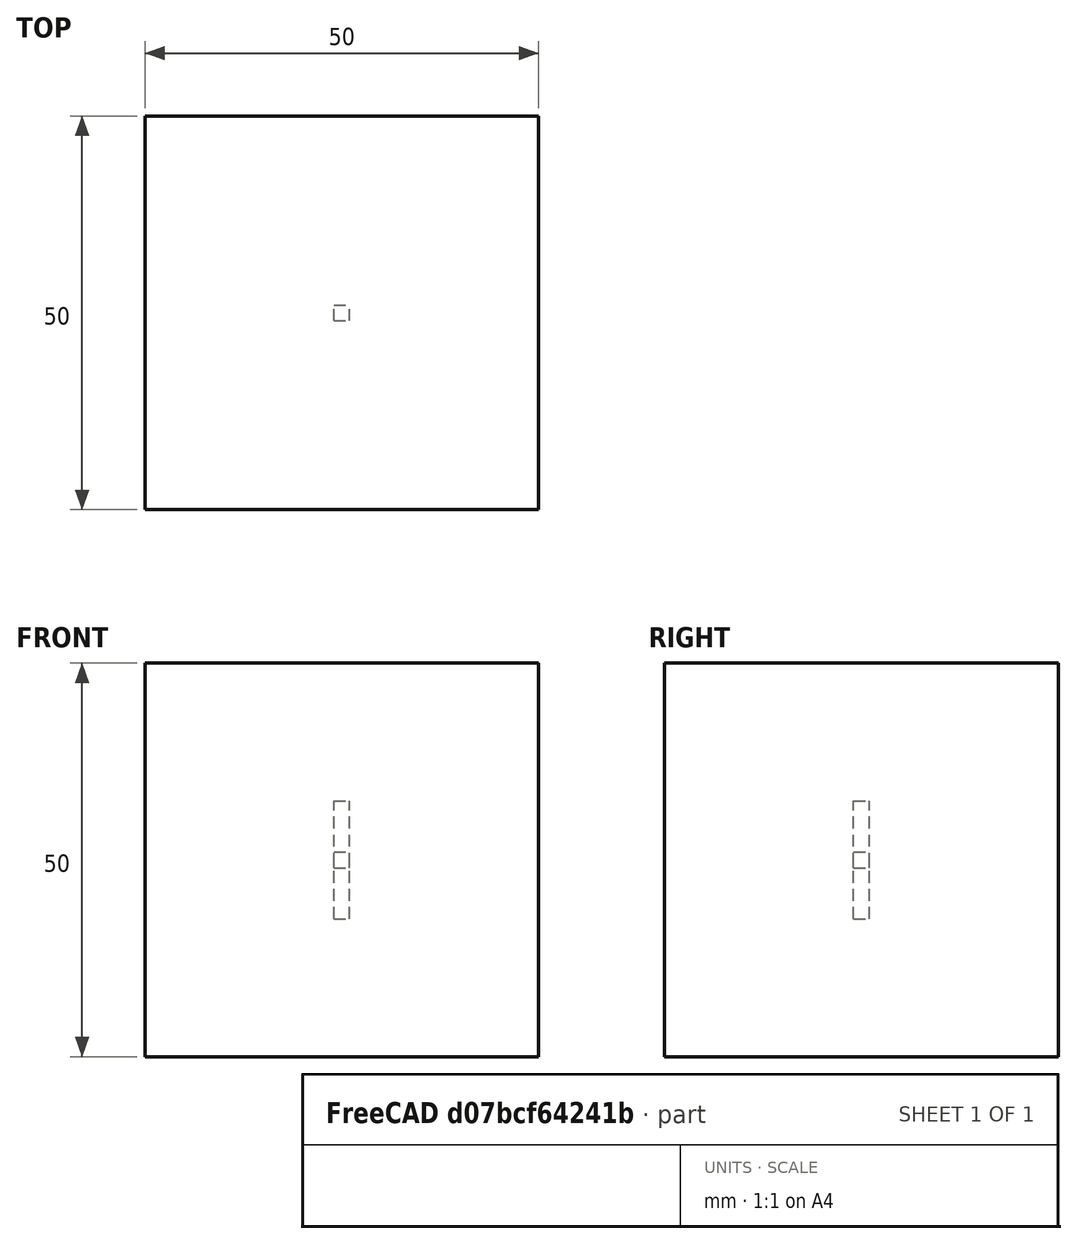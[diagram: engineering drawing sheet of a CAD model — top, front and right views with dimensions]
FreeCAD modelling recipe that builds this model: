
FCSTD DOCUMENT  (FreeCAD 1.0R39109 (Git))
Label: simple_array_expanded
License: All rights reserved
LicenseURL: http://en.wikipedia.org/wiki/All_rights_reserved
objects: App::DocumentObjectGroupPython×1269, App::Part×10, App::Link×6, App::FeaturePython×4, Part::FeaturePython×3
note: 3 computed .brp shape members not serialized (recipe doc carries the construction recipe); baked Part::Feature solids carry a one-line shape summary decoded from their .brp

FEATURE [App::DocumentObjectGroupPython] Constants  # scripted group (container) (typed FeaturePython)
FEATURE [App::DocumentObjectGroupPython] Variables  # scripted group (container) (typed FeaturePython)
FEATURE [App::DocumentObjectGroupPython] Quantities  # scripted group (container) (typed FeaturePython)
FEATURE [App::DocumentObjectGroupPython] Isotopes  # scripted group (container) (typed FeaturePython)
FEATURE [App::DocumentObjectGroupPython] Elements  # scripted group (container) (typed FeaturePython)
FEATURE [App::DocumentObjectGroupPython] G4_CESIUM_IODIDE  label="G4_CESIUM_IODIDE : 1.000"  # scripted group (container) (typed FeaturePython)
  n = 1
FEATURE [App::DocumentObjectGroupPython] LYSO  # scripted group (container) (typed FeaturePython)
  ABSLENGTH = ABSLENGTHLAR
  Dunit = g/cm3
  Dvalue = 7.1
  FASTCOMPONENT = SCINTLAR
  Group = -> [G4_CESIUM_IODIDE]
  RAYLEIGH = RAYLEIGHLAR
  REEMISSIONPROB = SCINTLAR
  RESOLUTIONSCALE = RS
  RINDEX = RINDEXLAR
  SCINTILLATIONCOMPONENT1 = SCINTLAR
  SCINTILLATIONCOMPONENT2 = SCINTLAR
  SCINTILLATIONTIMECONSTANT1 = FTC
  SCINTILLATIONTIMECONSTANT2 = STC
  SCINTILLATIONYIELD = SY
  SCINTILLATIONYIELD1 = RY1
  SCINTILLATIONYIELD2 = RY2
  SLOWCOMPONENT = SCINTLAR
  YIELDRATIO = YR
  conduct = 2
  density = 1
  expand = 3
  name = LYSO
  specific = 4
FEATURE [App::DocumentObjectGroupPython] G4_AIR  label="G4_AIR : 1.000"  # scripted group (container) (typed FeaturePython)
  n = 1
FEATURE [App::DocumentObjectGroupPython] Air  # scripted group (container) (typed FeaturePython)
  Dunit = mg/cm3
  Dvalue = 1.29
  Group = -> [G4_AIR]
  RINDEX = AirRINDEX
  conduct = 2
  density = 1
  expand = 3
  name = Air
  specific = 4
FEATURE [App::DocumentObjectGroupPython] G4_SILICON_DIOXIDE  label="G4_SILICON_DIOXIDE : 1.000"  # scripted group (container) (typed FeaturePython)
  n = 1
FEATURE [App::DocumentObjectGroupPython] Glass  # scripted group (container) (typed FeaturePython)
  Dunit = g/cm3
  Dvalue = 2.32
  Group = -> [G4_SILICON_DIOXIDE]
  RINDEX = RINDEXLAR
  conduct = 2
  density = 1
  expand = 3
  name = Glass
  specific = 4
FEATURE [App::DocumentObjectGroupPython] SY  # scripted group (container) (typed FeaturePython)
  coldim = 1
  values = 100000
FEATURE [App::DocumentObjectGroupPython] RS  # scripted group (container) (typed FeaturePython)
  coldim = 1
  values = 1
FEATURE [App::DocumentObjectGroupPython] FTC  # scripted group (container) (typed FeaturePython)
  coldim = 1
  values = 21.5*ns
FEATURE [App::DocumentObjectGroupPython] STC  # scripted group (container) (typed FeaturePython)
  coldim = 1
  values = 43.8*ns
FEATURE [App::DocumentObjectGroupPython] RY1  # scripted group (container) (typed FeaturePython)
  coldim = 1
  values = 95
FEATURE [App::DocumentObjectGroupPython] RY2  # scripted group (container) (typed FeaturePython)
  coldim = 1
  values = 5
FEATURE [App::DocumentObjectGroupPython] YR  # scripted group (container) (typed FeaturePython)
  coldim = 1
  values = 0.8
FEATURE [App::DocumentObjectGroupPython] SCINTLAR  # scripted group (container) (typed FeaturePython)
  coldim = 2
  values = <blob: 2358 chars omitted>
FEATURE [App::DocumentObjectGroupPython] RINDEXLAR  # scripted group (container) (typed FeaturePython)
  coldim = 2
  values = <blob: 9384 chars omitted>
FEATURE [App::DocumentObjectGroupPython] ABSLENGTHLAR  # scripted group (container) (typed FeaturePython)
  coldim = 2
  values = 7.74901*eV 10.0*m 7.77525*eV 10.0*m 7.80167*eV 10.0*m 7.82827*eV 10.0*m 7.85506*eV 10.0*m 7.88202*eV 10.0*m 7.90917*eV 10.0*m 7.93651*eV 10.0*m 7.96404*eV 10.0*m 7.99176*eV 10.0*m 8.01968*eV 10.0*m 8.04779*eV 10.0*m 8.07609*eV 10.0*m 8.1046*eV 10.0*m 8.13331*eV 10.0*m 8.16222*eV 10.0*m 8.19134*eV 10.0*m 8.22067*eV 10.0*m 8.25021*eV 10.0*m 8.27996*eV 10.0*m 8.30993*eV 10.0*m 8.34012*eV 10.0*m 8.37052*eV 10.0*m 8.40115*eV 10.0*m 8.432*eV 10.0*m 8.46308*eV 10.0*m 8.4944*eV 10.0*m 8.52594*eV 10.0*m 8.55772*eV 10.0*m 8.58973*eV 10.0*m 8.62199*eV 10.0*m 8.65449*eV 10.0*m 8.68723*eV 10.0*m 8.72023*eV 10.0*m 8.75347*eV 10.0*m 8.78697*eV 10.0*m 8.82073*eV 10.0*m 8.85475*eV 10.0*m 8.88903*eV 10.0*m 8.92358*eV 10.0*m 8.9584*eV 10.0*m 8.99349*eV 10.0*m 9.02885*eV 10.0*m 9.0645*eV 10.0*m 9.10043*eV 10.0*m 9.13664*eV 10.0*m 9.17314*eV 10.0*m 9.20994*eV 10.0*m 9.24703*eV 10.0*m 9.28442*eV 10.0*m 9.32212*eV 10.0*m 9.36012*eV 10.0*m 9.39844*eV 10.0*m 9.43707*eV 10.0*m 9.47602*eV 10.0*m 9.51529*eV 10.0*m 9.55489*eV 10.0*m 9.59481*eV 10.0*m 9.63508*eV 10.0*m 9.67568*eV 10.0*m 9.71663*eV 10.0*m 9.75792*eV 10.0*m 9.79957*eV 10.0*m 9.84158*eV 10.0*m 9.88394*eV 10.0*m 9.92668*eV 10.0*m 9.96978*eV 10.0*m 10.0133*eV 10.0*m 10.0571*eV 10.0*m 10.1014*eV 10.0*m 10.146*eV 10.0*m 10.191*eV 10.0*m 10.2365*eV 10.0*m 10.2823*eV 10.0*m 10.3286*eV 10.0*m 10.3752*eV 10.0*m 10.4223*eV 10.0*m 10.4699*eV 10.0*m 10.5178*eV 10.0*m 10.5662*eV 10.0*m 10.6151*eV 10.0*m 10.6644*eV 10.0*m 10.7142*eV 10.0*m 10.7644*eV 10.0*m 10.8151*eV 10.0*m 10.8663*eV 10.0*m 10.9179*eV 10.0*m 10.9701*eV 10.0*m 11.0228*eV 10.0*m 11.076*eV 10.0*m 11.1296*eV 10.0*m 11.1839*eV 10.0*m 11.2386*eV 10.0*m 11.2939*eV 10.0*m 11.3497*eV 10.0*m 11.4061*eV 10.0*m 11.463*eV 10.0*m 11.5206*eV 10.0*m 11.5787*eV 10.0*m 11.6373*eV 10.0*m
FEATURE [App::DocumentObjectGroupPython] RAYLEIGHLAR  # scripted group (container) (typed FeaturePython)
  coldim = 2
  values = 7.74901*eV 90.0*cm 7.77525*eV 90.0*cm 7.80167*eV 90.0*cm 7.82827*eV 90.0*cm 7.85506*eV 90.0*cm 7.88202*eV 90.0*cm 7.90917*eV 90.0*cm 7.93651*eV 90.0*cm 7.96404*eV 90.0*cm 7.99176*eV 90.0*cm 8.01968*eV 90.0*cm 8.04779*eV 90.0*cm 8.07609*eV 90.0*cm 8.1046*eV 90.0*cm 8.13331*eV 90.0*cm 8.16222*eV 90.0*cm 8.19134*eV 90.0*cm 8.22067*eV 90.0*cm 8.25021*eV 90.0*cm 8.27996*eV 90.0*cm 8.30993*eV 90.0*cm 8.34012*eV 90.0*cm 8.37052*eV 90.0*cm 8.40115*eV 90.0*cm 8.432*eV 90.0*cm 8.46308*eV 90.0*cm 8.4944*eV 90.0*cm 8.52594*eV 90.0*cm 8.55772*eV 90.0*cm 8.58973*eV 90.0*cm 8.62199*eV 90.0*cm 8.65449*eV 90.0*cm 8.68723*eV 90.0*cm 8.72023*eV 90.0*cm 8.75347*eV 90.0*cm 8.78697*eV 90.0*cm 8.82073*eV 90.0*cm 8.85475*eV 90.0*cm 8.88903*eV 90.0*cm 8.92358*eV 90.0*cm 8.9584*eV 90.0*cm 8.99349*eV 90.0*cm 9.02885*eV 90.0*cm 9.0645*eV 90.0*cm 9.10043*eV 90.0*cm 9.13664*eV 90.0*cm 9.17314*eV 90.0*cm 9.20994*eV 90.0*cm 9.24703*eV 90.0*cm 9.28442*eV 90.0*cm 9.32212*eV 90.0*cm 9.36012*eV 90.0*cm 9.39844*eV 90.0*cm 9.43707*eV 90.0*cm 9.47602*eV 90.0*cm 9.51529*eV 90.0*cm 9.55489*eV 90.0*cm 9.59481*eV 90.0*cm 9.63508*eV 90.0*cm 9.67568*eV 90.0*cm 9.71663*eV 90.0*cm 9.75792*eV 90.0*cm 9.79957*eV 90.0*cm 9.84158*eV 90.0*cm 9.88394*eV 90.0*cm 9.92668*eV 90.0*cm 9.96978*eV 90.0*cm 10.0133*eV 90.0*cm 10.0571*eV 90.0*cm 10.1014*eV 90.0*cm 10.146*eV 90.0*cm 10.191*eV 90.0*cm 10.2365*eV 90.0*cm 10.2823*eV 90.0*cm 10.3286*eV 90.0*cm 10.3752*eV 90.0*cm 10.4223*eV 90.0*cm 10.4699*eV 90.0*cm 10.5178*eV 90.0*cm 10.5662*eV 90.0*cm 10.6151*eV 90.0*cm 10.6644*eV 90.0*cm 10.7142*eV 90.0*cm 10.7644*eV 90.0*cm 10.8151*eV 90.0*cm 10.8663*eV 90.0*cm 10.9179*eV 90.0*cm 10.9701*eV 90.0*cm 11.0228*eV 90.0*cm 11.076*eV 90.0*cm 11.1296*eV 90.0*cm 11.1839*eV 90.0*cm 11.2386*eV 90.0*cm 11.2939*eV 90.0*cm 11.3497*eV 90.0*cm 11.4061*eV 90.0*cm 11.463*eV 90.0*cm 11.5206*eV 90.0*cm 11.5787*eV 90.0*cm 11.6373*eV 90.0*cm
FEATURE [App::DocumentObjectGroupPython] REFLECTIVITY  # scripted group (container) (typed FeaturePython)
  coldim = 2
  values = 2.034*eV 0.98 2.068*eV 0.98 2.103*eV 0.98 2.139*eV 0.98 2.177*eV 0.98 2.216*eV 0.98 2.256*eV 0.98 2.298*eV 0.98 2.341*eV 0.98 2.386*eV 0.98 2.433*eV 0.98 2.481*eV 0.98 2.532*eV 0.98 2.585*eV 0.98 2.64*eV 0.98 2.697*eV 0.98 2.757*eV 0.98 2.82*eV 0.98 2.885*eV 0.98 2.954*eV 0.98 3.026*eV 0.98 3.102*eV 0.98 3.181*eV 0.98 3.265*eV 0.98 3.353*eV 0.98 3.446*eV 0.98 3.545*eV 0.98 3.649*eV 0.98 3.76*eV 0.98 3.877*eV 0.98 4.002*eV 0.98 4.136*eV 0.98 5.0*eV 0.98 6.0*eV 0.98 7.0*eV 0.98 8.0*eV 0.98 9.0*eV 0.98 9.0*eV 0.98 10.0*eV 0.98 11.0*eV 0.98 11.6*eV 0.98
FEATURE [App::DocumentObjectGroupPython] EFFICIENCY  # scripted group (container) (typed FeaturePython)
  coldim = 2
  values = 2.034*eV 1 2.068*eV 1 2.103*eV 1 2.139*eV 1 2.177*eV 1 2.216*eV 1 2.256*eV 1 2.298*eV 1 2.341*eV 1 2.386*eV 1 2.433*eV 1 2.481*eV 1 2.532*eV 1 2.585*eV 1 2.64*eV 1 2.697*eV 1 2.757*eV 1 2.82*eV 1 2.885*eV 1 2.954*eV 1 3.026*eV 1 3.102*eV 1 3.181*eV  1 3.265*eV 1 3.353*eV 1 3.446*eV 1 3.545*eV 1 3.649*eV 1 3.76*eV 1 3.877*eV 1 4.002*eV 1 4.136*eV 1 5.0*eV 1 6.0*eV 1 7.0*eV 1 8.0*eV 1 9.0*eV 1 9.0*eV 1 10.0*eV 1 11.0*eV 1 11.6*eV 1
FEATURE [App::DocumentObjectGroupPython] AirRINDEX  # scripted group (container) (typed FeaturePython)
  coldim = 2
  values = 2.034*eV 1 2.068*eV 1 2.103*eV 1 2.139*eV 1 2.177*eV 1 2.216*eV 1 2.256*eV 1 2.298*eV 1 2.341*eV 1 2.386*eV 1 2.433*eV 1 2.481*eV 1 2.532*eV 1 2.585*eV 1 2.64*eV 1 2.697*eV 1 2.757*eV 1 2.82*eV 1 2.885*eV 1 2.954*eV 1 3.026*eV 1 3.102*eV 1 3.181*eV 1 3.265*eV 1 3.353*eV 1 3.446*eV 1 3.545*eV 1 3.649*eV 1 3.76*eV 1 3.877*eV 1 4.002*eV 1 4.136*eV 1 5.0*eV 1 6.0*eV 1 7.0*eV 1 8.0*eV 1 9.0*eV 1 10.0*eV 1 11.0*eV 1 11.6*eV 1
FEATURE [App::DocumentObjectGroupPython] Matrix  # scripted group (container) (typed FeaturePython)
  Group = -> [SY,RS,FTC,STC,RY1,RY2,YR,SCINTLAR,RINDEXLAR,ABSLENGTHLAR,RAYLEIGHLAR,REFLECTIVITY,EFFICIENCY,AirRINDEX]
FEATURE [App::DocumentObjectGroupPython] ScintWrap  # scripted group (container) (typed FeaturePython)
  EFFICIENCY = EFFICIENCY
  REFLECTIVITY = REFLECTIVITY
  finish = 39
  model = 0
  type = 2
  value = 1
FEATURE [App::DocumentObjectGroupPython] Surfaces  # scripted group (container) (typed FeaturePython)
  Group = -> [ScintWrap]
FEATURE [App::DocumentObjectGroupPython] Opticals  # scripted group (container) (typed FeaturePython)
  Group = -> [Matrix,Surfaces]
FEATURE [App::DocumentObjectGroupPython] G4Isotopes  # scripted group (container) (typed FeaturePython)
FEATURE [App::DocumentObjectGroupPython] H_element  # scripted group (container) (typed FeaturePython)
  Z = 1
  atom_value = 1.008
  formula = H
  name = H_element
FEATURE [App::DocumentObjectGroupPython] He_element  # scripted group (container) (typed FeaturePython)
  Z = 2
  atom_value = 4.0026
  formula = He
  name = He_element
FEATURE [App::DocumentObjectGroupPython] Li_element  # scripted group (container) (typed FeaturePython)
  Z = 3
  atom_value = 6.94
  formula = Li
  name = Li_element
FEATURE [App::DocumentObjectGroupPython] Be_element  # scripted group (container) (typed FeaturePython)
  Z = 4
  atom_value = 9.01218
  formula = Be
  name = Be_element
FEATURE [App::DocumentObjectGroupPython] B_element  # scripted group (container) (typed FeaturePython)
  Z = 5
  atom_value = 10.81
  formula = B
  name = B_element
FEATURE [App::DocumentObjectGroupPython] C_element  # scripted group (container) (typed FeaturePython)
  Z = 6
  atom_value = 12.011
  formula = C
  name = C_element
FEATURE [App::DocumentObjectGroupPython] N_element  # scripted group (container) (typed FeaturePython)
  Z = 7
  atom_value = 14.007
  formula = N
  name = N_element
FEATURE [App::DocumentObjectGroupPython] O_element  # scripted group (container) (typed FeaturePython)
  Z = 8
  atom_value = 15.999
  formula = O
  name = O_element
FEATURE [App::DocumentObjectGroupPython] F_element  # scripted group (container) (typed FeaturePython)
  Z = 9
  atom_value = 18.9984
  formula = F
  name = F_element
FEATURE [App::DocumentObjectGroupPython] Ne_element  # scripted group (container) (typed FeaturePython)
  Z = 10
  atom_value = 20.1797
  formula = Ne
  name = Ne_element
FEATURE [App::DocumentObjectGroupPython] Na_element  # scripted group (container) (typed FeaturePython)
  Z = 11
  atom_value = 22.9898
  formula = Na
  name = Na_element
FEATURE [App::DocumentObjectGroupPython] Mg_element  # scripted group (container) (typed FeaturePython)
  Z = 12
  atom_value = 24.305
  formula = Mg
  name = Mg_element
FEATURE [App::DocumentObjectGroupPython] Al_element  # scripted group (container) (typed FeaturePython)
  Z = 13
  atom_value = 26.9815
  formula = Al
  name = Al_element
FEATURE [App::DocumentObjectGroupPython] Si_element  # scripted group (container) (typed FeaturePython)
  Z = 14
  atom_value = 28.085
  formula = Si
  name = Si_element
FEATURE [App::DocumentObjectGroupPython] P_element  # scripted group (container) (typed FeaturePython)
  Z = 15
  atom_value = 30.9738
  formula = P
  name = P_element
FEATURE [App::DocumentObjectGroupPython] S_element  # scripted group (container) (typed FeaturePython)
  Z = 16
  atom_value = 32.06
  formula = S
  name = S_element
FEATURE [App::DocumentObjectGroupPython] Cl_element  # scripted group (container) (typed FeaturePython)
  Z = 17
  atom_value = 35.45
  formula = Cl
  name = Cl_element
FEATURE [App::DocumentObjectGroupPython] Ar_element  # scripted group (container) (typed FeaturePython)
  Z = 18
  atom_value = 39.95
  formula = Ar
  name = Ar_element
FEATURE [App::DocumentObjectGroupPython] K_element  # scripted group (container) (typed FeaturePython)
  Z = 19
  atom_value = 39.0983
  formula = K
  name = K_element
FEATURE [App::DocumentObjectGroupPython] Ca_element  # scripted group (container) (typed FeaturePython)
  Z = 20
  atom_value = 40.078
  formula = Ca
  name = Ca_element
FEATURE [App::DocumentObjectGroupPython] Sc_element  # scripted group (container) (typed FeaturePython)
  Z = 21
  atom_value = 44.9559
  formula = Sc
  name = Sc_element
FEATURE [App::DocumentObjectGroupPython] Ti_element  # scripted group (container) (typed FeaturePython)
  Z = 22
  atom_value = 47.867
  formula = Ti
  name = Ti_element
FEATURE [App::DocumentObjectGroupPython] V_element  # scripted group (container) (typed FeaturePython)
  Z = 23
  atom_value = 50.9415
  formula = V
  name = V_element
FEATURE [App::DocumentObjectGroupPython] Cr_element  # scripted group (container) (typed FeaturePython)
  Z = 24
  atom_value = 51.9961
  formula = Cr
  name = Cr_element
FEATURE [App::DocumentObjectGroupPython] Mn_element  # scripted group (container) (typed FeaturePython)
  Z = 25
  atom_value = 54.938
  formula = Mn
  name = Mn_element
FEATURE [App::DocumentObjectGroupPython] Fe_element  # scripted group (container) (typed FeaturePython)
  Z = 26
  atom_value = 55.845
  formula = Fe
  name = Fe_element
FEATURE [App::DocumentObjectGroupPython] Co_element  # scripted group (container) (typed FeaturePython)
  Z = 27
  atom_value = 58.9332
  formula = Co
  name = Co_element
FEATURE [App::DocumentObjectGroupPython] Ni_element  # scripted group (container) (typed FeaturePython)
  Z = 28
  atom_value = 58.6934
  formula = Ni
  name = Ni_element
FEATURE [App::DocumentObjectGroupPython] Cu_element  # scripted group (container) (typed FeaturePython)
  Z = 29
  atom_value = 63.546
  formula = Cu
  name = Cu_element
FEATURE [App::DocumentObjectGroupPython] Zn_element  # scripted group (container) (typed FeaturePython)
  Z = 30
  atom_value = 65.38
  formula = Zn
  name = Zn_element
FEATURE [App::DocumentObjectGroupPython] Ga_element  # scripted group (container) (typed FeaturePython)
  Z = 31
  atom_value = 69.723
  formula = Ga
  name = Ga_element
FEATURE [App::DocumentObjectGroupPython] Ge_element  # scripted group (container) (typed FeaturePython)
  Z = 32
  atom_value = 72.63
  formula = Ge
  name = Ge_element
FEATURE [App::DocumentObjectGroupPython] As_element  # scripted group (container) (typed FeaturePython)
  Z = 33
  atom_value = 74.9216
  formula = As
  name = As_element
FEATURE [App::DocumentObjectGroupPython] Se_element  # scripted group (container) (typed FeaturePython)
  Z = 34
  atom_value = 78.971
  formula = Se
  name = Se_element
FEATURE [App::DocumentObjectGroupPython] Br_element  # scripted group (container) (typed FeaturePython)
  Z = 35
  atom_value = 79.904
  formula = Br
  name = Br_element
FEATURE [App::DocumentObjectGroupPython] Kr_element  # scripted group (container) (typed FeaturePython)
  Z = 36
  atom_value = 83.798
  formula = Kr
  name = Kr_element
FEATURE [App::DocumentObjectGroupPython] Rb_element  # scripted group (container) (typed FeaturePython)
  Z = 37
  atom_value = 85.4678
  formula = Rb
  name = Rb_element
FEATURE [App::DocumentObjectGroupPython] Sr_element  # scripted group (container) (typed FeaturePython)
  Z = 38
  atom_value = 87.62
  formula = Sr
  name = Sr_element
FEATURE [App::DocumentObjectGroupPython] Y_element  # scripted group (container) (typed FeaturePython)
  Z = 39
  atom_value = 88.9058
  formula = Y
  name = Y_element
FEATURE [App::DocumentObjectGroupPython] Zr_element  # scripted group (container) (typed FeaturePython)
  Z = 40
  atom_value = 91.224
  formula = Zr
  name = Zr_element
FEATURE [App::DocumentObjectGroupPython] Nb_element  # scripted group (container) (typed FeaturePython)
  Z = 41
  atom_value = 92.9064
  formula = Nb
  name = Nb_element
FEATURE [App::DocumentObjectGroupPython] Mo_element  # scripted group (container) (typed FeaturePython)
  Z = 42
  atom_value = 95.95
  formula = Mo
  name = Mo_element
FEATURE [App::DocumentObjectGroupPython] Tc_element  # scripted group (container) (typed FeaturePython)
  Z = 43
  atom_value = 97
  formula = Tc
  name = Tc_element
FEATURE [App::DocumentObjectGroupPython] Ru_element  # scripted group (container) (typed FeaturePython)
  Z = 44
  atom_value = 101.07
  formula = Ru
  name = Ru_element
FEATURE [App::DocumentObjectGroupPython] Rh_element  # scripted group (container) (typed FeaturePython)
  Z = 45
  atom_value = 102.905
  formula = Rh
  name = Rh_element
FEATURE [App::DocumentObjectGroupPython] Pd_element  # scripted group (container) (typed FeaturePython)
  Z = 46
  atom_value = 106.42
  formula = Pd
  name = Pd_element
FEATURE [App::DocumentObjectGroupPython] Ag_element  # scripted group (container) (typed FeaturePython)
  Z = 47
  atom_value = 107.868
  formula = Ag
  name = Ag_element
FEATURE [App::DocumentObjectGroupPython] Cd_element  # scripted group (container) (typed FeaturePython)
  Z = 48
  atom_value = 112.414
  formula = Cd
  name = Cd_element
FEATURE [App::DocumentObjectGroupPython] In_element  # scripted group (container) (typed FeaturePython)
  Z = 49
  atom_value = 114.818
  formula = In
  name = In_element
FEATURE [App::DocumentObjectGroupPython] Sn_element  # scripted group (container) (typed FeaturePython)
  Z = 50
  atom_value = 118.71
  formula = Sn
  name = Sn_element
FEATURE [App::DocumentObjectGroupPython] Sb_element  # scripted group (container) (typed FeaturePython)
  Z = 51
  atom_value = 121.76
  formula = Sb
  name = Sb_element
FEATURE [App::DocumentObjectGroupPython] Te_element  # scripted group (container) (typed FeaturePython)
  Z = 52
  atom_value = 127.6
  formula = Te
  name = Te_element
FEATURE [App::DocumentObjectGroupPython] I_element  # scripted group (container) (typed FeaturePython)
  Z = 53
  atom_value = 126.904
  formula = I
  name = I_element
FEATURE [App::DocumentObjectGroupPython] Xe_element  # scripted group (container) (typed FeaturePython)
  Z = 54
  atom_value = 131.293
  formula = Xe
  name = Xe_element
FEATURE [App::DocumentObjectGroupPython] Cs_element  # scripted group (container) (typed FeaturePython)
  Z = 55
  atom_value = 132.905
  formula = Cs
  name = Cs_element
FEATURE [App::DocumentObjectGroupPython] Ba_element  # scripted group (container) (typed FeaturePython)
  Z = 56
  atom_value = 137.327
  formula = Ba
  name = Ba_element
FEATURE [App::DocumentObjectGroupPython] La_element  # scripted group (container) (typed FeaturePython)
  Z = 57
  atom_value = 138.905
  formula = La
  name = La_element
FEATURE [App::DocumentObjectGroupPython] Ce_element  # scripted group (container) (typed FeaturePython)
  Z = 58
  atom_value = 140.116
  formula = Ce
  name = Ce_element
FEATURE [App::DocumentObjectGroupPython] Pr_element  # scripted group (container) (typed FeaturePython)
  Z = 59
  atom_value = 140.908
  formula = Pr
  name = Pr_element
FEATURE [App::DocumentObjectGroupPython] Nd_element  # scripted group (container) (typed FeaturePython)
  Z = 60
  atom_value = 144.242
  formula = Nd
  name = Nd_element
FEATURE [App::DocumentObjectGroupPython] Pm_element  # scripted group (container) (typed FeaturePython)
  Z = 61
  atom_value = 145
  formula = Pm
  name = Pm_element
FEATURE [App::DocumentObjectGroupPython] Sm_element  # scripted group (container) (typed FeaturePython)
  Z = 62
  atom_value = 150.36
  formula = Sm
  name = Sm_element
FEATURE [App::DocumentObjectGroupPython] Eu_element  # scripted group (container) (typed FeaturePython)
  Z = 63
  atom_value = 151.964
  formula = Eu
  name = Eu_element
FEATURE [App::DocumentObjectGroupPython] Gd_element  # scripted group (container) (typed FeaturePython)
  Z = 64
  atom_value = 157.25
  formula = Gd
  name = Gd_element
FEATURE [App::DocumentObjectGroupPython] Tb_element  # scripted group (container) (typed FeaturePython)
  Z = 65
  atom_value = 158.925
  formula = Tb
  name = Tb_element
FEATURE [App::DocumentObjectGroupPython] Dy_element  # scripted group (container) (typed FeaturePython)
  Z = 66
  atom_value = 162.5
  formula = Dy
  name = Dy_element
FEATURE [App::DocumentObjectGroupPython] Ho_element  # scripted group (container) (typed FeaturePython)
  Z = 67
  atom_value = 164.93
  formula = Ho
  name = Ho_element
FEATURE [App::DocumentObjectGroupPython] Er_element  # scripted group (container) (typed FeaturePython)
  Z = 68
  atom_value = 167.259
  formula = Er
  name = Er_element
FEATURE [App::DocumentObjectGroupPython] Tm_element  # scripted group (container) (typed FeaturePython)
  Z = 69
  atom_value = 168.934
  formula = Tm
  name = Tm_element
FEATURE [App::DocumentObjectGroupPython] Yb_element  # scripted group (container) (typed FeaturePython)
  Z = 70
  atom_value = 173.045
  formula = Yb
  name = Yb_element
FEATURE [App::DocumentObjectGroupPython] Lu_element  # scripted group (container) (typed FeaturePython)
  Z = 71
  atom_value = 174.967
  formula = Lu
  name = Lu_element
FEATURE [App::DocumentObjectGroupPython] Hf_element  # scripted group (container) (typed FeaturePython)
  Z = 72
  atom_value = 178.49
  formula = Hf
  name = Hf_element
FEATURE [App::DocumentObjectGroupPython] Ta_element  # scripted group (container) (typed FeaturePython)
  Z = 73
  atom_value = 180.948
  formula = Ta
  name = Ta_element
FEATURE [App::DocumentObjectGroupPython] W_element  # scripted group (container) (typed FeaturePython)
  Z = 74
  atom_value = 183.84
  formula = W
  name = W_element
FEATURE [App::DocumentObjectGroupPython] Re_element  # scripted group (container) (typed FeaturePython)
  Z = 75
  atom_value = 186.207
  formula = Re
  name = Re_element
FEATURE [App::DocumentObjectGroupPython] Os_element  # scripted group (container) (typed FeaturePython)
  Z = 76
  atom_value = 190.23
  formula = Os
  name = Os_element
FEATURE [App::DocumentObjectGroupPython] Ir_element  # scripted group (container) (typed FeaturePython)
  Z = 77
  atom_value = 192.217
  formula = Ir
  name = Ir_element
FEATURE [App::DocumentObjectGroupPython] Pt_element  # scripted group (container) (typed FeaturePython)
  Z = 78
  atom_value = 195.084
  formula = Pt
  name = Pt_element
FEATURE [App::DocumentObjectGroupPython] Au_element  # scripted group (container) (typed FeaturePython)
  Z = 79
  atom_value = 196.967
  formula = Au
  name = Au_element
FEATURE [App::DocumentObjectGroupPython] Hg_element  # scripted group (container) (typed FeaturePython)
  Z = 80
  atom_value = 200.592
  formula = Hg
  name = Hg_element
FEATURE [App::DocumentObjectGroupPython] Tl_element  # scripted group (container) (typed FeaturePython)
  Z = 81
  atom_value = 204.38
  formula = Tl
  name = Tl_element
FEATURE [App::DocumentObjectGroupPython] Pb_element  # scripted group (container) (typed FeaturePython)
  Z = 82
  atom_value = 207.2
  formula = Pb
  name = Pb_element
FEATURE [App::DocumentObjectGroupPython] Bi_element  # scripted group (container) (typed FeaturePython)
  Z = 83
  atom_value = 208.98
  formula = Bi
  name = Bi_element
FEATURE [App::DocumentObjectGroupPython] Po_element  # scripted group (container) (typed FeaturePython)
  Z = 84
  atom_value = 209
  formula = Po
  name = Po_element
FEATURE [App::DocumentObjectGroupPython] At_element  # scripted group (container) (typed FeaturePython)
  Z = 85
  atom_value = 210
  formula = At
  name = At_element
FEATURE [App::DocumentObjectGroupPython] Rn_element  # scripted group (container) (typed FeaturePython)
  Z = 86
  atom_value = 222
  formula = Rn
  name = Rn_element
FEATURE [App::DocumentObjectGroupPython] Fr_element  # scripted group (container) (typed FeaturePython)
  Z = 87
  atom_value = 223
  formula = Fr
  name = Fr_element
FEATURE [App::DocumentObjectGroupPython] Ra_element  # scripted group (container) (typed FeaturePython)
  Z = 88
  atom_value = 226
  formula = Ra
  name = Ra_element
FEATURE [App::DocumentObjectGroupPython] Ac_element  # scripted group (container) (typed FeaturePython)
  Z = 89
  atom_value = 227
  formula = Ac
  name = Ac_element
FEATURE [App::DocumentObjectGroupPython] Th_element  # scripted group (container) (typed FeaturePython)
  Z = 90
  atom_value = 232.038
  formula = Th
  name = Th_element
FEATURE [App::DocumentObjectGroupPython] Pa_element  # scripted group (container) (typed FeaturePython)
  Z = 91
  atom_value = 231.036
  formula = Pa
  name = Pa_element
FEATURE [App::DocumentObjectGroupPython] U_element  # scripted group (container) (typed FeaturePython)
  Z = 92
  atom_value = 238.029
  formula = U
  name = U_element
FEATURE [App::DocumentObjectGroupPython] Np_element  # scripted group (container) (typed FeaturePython)
  Z = 93
  atom_value = 237
  formula = Np
  name = Np_element
FEATURE [App::DocumentObjectGroupPython] Pu_element  # scripted group (container) (typed FeaturePython)
  Z = 94
  atom_value = 244
  formula = Pu
  name = Pu_element
FEATURE [App::DocumentObjectGroupPython] Am_element  # scripted group (container) (typed FeaturePython)
  Z = 95
  atom_value = 243
  formula = Am
  name = Am_element
FEATURE [App::DocumentObjectGroupPython] Cm_element  # scripted group (container) (typed FeaturePython)
  Z = 96
  atom_value = 247
  formula = Cm
  name = Cm_element
FEATURE [App::DocumentObjectGroupPython] Bk_element  # scripted group (container) (typed FeaturePython)
  Z = 97
  atom_value = 247
  formula = Bk
  name = Bk_element
FEATURE [App::DocumentObjectGroupPython] Cf_element  # scripted group (container) (typed FeaturePython)
  Z = 98
  atom_value = 251
  formula = Cf
  name = Cf_element
FEATURE [App::DocumentObjectGroupPython] G4Elements  # scripted group (container) (typed FeaturePython)
  Group = -> [H_element,He_element,Li_element,Be_element,B_element,C_element,N_element,O_element,F_element,Ne_element,Na_element,Mg_element,Al_element,Si_element,P_element,S_element,Cl_element,Ar_element,K_element,Ca_element,Sc_element,Ti_element,V_element,Cr_element,Mn_element,Fe_element,Co_element,Ni_element,Cu_element,Zn_element,Ga_element,Ge_element,As_element,Se_element,Br_element,Kr_element,Rb_element,+61 more]
FEATURE [App::DocumentObjectGroupPython] H_element001  label="H_element : 0.101"  # scripted group (container) (typed FeaturePython)
  n = 0.101327
FEATURE [App::DocumentObjectGroupPython] C_element001  label="C_element : 0.775"  # scripted group (container) (typed FeaturePython)
  n = 0.7755
FEATURE [App::DocumentObjectGroupPython] N_element001  label="N_element : 0.035"  # scripted group (container) (typed FeaturePython)
  n = 0.035057
FEATURE [App::DocumentObjectGroupPython] O_element001  label="O_element : 0.052"  # scripted group (container) (typed FeaturePython)
  n = 0.0523159
FEATURE [App::DocumentObjectGroupPython] F_element001  label="F_element : 0.017"  # scripted group (container) (typed FeaturePython)
  n = 0.017422
FEATURE [App::DocumentObjectGroupPython] Ca_element001  label="Ca_element : 0.018"  # scripted group (container) (typed FeaturePython)
  n = 0.018378
FEATURE [App::DocumentObjectGroupPython] G4_A_150_TISSUE  label="G4_A-150_TISSUE"  # scripted group (container) (typed FeaturePython)
  Dunit = g/cm3
  Dvalue = 1.127
  Group = -> [H_element001,C_element001,N_element001,O_element001,F_element001,Ca_element001]
  conduct = 2
  density = 1
  expand = 3
  formula = G4_A-150_TISSUE
  name = G4_A-150_TISSUE
  specific = 4
FEATURE [App::DocumentObjectGroupPython] C_element002  label="C_element : 3"  # scripted group (container) (typed FeaturePython)
  n = 3
  ref = C_element
FEATURE [App::DocumentObjectGroupPython] H_element002  label="H_element : 6"  # scripted group (container) (typed FeaturePython)
  n = 6
  ref = H_element
FEATURE [App::DocumentObjectGroupPython] O_element002  label="O_element : 1"  # scripted group (container) (typed FeaturePython)
  n = 1
  ref = O_element
FEATURE [App::DocumentObjectGroupPython] G4_ACETONE  # scripted group (container) (typed FeaturePython)
  Dunit = g/cm3
  Dvalue = 0.7899
  Group = -> [C_element002,H_element002,O_element002]
  conduct = 2
  density = 1
  expand = 3
  formula = G4_ACETONE
  name = G4_ACETONE
  specific = 4
FEATURE [App::DocumentObjectGroupPython] C_element003  label="C_element : 2"  # scripted group (container) (typed FeaturePython)
  n = 2
  ref = C_element
FEATURE [App::DocumentObjectGroupPython] H_element003  label="H_element : 2"  # scripted group (container) (typed FeaturePython)
  n = 2
  ref = H_element
FEATURE [App::DocumentObjectGroupPython] G4_ACETYLENE  # scripted group (container) (typed FeaturePython)
  Dunit = g/cm3
  Dvalue = 0.0010967
  Group = -> [C_element003,H_element003]
  conduct = 2
  density = 1
  expand = 3
  formula = G4_ACETYLENE
  name = G4_ACETYLENE
  specific = 4
FEATURE [App::DocumentObjectGroupPython] C_element004  label="C_element : 5"  # scripted group (container) (typed FeaturePython)
  n = 5
  ref = C_element
FEATURE [App::DocumentObjectGroupPython] H_element004  label="H_element : 5"  # scripted group (container) (typed FeaturePython)
  n = 5
  ref = H_element
FEATURE [App::DocumentObjectGroupPython] N_element002  label="N_element : 5"  # scripted group (container) (typed FeaturePython)
  n = 5
  ref = N_element
FEATURE [App::DocumentObjectGroupPython] G4_ADENINE  # scripted group (container) (typed FeaturePython)
  Dunit = g/cm3
  Dvalue = 1.6
  Group = -> [C_element004,H_element004,N_element002]
  conduct = 2
  density = 1
  expand = 3
  formula = G4_ADENINE
  name = G4_ADENINE
  specific = 4
FEATURE [App::DocumentObjectGroupPython] H_element005  label="H_element : 0.114"  # scripted group (container) (typed FeaturePython)
  n = 0.114
FEATURE [App::DocumentObjectGroupPython] C_element005  label="C_element : 0.598"  # scripted group (container) (typed FeaturePython)
  n = 0.598
FEATURE [App::DocumentObjectGroupPython] N_element003  label="N_element : 0.007"  # scripted group (container) (typed FeaturePython)
  n = 0.007
FEATURE [App::DocumentObjectGroupPython] O_element003  label="O_element : 0.278"  # scripted group (container) (typed FeaturePython)
  n = 0.278
FEATURE [App::DocumentObjectGroupPython] Na_element001  label="Na_element : 0.001"  # scripted group (container) (typed FeaturePython)
  n = 0.001
FEATURE [App::DocumentObjectGroupPython] S_element001  label="S_element : 0.001"  # scripted group (container) (typed FeaturePython)
  n = 0.001
FEATURE [App::DocumentObjectGroupPython] Cl_element001  label="Cl_element : 0.001"  # scripted group (container) (typed FeaturePython)
  n = 0.001
FEATURE [App::DocumentObjectGroupPython] G4_ADIPOSE_TISSUE_ICRP  # scripted group (container) (typed FeaturePython)
  Dunit = g/cm3
  Dvalue = 0.95
  Group = -> [H_element005,C_element005,N_element003,O_element003,Na_element001,S_element001,Cl_element001]
  conduct = 2
  density = 1
  expand = 3
  formula = G4_ADIPOSE_TISSUE_ICRP
  name = G4_ADIPOSE_TISSUE_ICRP
  specific = 4
FEATURE [App::DocumentObjectGroupPython] C_element006  label="C_element : 0.000"  # scripted group (container) (typed FeaturePython)
  n = 0.000124
FEATURE [App::DocumentObjectGroupPython] N_element004  label="N_element : 0.755"  # scripted group (container) (typed FeaturePython)
  n = 0.755268
FEATURE [App::DocumentObjectGroupPython] O_element004  label="O_element : 0.232"  # scripted group (container) (typed FeaturePython)
  n = 0.231781
FEATURE [App::DocumentObjectGroupPython] Ar_element001  label="Ar_element : 0.013"  # scripted group (container) (typed FeaturePython)
  n = 0.012827
FEATURE [App::DocumentObjectGroupPython] G4_AIR001  label="G4_AIR"  # scripted group (container) (typed FeaturePython)
  Dunit = g/cm3
  Dvalue = 0.00120479
  Group = -> [C_element006,N_element004,O_element004,Ar_element001]
  conduct = 2
  density = 1
  expand = 3
  formula = G4_AIR
  name = G4_AIR
  specific = 4
FEATURE [App::DocumentObjectGroupPython] C_element007  label="C_element : 006"  # scripted group (container) (typed FeaturePython)
  n = 3
  ref = C_element
FEATURE [App::DocumentObjectGroupPython] H_element006  label="H_element : 7"  # scripted group (container) (typed FeaturePython)
  n = 7
  ref = H_element
FEATURE [App::DocumentObjectGroupPython] N_element005  label="N_element : 1"  # scripted group (container) (typed FeaturePython)
  n = 1
  ref = N_element
FEATURE [App::DocumentObjectGroupPython] O_element005  label="O_element : 2"  # scripted group (container) (typed FeaturePython)
  n = 2
  ref = O_element
FEATURE [App::DocumentObjectGroupPython] G4_ALANINE  # scripted group (container) (typed FeaturePython)
  Dunit = g/cm3
  Dvalue = 1.42
  Group = -> [C_element007,H_element006,N_element005,O_element005]
  conduct = 2
  density = 1
  expand = 3
  formula = G4_ALANINE
  name = G4_ALANINE
  specific = 4
FEATURE [App::DocumentObjectGroupPython] Al_element001  label="Al_element : 2"  # scripted group (container) (typed FeaturePython)
  n = 2
  ref = Al_element
FEATURE [App::DocumentObjectGroupPython] O_element006  label="O_element : 3"  # scripted group (container) (typed FeaturePython)
  n = 3
  ref = O_element
FEATURE [App::DocumentObjectGroupPython] G4_ALUMINUM_OXIDE  # scripted group (container) (typed FeaturePython)
  Dunit = g/cm3
  Dvalue = 3.97
  Group = -> [Al_element001,O_element006]
  conduct = 2
  density = 1
  expand = 3
  formula = G4_ALUMINUM_OXIDE
  name = G4_ALUMINUM_OXIDE
  specific = 4
FEATURE [App::DocumentObjectGroupPython] H_element007  label="H_element : 0.106"  # scripted group (container) (typed FeaturePython)
  n = 0.10593
FEATURE [App::DocumentObjectGroupPython] C_element008  label="C_element : 0.789"  # scripted group (container) (typed FeaturePython)
  n = 0.788974
FEATURE [App::DocumentObjectGroupPython] O_element007  label="O_element : 0.105"  # scripted group (container) (typed FeaturePython)
  n = 0.105096
FEATURE [App::DocumentObjectGroupPython] G4_AMBER  # scripted group (container) (typed FeaturePython)
  Dunit = g/cm3
  Dvalue = 1.1
  Group = -> [H_element007,C_element008,O_element007]
  conduct = 2
  density = 1
  expand = 3
  formula = G4_AMBER
  name = G4_AMBER
  specific = 4
FEATURE [App::DocumentObjectGroupPython] N_element006  label="N_element : 006"  # scripted group (container) (typed FeaturePython)
  n = 1
  ref = N_element
FEATURE [App::DocumentObjectGroupPython] H_element008  label="H_element : 3"  # scripted group (container) (typed FeaturePython)
  n = 3
  ref = H_element
FEATURE [App::DocumentObjectGroupPython] G4_AMMONIA  # scripted group (container) (typed FeaturePython)
  Dunit = g/cm3
  Dvalue = 0.000826019
  Group = -> [N_element006,H_element008]
  conduct = 2
  density = 1
  expand = 3
  formula = G4_AMMONIA
  name = G4_AMMONIA
  specific = 4
FEATURE [App::DocumentObjectGroupPython] C_element009  label="C_element : 6"  # scripted group (container) (typed FeaturePython)
  n = 6
  ref = C_element
FEATURE [App::DocumentObjectGroupPython] H_element009  label="H_element : 008"  # scripted group (container) (typed FeaturePython)
  n = 7
  ref = H_element
FEATURE [App::DocumentObjectGroupPython] N_element007  label="N_element : 007"  # scripted group (container) (typed FeaturePython)
  n = 1
  ref = N_element
FEATURE [App::DocumentObjectGroupPython] G4_ANILINE  # scripted group (container) (typed FeaturePython)
  Dunit = g/cm3
  Dvalue = 1.0235
  Group = -> [C_element009,H_element009,N_element007]
  conduct = 2
  density = 1
  expand = 3
  formula = G4_ANILINE
  name = G4_ANILINE
  specific = 4
FEATURE [App::DocumentObjectGroupPython] C_element010  label="C_element : 14"  # scripted group (container) (typed FeaturePython)
  n = 14
  ref = C_element
FEATURE [App::DocumentObjectGroupPython] H_element010  label="H_element : 10"  # scripted group (container) (typed FeaturePython)
  n = 10
  ref = H_element
FEATURE [App::DocumentObjectGroupPython] G4_ANTHRACENE  # scripted group (container) (typed FeaturePython)
  Dunit = g/cm3
  Dvalue = 1.283
  Group = -> [C_element010,H_element010]
  conduct = 2
  density = 1
  expand = 3
  formula = G4_ANTHRACENE
  name = G4_ANTHRACENE
  specific = 4
FEATURE [App::DocumentObjectGroupPython] H_element011  label="H_element : 0.065"  # scripted group (container) (typed FeaturePython)
  n = 0.0654709
FEATURE [App::DocumentObjectGroupPython] C_element011  label="C_element : 0.537"  # scripted group (container) (typed FeaturePython)
  n = 0.536944
FEATURE [App::DocumentObjectGroupPython] N_element008  label="N_element : 0.021"  # scripted group (container) (typed FeaturePython)
  n = 0.0215
FEATURE [App::DocumentObjectGroupPython] O_element008  label="O_element : 0.032"  # scripted group (container) (typed FeaturePython)
  n = 0.032085
FEATURE [App::DocumentObjectGroupPython] F_element002  label="F_element : 0.167"  # scripted group (container) (typed FeaturePython)
  n = 0.167411
FEATURE [App::DocumentObjectGroupPython] Ca_element002  label="Ca_element : 0.177"  # scripted group (container) (typed FeaturePython)
  n = 0.176589
FEATURE [App::DocumentObjectGroupPython] G4_B_100_BONE  label="G4_B-100_BONE"  # scripted group (container) (typed FeaturePython)
  Dunit = g/cm3
  Dvalue = 1.45
  Group = -> [H_element011,C_element011,N_element008,O_element008,F_element002,Ca_element002]
  conduct = 2
  density = 1
  expand = 3
  formula = G4_B-100_BONE
  name = G4_B-100_BONE
  specific = 4
FEATURE [App::DocumentObjectGroupPython] H_element012  label="H_element : 0.057"  # scripted group (container) (typed FeaturePython)
  n = 0.057441
FEATURE [App::DocumentObjectGroupPython] C_element012  label="C_element : 0.790"  # scripted group (container) (typed FeaturePython)
  n = 0.774591
FEATURE [App::DocumentObjectGroupPython] O_element009  label="O_element : 0.168"  # scripted group (container) (typed FeaturePython)
  n = 0.167968
FEATURE [App::DocumentObjectGroupPython] G4_BAKELITE  # scripted group (container) (typed FeaturePython)
  Dunit = g/cm3
  Dvalue = 1.25
  Group = -> [H_element012,C_element012,O_element009]
  conduct = 2
  density = 1
  expand = 3
  formula = G4_BAKELITE
  name = G4_BAKELITE
  specific = 4
FEATURE [App::DocumentObjectGroupPython] Ba_element001  label="Ba_element : 1"  # scripted group (container) (typed FeaturePython)
  n = 1
  ref = Ba_element
FEATURE [App::DocumentObjectGroupPython] F_element003  label="F_element : 2"  # scripted group (container) (typed FeaturePython)
  n = 2
  ref = F_element
FEATURE [App::DocumentObjectGroupPython] G4_BARIUM_FLUORIDE  # scripted group (container) (typed FeaturePython)
  Dunit = g/cm3
  Dvalue = 4.89
  Group = -> [Ba_element001,F_element003]
  conduct = 2
  density = 1
  expand = 3
  formula = G4_BARIUM_FLUORIDE
  name = G4_BARIUM_FLUORIDE
  specific = 4
FEATURE [App::DocumentObjectGroupPython] Ba_element002  label="Ba_element : 002"  # scripted group (container) (typed FeaturePython)
  n = 1
  ref = Ba_element
FEATURE [App::DocumentObjectGroupPython] S_element002  label="S_element : 1"  # scripted group (container) (typed FeaturePython)
  n = 1
  ref = S_element
FEATURE [App::DocumentObjectGroupPython] O_element010  label="O_element : 4"  # scripted group (container) (typed FeaturePython)
  n = 4
  ref = O_element
FEATURE [App::DocumentObjectGroupPython] G4_BARIUM_SULFATE  # scripted group (container) (typed FeaturePython)
  Dunit = g/cm3
  Dvalue = 4.5
  Group = -> [Ba_element002,S_element002,O_element010]
  conduct = 2
  density = 1
  expand = 3
  formula = G4_BARIUM_SULFATE
  name = G4_BARIUM_SULFATE
  specific = 4
FEATURE [App::DocumentObjectGroupPython] C_element013  label="C_element : 007"  # scripted group (container) (typed FeaturePython)
  n = 6
  ref = C_element
FEATURE [App::DocumentObjectGroupPython] H_element013  label="H_element : 009"  # scripted group (container) (typed FeaturePython)
  n = 6
  ref = H_element
FEATURE [App::DocumentObjectGroupPython] G4_BENZENE  # scripted group (container) (typed FeaturePython)
  Dunit = g/cm3
  Dvalue = 0.87865
  Group = -> [C_element013,H_element013]
  conduct = 2
  density = 1
  expand = 3
  formula = G4_BENZENE
  name = G4_BENZENE
  specific = 4
FEATURE [App::DocumentObjectGroupPython] Be_element001  label="Be_element : 1"  # scripted group (container) (typed FeaturePython)
  n = 1
  ref = Be_element
FEATURE [App::DocumentObjectGroupPython] O_element011  label="O_element : 005"  # scripted group (container) (typed FeaturePython)
  n = 1
  ref = O_element
FEATURE [App::DocumentObjectGroupPython] G4_BERYLLIUM_OXIDE  # scripted group (container) (typed FeaturePython)
  Dunit = g/cm3
  Dvalue = 3.01
  Group = -> [Be_element001,O_element011]
  conduct = 2
  density = 1
  expand = 3
  formula = G4_BERYLLIUM_OXIDE
  name = G4_BERYLLIUM_OXIDE
  specific = 4
FEATURE [App::DocumentObjectGroupPython] Bi_element001  label="Bi_element : 4"  # scripted group (container) (typed FeaturePython)
  n = 4
  ref = Bi_element
FEATURE [App::DocumentObjectGroupPython] Ge_element001  label="Ge_element : 3"  # scripted group (container) (typed FeaturePython)
  n = 3
  ref = Ge_element
FEATURE [App::DocumentObjectGroupPython] O_element012  label="O_element : 12"  # scripted group (container) (typed FeaturePython)
  n = 12
  ref = O_element
FEATURE [App::DocumentObjectGroupPython] G4_BGO  # scripted group (container) (typed FeaturePython)
  Dunit = g/cm3
  Dvalue = 7.13
  Group = -> [Bi_element001,Ge_element001,O_element012]
  conduct = 2
  density = 1
  expand = 3
  formula = G4_BGO
  name = G4_BGO
  specific = 4
FEATURE [App::DocumentObjectGroupPython] H_element014  label="H_element : 0.102"  # scripted group (container) (typed FeaturePython)
  n = 0.102
FEATURE [App::DocumentObjectGroupPython] C_element014  label="C_element : 0.110"  # scripted group (container) (typed FeaturePython)
  n = 0.11
FEATURE [App::DocumentObjectGroupPython] N_element009  label="N_element : 0.033"  # scripted group (container) (typed FeaturePython)
  n = 0.033
FEATURE [App::DocumentObjectGroupPython] O_element013  label="O_element : 0.745"  # scripted group (container) (typed FeaturePython)
  n = 0.745
FEATURE [App::DocumentObjectGroupPython] Na_element002  label="Na_element : 0.002"  # scripted group (container) (typed FeaturePython)
  n = 0.001
FEATURE [App::DocumentObjectGroupPython] P_element001  label="P_element : 0.001"  # scripted group (container) (typed FeaturePython)
  n = 0.001
FEATURE [App::DocumentObjectGroupPython] S_element003  label="S_element : 0.002"  # scripted group (container) (typed FeaturePython)
  n = 0.002
FEATURE [App::DocumentObjectGroupPython] Cl_element002  label="Cl_element : 0.003"  # scripted group (container) (typed FeaturePython)
  n = 0.003
FEATURE [App::DocumentObjectGroupPython] K_element001  label="K_element : 0.002"  # scripted group (container) (typed FeaturePython)
  n = 0.002
FEATURE [App::DocumentObjectGroupPython] Fe_element001  label="Fe_element : 0.001"  # scripted group (container) (typed FeaturePython)
  n = 0.001
FEATURE [App::DocumentObjectGroupPython] G4_BLOOD_ICRP  # scripted group (container) (typed FeaturePython)
  Dunit = g/cm3
  Dvalue = 1.06
  Group = -> [H_element014,C_element014,N_element009,O_element013,Na_element002,P_element001,S_element003,Cl_element002,K_element001,Fe_element001]
  conduct = 2
  density = 1
  expand = 3
  formula = G4_BLOOD_ICRP
  name = G4_BLOOD_ICRP
  specific = 4
FEATURE [App::DocumentObjectGroupPython] H_element015  label="H_element : 0.064"  # scripted group (container) (typed FeaturePython)
  n = 0.064
FEATURE [App::DocumentObjectGroupPython] C_element015  label="C_element : 0.278"  # scripted group (container) (typed FeaturePython)
  n = 0.278
FEATURE [App::DocumentObjectGroupPython] N_element010  label="N_element : 0.027"  # scripted group (container) (typed FeaturePython)
  n = 0.027
FEATURE [App::DocumentObjectGroupPython] O_element014  label="O_element : 0.410"  # scripted group (container) (typed FeaturePython)
  n = 0.41
FEATURE [App::DocumentObjectGroupPython] Mg_element001  label="Mg_element : 0.002"  # scripted group (container) (typed FeaturePython)
  n = 0.002
FEATURE [App::DocumentObjectGroupPython] P_element002  label="P_element : 0.070"  # scripted group (container) (typed FeaturePython)
  n = 0.07
FEATURE [App::DocumentObjectGroupPython] S_element004  label="S_element : 0.003"  # scripted group (container) (typed FeaturePython)
  n = 0.002
FEATURE [App::DocumentObjectGroupPython] Ca_element003  label="Ca_element : 0.147"  # scripted group (container) (typed FeaturePython)
  n = 0.147
FEATURE [App::DocumentObjectGroupPython] G4_BONE_COMPACT_ICRU  # scripted group (container) (typed FeaturePython)
  Dunit = g/cm3
  Dvalue = 1.85
  Group = -> [H_element015,C_element015,N_element010,O_element014,Mg_element001,P_element002,S_element004,Ca_element003]
  conduct = 2
  density = 1
  expand = 3
  formula = G4_BONE_COMPACT_ICRU
  name = G4_BONE_COMPACT_ICRU
  specific = 4
FEATURE [App::DocumentObjectGroupPython] H_element016  label="H_element : 0.034"  # scripted group (container) (typed FeaturePython)
  n = 0.034
FEATURE [App::DocumentObjectGroupPython] C_element016  label="C_element : 0.155"  # scripted group (container) (typed FeaturePython)
  n = 0.155
FEATURE [App::DocumentObjectGroupPython] N_element011  label="N_element : 0.042"  # scripted group (container) (typed FeaturePython)
  n = 0.042
FEATURE [App::DocumentObjectGroupPython] O_element015  label="O_element : 0.435"  # scripted group (container) (typed FeaturePython)
  n = 0.435
FEATURE [App::DocumentObjectGroupPython] Na_element003  label="Na_element : 0.003"  # scripted group (container) (typed FeaturePython)
  n = 0.001
FEATURE [App::DocumentObjectGroupPython] Mg_element002  label="Mg_element : 0.003"  # scripted group (container) (typed FeaturePython)
  n = 0.002
FEATURE [App::DocumentObjectGroupPython] P_element003  label="P_element : 0.103"  # scripted group (container) (typed FeaturePython)
  n = 0.103
FEATURE [App::DocumentObjectGroupPython] S_element005  label="S_element : 0.004"  # scripted group (container) (typed FeaturePython)
  n = 0.003
FEATURE [App::DocumentObjectGroupPython] Ca_element004  label="Ca_element : 0.225"  # scripted group (container) (typed FeaturePython)
  n = 0.225
FEATURE [App::DocumentObjectGroupPython] G4_BONE_CORTICAL_ICRP  # scripted group (container) (typed FeaturePython)
  Dunit = g/cm3
  Dvalue = 1.92
  Group = -> [H_element016,C_element016,N_element011,O_element015,Na_element003,Mg_element002,P_element003,S_element005,Ca_element004]
  conduct = 2
  density = 1
  expand = 3
  formula = G4_BONE_CORTICAL_ICRP
  name = G4_BONE_CORTICAL_ICRP
  specific = 4
FEATURE [App::DocumentObjectGroupPython] B_element001  label="B_element : 4"  # scripted group (container) (typed FeaturePython)
  n = 4
  ref = B_element
FEATURE [App::DocumentObjectGroupPython] C_element017  label="C_element : 1"  # scripted group (container) (typed FeaturePython)
  n = 1
  ref = C_element
FEATURE [App::DocumentObjectGroupPython] G4_BORON_CARBIDE  # scripted group (container) (typed FeaturePython)
  Dunit = g/cm3
  Dvalue = 2.52
  Group = -> [B_element001,C_element017]
  conduct = 2
  density = 1
  expand = 3
  formula = G4_BORON_CARBIDE
  name = G4_BORON_CARBIDE
  specific = 4
FEATURE [App::DocumentObjectGroupPython] B_element002  label="B_element : 2"  # scripted group (container) (typed FeaturePython)
  n = 2
  ref = B_element
FEATURE [App::DocumentObjectGroupPython] O_element016  label="O_element : 006"  # scripted group (container) (typed FeaturePython)
  n = 3
  ref = O_element
FEATURE [App::DocumentObjectGroupPython] G4_BORON_OXIDE  # scripted group (container) (typed FeaturePython)
  Dunit = g/cm3
  Dvalue = 1.812
  Group = -> [B_element002,O_element016]
  conduct = 2
  density = 1
  expand = 3
  formula = G4_BORON_OXIDE
  name = G4_BORON_OXIDE
  specific = 4
FEATURE [App::DocumentObjectGroupPython] H_element017  label="H_element : 0.107"  # scripted group (container) (typed FeaturePython)
  n = 0.107
FEATURE [App::DocumentObjectGroupPython] C_element018  label="C_element : 0.145"  # scripted group (container) (typed FeaturePython)
  n = 0.145
FEATURE [App::DocumentObjectGroupPython] N_element012  label="N_element : 0.022"  # scripted group (container) (typed FeaturePython)
  n = 0.022
FEATURE [App::DocumentObjectGroupPython] O_element017  label="O_element : 0.712"  # scripted group (container) (typed FeaturePython)
  n = 0.712
FEATURE [App::DocumentObjectGroupPython] Na_element004  label="Na_element : 0.004"  # scripted group (container) (typed FeaturePython)
  n = 0.002
FEATURE [App::DocumentObjectGroupPython] P_element004  label="P_element : 0.004"  # scripted group (container) (typed FeaturePython)
  n = 0.004
FEATURE [App::DocumentObjectGroupPython] S_element006  label="S_element : 0.005"  # scripted group (container) (typed FeaturePython)
  n = 0.002
FEATURE [App::DocumentObjectGroupPython] Cl_element003  label="Cl_element : 0.004"  # scripted group (container) (typed FeaturePython)
  n = 0.003
FEATURE [App::DocumentObjectGroupPython] K_element002  label="K_element : 0.003"  # scripted group (container) (typed FeaturePython)
  n = 0.003
FEATURE [App::DocumentObjectGroupPython] G4_BRAIN_ICRP  # scripted group (container) (typed FeaturePython)
  Dunit = g/cm3
  Dvalue = 1.04
  Group = -> [H_element017,C_element018,N_element012,O_element017,Na_element004,P_element004,S_element006,Cl_element003,K_element002]
  conduct = 2
  density = 1
  expand = 3
  formula = G4_BRAIN_ICRP
  name = G4_BRAIN_ICRP
  specific = 4
FEATURE [App::DocumentObjectGroupPython] C_element019  label="C_element : 4"  # scripted group (container) (typed FeaturePython)
  n = 4
  ref = C_element
FEATURE [App::DocumentObjectGroupPython] H_element018  label="H_element : 010"  # scripted group (container) (typed FeaturePython)
  n = 10
  ref = H_element
FEATURE [App::DocumentObjectGroupPython] G4_BUTANE  # scripted group (container) (typed FeaturePython)
  Dunit = g/cm3
  Dvalue = 0.00249343
  Group = -> [C_element019,H_element018]
  conduct = 2
  density = 1
  expand = 3
  formula = G4_BUTANE
  name = G4_BUTANE
  specific = 4
FEATURE [App::DocumentObjectGroupPython] C_element020  label="C_element : 008"  # scripted group (container) (typed FeaturePython)
  n = 4
  ref = C_element
FEATURE [App::DocumentObjectGroupPython] H_element019  label="H_element : 011"  # scripted group (container) (typed FeaturePython)
  n = 10
  ref = H_element
FEATURE [App::DocumentObjectGroupPython] O_element018  label="O_element : 007"  # scripted group (container) (typed FeaturePython)
  n = 1
  ref = O_element
FEATURE [App::DocumentObjectGroupPython] G4_N_BUTYL_ALCOHOL  label="G4_N-BUTYL_ALCOHOL"  # scripted group (container) (typed FeaturePython)
  Dunit = g/cm3
  Dvalue = 0.8098
  Group = -> [C_element020,H_element019,O_element018]
  conduct = 2
  density = 1
  expand = 3
  formula = G4_N-BUTYL_ALCOHOL
  name = G4_N-BUTYL_ALCOHOL
  specific = 4
FEATURE [App::DocumentObjectGroupPython] H_element020  label="H_element : 0.025"  # scripted group (container) (typed FeaturePython)
  n = 0.02468
FEATURE [App::DocumentObjectGroupPython] C_element021  label="C_element : 0.502"  # scripted group (container) (typed FeaturePython)
  n = 0.501611
FEATURE [App::DocumentObjectGroupPython] O_element019  label="O_element : 0.005"  # scripted group (container) (typed FeaturePython)
  n = 0.004527
FEATURE [App::DocumentObjectGroupPython] F_element004  label="F_element : 0.465"  # scripted group (container) (typed FeaturePython)
  n = 0.465209
FEATURE [App::DocumentObjectGroupPython] Si_element001  label="Si_element : 0.004"  # scripted group (container) (typed FeaturePython)
  n = 0.003973
FEATURE [App::DocumentObjectGroupPython] G4_C_552  label="G4_C-552"  # scripted group (container) (typed FeaturePython)
  Dunit = g/cm3
  Dvalue = 1.76
  Group = -> [H_element020,C_element021,O_element019,F_element004,Si_element001]
  conduct = 2
  density = 1
  expand = 3
  formula = G4_C-552
  name = G4_C-552
  specific = 4
FEATURE [App::DocumentObjectGroupPython] Cd_element001  label="Cd_element : 1"  # scripted group (container) (typed FeaturePython)
  n = 1
  ref = Cd_element
FEATURE [App::DocumentObjectGroupPython] Te_element001  label="Te_element : 1"  # scripted group (container) (typed FeaturePython)
  n = 1
  ref = Te_element
FEATURE [App::DocumentObjectGroupPython] G4_CADMIUM_TELLURIDE  # scripted group (container) (typed FeaturePython)
  Dunit = g/cm3
  Dvalue = 6.2
  Group = -> [Cd_element001,Te_element001]
  conduct = 2
  density = 1
  expand = 3
  formula = G4_CADMIUM_TELLURIDE
  name = G4_CADMIUM_TELLURIDE
  specific = 4
FEATURE [App::DocumentObjectGroupPython] Cd_element002  label="Cd_element : 002"  # scripted group (container) (typed FeaturePython)
  n = 1
  ref = Cd_element
FEATURE [App::DocumentObjectGroupPython] W_element001  label="W_element : 1"  # scripted group (container) (typed FeaturePython)
  n = 1
  ref = W_element
FEATURE [App::DocumentObjectGroupPython] O_element020  label="O_element : 008"  # scripted group (container) (typed FeaturePython)
  n = 4
  ref = O_element
FEATURE [App::DocumentObjectGroupPython] G4_CADMIUM_TUNGSTATE  # scripted group (container) (typed FeaturePython)
  Dunit = g/cm3
  Dvalue = 7.9
  Group = -> [Cd_element002,W_element001,O_element020]
  conduct = 2
  density = 1
  expand = 3
  formula = G4_CADMIUM_TUNGSTATE
  name = G4_CADMIUM_TUNGSTATE
  specific = 4
FEATURE [App::DocumentObjectGroupPython] Ca_element005  label="Ca_element : 1"  # scripted group (container) (typed FeaturePython)
  n = 1
  ref = Ca_element
FEATURE [App::DocumentObjectGroupPython] C_element022  label="C_element : 009"  # scripted group (container) (typed FeaturePython)
  n = 1
  ref = C_element
FEATURE [App::DocumentObjectGroupPython] O_element021  label="O_element : 009"  # scripted group (container) (typed FeaturePython)
  n = 3
  ref = O_element
FEATURE [App::DocumentObjectGroupPython] G4_CALCIUM_CARBONATE  # scripted group (container) (typed FeaturePython)
  Dunit = g/cm3
  Dvalue = 2.8
  Group = -> [Ca_element005,C_element022,O_element021]
  conduct = 2
  density = 1
  expand = 3
  formula = G4_CALCIUM_CARBONATE
  name = G4_CALCIUM_CARBONATE
  specific = 4
FEATURE [App::DocumentObjectGroupPython] Ca_element006  label="Ca_element : 002"  # scripted group (container) (typed FeaturePython)
  n = 1
  ref = Ca_element
FEATURE [App::DocumentObjectGroupPython] F_element005  label="F_element : 003"  # scripted group (container) (typed FeaturePython)
  n = 2
  ref = F_element
FEATURE [App::DocumentObjectGroupPython] G4_CALCIUM_FLUORIDE  # scripted group (container) (typed FeaturePython)
  Dunit = g/cm3
  Dvalue = 3.18
  Group = -> [Ca_element006,F_element005]
  conduct = 2
  density = 1
  expand = 3
  formula = G4_CALCIUM_FLUORIDE
  name = G4_CALCIUM_FLUORIDE
  specific = 4
FEATURE [App::DocumentObjectGroupPython] Ca_element007  label="Ca_element : 003"  # scripted group (container) (typed FeaturePython)
  n = 1
  ref = Ca_element
FEATURE [App::DocumentObjectGroupPython] O_element022  label="O_element : 010"  # scripted group (container) (typed FeaturePython)
  n = 1
  ref = O_element
FEATURE [App::DocumentObjectGroupPython] G4_CALCIUM_OXIDE  # scripted group (container) (typed FeaturePython)
  Dunit = g/cm3
  Dvalue = 3.3
  Group = -> [Ca_element007,O_element022]
  conduct = 2
  density = 1
  expand = 3
  formula = G4_CALCIUM_OXIDE
  name = G4_CALCIUM_OXIDE
  specific = 4
FEATURE [App::DocumentObjectGroupPython] Ca_element008  label="Ca_element : 004"  # scripted group (container) (typed FeaturePython)
  n = 1
  ref = Ca_element
FEATURE [App::DocumentObjectGroupPython] S_element007  label="S_element : 002"  # scripted group (container) (typed FeaturePython)
  n = 1
  ref = S_element
FEATURE [App::DocumentObjectGroupPython] O_element023  label="O_element : 011"  # scripted group (container) (typed FeaturePython)
  n = 4
  ref = O_element
FEATURE [App::DocumentObjectGroupPython] G4_CALCIUM_SULFATE  # scripted group (container) (typed FeaturePython)
  Dunit = g/cm3
  Dvalue = 2.96
  Group = -> [Ca_element008,S_element007,O_element023]
  conduct = 2
  density = 1
  expand = 3
  formula = G4_CALCIUM_SULFATE
  name = G4_CALCIUM_SULFATE
  specific = 4
FEATURE [App::DocumentObjectGroupPython] Ca_element009  label="Ca_element : 005"  # scripted group (container) (typed FeaturePython)
  n = 1
  ref = Ca_element
FEATURE [App::DocumentObjectGroupPython] W_element002  label="W_element : 002"  # scripted group (container) (typed FeaturePython)
  n = 1
  ref = W_element
FEATURE [App::DocumentObjectGroupPython] O_element024  label="O_element : 012"  # scripted group (container) (typed FeaturePython)
  n = 4
  ref = O_element
FEATURE [App::DocumentObjectGroupPython] G4_CALCIUM_TUNGSTATE  # scripted group (container) (typed FeaturePython)
  Dunit = g/cm3
  Dvalue = 6.062
  Group = -> [Ca_element009,W_element002,O_element024]
  conduct = 2
  density = 1
  expand = 3
  formula = G4_CALCIUM_TUNGSTATE
  name = G4_CALCIUM_TUNGSTATE
  specific = 4
FEATURE [App::DocumentObjectGroupPython] C_element023  label="C_element : 010"  # scripted group (container) (typed FeaturePython)
  n = 1
  ref = C_element
FEATURE [App::DocumentObjectGroupPython] O_element025  label="O_element : 013"  # scripted group (container) (typed FeaturePython)
  n = 2
  ref = O_element
FEATURE [App::DocumentObjectGroupPython] G4_CARBON_DIOXIDE  # scripted group (container) (typed FeaturePython)
  Dunit = g/cm3
  Dvalue = 0.00184212
  Group = -> [C_element023,O_element025]
  conduct = 2
  density = 1
  expand = 3
  formula = G4_CARBON_DIOXIDE
  name = G4_CARBON_DIOXIDE
  specific = 4
FEATURE [App::DocumentObjectGroupPython] C_element024  label="C_element : 011"  # scripted group (container) (typed FeaturePython)
  n = 1
  ref = C_element
FEATURE [App::DocumentObjectGroupPython] Cl_element004  label="Cl_element : 4"  # scripted group (container) (typed FeaturePython)
  n = 4
  ref = Cl_element
FEATURE [App::DocumentObjectGroupPython] G4_CARBON_TETRACHLORIDE  # scripted group (container) (typed FeaturePython)
  Dunit = g/cm3
  Dvalue = 1.594
  Group = -> [C_element024,Cl_element004]
  conduct = 2
  density = 1
  expand = 3
  formula = G4_CARBON_TETRACHLORIDE
  name = G4_CARBON_TETRACHLORIDE
  specific = 4
FEATURE [App::DocumentObjectGroupPython] C_element025  label="C_element : 012"  # scripted group (container) (typed FeaturePython)
  n = 6
  ref = C_element
FEATURE [App::DocumentObjectGroupPython] H_element021  label="H_element : 012"  # scripted group (container) (typed FeaturePython)
  n = 10
  ref = H_element
FEATURE [App::DocumentObjectGroupPython] O_element026  label="O_element : 5"  # scripted group (container) (typed FeaturePython)
  n = 5
  ref = O_element
FEATURE [App::DocumentObjectGroupPython] G4_CELLULOSE_CELLOPHANE  # scripted group (container) (typed FeaturePython)
  Dunit = g/cm3
  Dvalue = 1.42
  Group = -> [C_element025,H_element021,O_element026]
  conduct = 2
  density = 1
  expand = 3
  formula = G4_CELLULOSE_CELLOPHANE
  name = G4_CELLULOSE_CELLOPHANE
  specific = 4
FEATURE [App::DocumentObjectGroupPython] H_element022  label="H_element : 0.067"  # scripted group (container) (typed FeaturePython)
  n = 0.067125
FEATURE [App::DocumentObjectGroupPython] C_element026  label="C_element : 0.545"  # scripted group (container) (typed FeaturePython)
  n = 0.545403
FEATURE [App::DocumentObjectGroupPython] O_element027  label="O_element : 0.387"  # scripted group (container) (typed FeaturePython)
  n = 0.387472
FEATURE [App::DocumentObjectGroupPython] G4_CELLULOSE_BUTYRATE  # scripted group (container) (typed FeaturePython)
  Dunit = g/cm3
  Dvalue = 1.2
  Group = -> [H_element022,C_element026,O_element027]
  conduct = 2
  density = 1
  expand = 3
  formula = G4_CELLULOSE_BUTYRATE
  name = G4_CELLULOSE_BUTYRATE
  specific = 4
FEATURE [App::DocumentObjectGroupPython] H_element023  label="H_element : 0.029"  # scripted group (container) (typed FeaturePython)
  n = 0.029216
FEATURE [App::DocumentObjectGroupPython] C_element027  label="C_element : 0.271"  # scripted group (container) (typed FeaturePython)
  n = 0.271296
FEATURE [App::DocumentObjectGroupPython] N_element013  label="N_element : 0.121"  # scripted group (container) (typed FeaturePython)
  n = 0.121276
FEATURE [App::DocumentObjectGroupPython] O_element028  label="O_element : 0.578"  # scripted group (container) (typed FeaturePython)
  n = 0.578212
FEATURE [App::DocumentObjectGroupPython] G4_CELLULOSE_NITRATE  # scripted group (container) (typed FeaturePython)
  Dunit = g/cm3
  Dvalue = 1.49
  Group = -> [H_element023,C_element027,N_element013,O_element028]
  conduct = 2
  density = 1
  expand = 3
  formula = G4_CELLULOSE_NITRATE
  name = G4_CELLULOSE_NITRATE
  specific = 4
FEATURE [App::DocumentObjectGroupPython] H_element024  label="H_element : 0.108"  # scripted group (container) (typed FeaturePython)
  n = 0.107596
FEATURE [App::DocumentObjectGroupPython] N_element014  label="N_element : 0.001"  # scripted group (container) (typed FeaturePython)
  n = 0.0008
FEATURE [App::DocumentObjectGroupPython] O_element029  label="O_element : 0.875"  # scripted group (container) (typed FeaturePython)
  n = 0.874976
FEATURE [App::DocumentObjectGroupPython] S_element008  label="S_element : 0.015"  # scripted group (container) (typed FeaturePython)
  n = 0.014627
FEATURE [App::DocumentObjectGroupPython] Ce_element001  label="Ce_element : 0.002"  # scripted group (container) (typed FeaturePython)
  n = 0.002001
FEATURE [App::DocumentObjectGroupPython] G4_CERIC_SULFATE  # scripted group (container) (typed FeaturePython)
  Dunit = g/cm3
  Dvalue = 1.03
  Group = -> [H_element024,N_element014,O_element029,S_element008,Ce_element001]
  conduct = 2
  density = 1
  expand = 3
  formula = G4_CERIC_SULFATE
  name = G4_CERIC_SULFATE
  specific = 4
FEATURE [App::DocumentObjectGroupPython] Cs_element001  label="Cs_element : 1"  # scripted group (container) (typed FeaturePython)
  n = 1
  ref = Cs_element
FEATURE [App::DocumentObjectGroupPython] F_element006  label="F_element : 1"  # scripted group (container) (typed FeaturePython)
  n = 1
  ref = F_element
FEATURE [App::DocumentObjectGroupPython] G4_CESIUM_FLUORIDE  # scripted group (container) (typed FeaturePython)
  Dunit = g/cm3
  Dvalue = 4.115
  Group = -> [Cs_element001,F_element006]
  conduct = 2
  density = 1
  expand = 3
  formula = G4_CESIUM_FLUORIDE
  name = G4_CESIUM_FLUORIDE
  specific = 4
FEATURE [App::DocumentObjectGroupPython] Cs_element002  label="Cs_element : 002"  # scripted group (container) (typed FeaturePython)
  n = 1
  ref = Cs_element
FEATURE [App::DocumentObjectGroupPython] I_element001  label="I_element : 1"  # scripted group (container) (typed FeaturePython)
  n = 1
  ref = I_element
FEATURE [App::DocumentObjectGroupPython] G4_CESIUM_IODIDE001  label="G4_CESIUM_IODIDE"  # scripted group (container) (typed FeaturePython)
  Dunit = g/cm3
  Dvalue = 4.51
  Group = -> [Cs_element002,I_element001]
  conduct = 2
  density = 1
  expand = 3
  formula = G4_CESIUM_IODIDE
  name = G4_CESIUM_IODIDE
  specific = 4
FEATURE [App::DocumentObjectGroupPython] C_element028  label="C_element : 013"  # scripted group (container) (typed FeaturePython)
  n = 6
  ref = C_element
FEATURE [App::DocumentObjectGroupPython] H_element025  label="H_element : 013"  # scripted group (container) (typed FeaturePython)
  n = 5
  ref = H_element
FEATURE [App::DocumentObjectGroupPython] Cl_element005  label="Cl_element : 1"  # scripted group (container) (typed FeaturePython)
  n = 1
  ref = Cl_element
FEATURE [App::DocumentObjectGroupPython] G4_CHLOROBENZENE  # scripted group (container) (typed FeaturePython)
  Dunit = g/cm3
  Dvalue = 1.1058
  Group = -> [C_element028,H_element025,Cl_element005]
  conduct = 2
  density = 1
  expand = 3
  formula = G4_CHLOROBENZENE
  name = G4_CHLOROBENZENE
  specific = 4
FEATURE [App::DocumentObjectGroupPython] C_element029  label="C_element : 014"  # scripted group (container) (typed FeaturePython)
  n = 1
  ref = C_element
FEATURE [App::DocumentObjectGroupPython] H_element026  label="H_element : 1"  # scripted group (container) (typed FeaturePython)
  n = 1
  ref = H_element
FEATURE [App::DocumentObjectGroupPython] Cl_element006  label="Cl_element : 3"  # scripted group (container) (typed FeaturePython)
  n = 3
  ref = Cl_element
FEATURE [App::DocumentObjectGroupPython] G4_CHLOROFORM  # scripted group (container) (typed FeaturePython)
  Dunit = g/cm3
  Dvalue = 1.4832
  Group = -> [C_element029,H_element026,Cl_element006]
  conduct = 2
  density = 1
  expand = 3
  formula = G4_CHLOROFORM
  name = G4_CHLOROFORM
  specific = 4
FEATURE [App::DocumentObjectGroupPython] H_element027  label="H_element : 0.010"  # scripted group (container) (typed FeaturePython)
  n = 0.01
FEATURE [App::DocumentObjectGroupPython] C_element030  label="C_element : 0.001"  # scripted group (container) (typed FeaturePython)
  n = 0.001
FEATURE [App::DocumentObjectGroupPython] O_element030  label="O_element : 0.529"  # scripted group (container) (typed FeaturePython)
  n = 0.529107
FEATURE [App::DocumentObjectGroupPython] Na_element005  label="Na_element : 0.016"  # scripted group (container) (typed FeaturePython)
  n = 0.016
FEATURE [App::DocumentObjectGroupPython] Mg_element003  label="Mg_element : 0.004"  # scripted group (container) (typed FeaturePython)
  n = 0.002
FEATURE [App::DocumentObjectGroupPython] Al_element002  label="Al_element : 0.034"  # scripted group (container) (typed FeaturePython)
  n = 0.033872
FEATURE [App::DocumentObjectGroupPython] Si_element002  label="Si_element : 0.337"  # scripted group (container) (typed FeaturePython)
  n = 0.337021
FEATURE [App::DocumentObjectGroupPython] K_element003  label="K_element : 0.013"  # scripted group (container) (typed FeaturePython)
  n = 0.013
FEATURE [App::DocumentObjectGroupPython] Ca_element010  label="Ca_element : 0.044"  # scripted group (container) (typed FeaturePython)
  n = 0.044
FEATURE [App::DocumentObjectGroupPython] Fe_element002  label="Fe_element : 0.014"  # scripted group (container) (typed FeaturePython)
  n = 0.014
FEATURE [App::DocumentObjectGroupPython] G4_CONCRETE  # scripted group (container) (typed FeaturePython)
  Dunit = g/cm3
  Dvalue = 2.3
  Group = -> [H_element027,C_element030,O_element030,Na_element005,Mg_element003,Al_element002,Si_element002,K_element003,Ca_element010,Fe_element002]
  conduct = 2
  density = 1
  expand = 3
  formula = G4_CONCRETE
  name = G4_CONCRETE
  specific = 4
FEATURE [App::DocumentObjectGroupPython] C_element031  label="C_element : 015"  # scripted group (container) (typed FeaturePython)
  n = 6
  ref = C_element
FEATURE [App::DocumentObjectGroupPython] H_element028  label="H_element : 12"  # scripted group (container) (typed FeaturePython)
  n = 12
  ref = H_element
FEATURE [App::DocumentObjectGroupPython] G4_CYCLOHEXANE  # scripted group (container) (typed FeaturePython)
  Dunit = g/cm3
  Dvalue = 0.779
  Group = -> [C_element031,H_element028]
  conduct = 2
  density = 1
  expand = 3
  formula = G4_CYCLOHEXANE
  name = G4_CYCLOHEXANE
  specific = 4
FEATURE [App::DocumentObjectGroupPython] C_element032  label="C_element : 016"  # scripted group (container) (typed FeaturePython)
  n = 6
  ref = C_element
FEATURE [App::DocumentObjectGroupPython] H_element029  label="H_element : 4"  # scripted group (container) (typed FeaturePython)
  n = 4
  ref = H_element
FEATURE [App::DocumentObjectGroupPython] Cl_element007  label="Cl_element : 2"  # scripted group (container) (typed FeaturePython)
  n = 2
  ref = Cl_element
FEATURE [App::DocumentObjectGroupPython] G4_1_2_DICHLOROBENZENE  label="G4_1.2-DICHLOROBENZENE"  # scripted group (container) (typed FeaturePython)
  Dunit = g/cm3
  Dvalue = 1.3048
  Group = -> [C_element032,H_element029,Cl_element007]
  conduct = 2
  density = 1
  expand = 3
  formula = G4_1.2-DICHLOROBENZENE
  name = G4_1.2-DICHLOROBENZENE
  specific = 4
FEATURE [App::DocumentObjectGroupPython] C_element033  label="C_element : 017"  # scripted group (container) (typed FeaturePython)
  n = 4
  ref = C_element
FEATURE [App::DocumentObjectGroupPython] H_element030  label="H_element : 8"  # scripted group (container) (typed FeaturePython)
  n = 8
  ref = H_element
FEATURE [App::DocumentObjectGroupPython] O_element031  label="O_element : 014"  # scripted group (container) (typed FeaturePython)
  n = 1
  ref = O_element
FEATURE [App::DocumentObjectGroupPython] Cl_element008  label="Cl_element : 005"  # scripted group (container) (typed FeaturePython)
  n = 2
  ref = Cl_element
FEATURE [App::DocumentObjectGroupPython] G4_DICHLORODIETHYL_ETHER  # scripted group (container) (typed FeaturePython)
  Dunit = g/cm3
  Dvalue = 1.2199
  Group = -> [C_element033,H_element030,O_element031,Cl_element008]
  conduct = 2
  density = 1
  expand = 3
  formula = G4_DICHLORODIETHYL_ETHER
  name = G4_DICHLORODIETHYL_ETHER
  specific = 4
FEATURE [App::DocumentObjectGroupPython] C_element034  label="C_element : 018"  # scripted group (container) (typed FeaturePython)
  n = 2
  ref = C_element
FEATURE [App::DocumentObjectGroupPython] H_element031  label="H_element : 014"  # scripted group (container) (typed FeaturePython)
  n = 4
  ref = H_element
FEATURE [App::DocumentObjectGroupPython] Cl_element009  label="Cl_element : 006"  # scripted group (container) (typed FeaturePython)
  n = 2
  ref = Cl_element
FEATURE [App::DocumentObjectGroupPython] G4_1_2_DICHLOROETHANE  label="G4_1.2-DICHLOROETHANE"  # scripted group (container) (typed FeaturePython)
  Dunit = g/cm3
  Dvalue = 1.2351
  Group = -> [C_element034,H_element031,Cl_element009]
  conduct = 2
  density = 1
  expand = 3
  formula = G4_1.2-DICHLOROETHANE
  name = G4_1.2-DICHLOROETHANE
  specific = 4
FEATURE [App::DocumentObjectGroupPython] C_element035  label="C_element : 019"  # scripted group (container) (typed FeaturePython)
  n = 4
  ref = C_element
FEATURE [App::DocumentObjectGroupPython] H_element032  label="H_element : 015"  # scripted group (container) (typed FeaturePython)
  n = 10
  ref = H_element
FEATURE [App::DocumentObjectGroupPython] O_element032  label="O_element : 015"  # scripted group (container) (typed FeaturePython)
  n = 1
  ref = O_element
FEATURE [App::DocumentObjectGroupPython] G4_DIETHYL_ETHER  # scripted group (container) (typed FeaturePython)
  Dunit = g/cm3
  Dvalue = 0.71378
  Group = -> [C_element035,H_element032,O_element032]
  conduct = 2
  density = 1
  expand = 3
  formula = G4_DIETHYL_ETHER
  name = G4_DIETHYL_ETHER
  specific = 4
FEATURE [App::DocumentObjectGroupPython] C_element036  label="C_element : 020"  # scripted group (container) (typed FeaturePython)
  n = 3
  ref = C_element
FEATURE [App::DocumentObjectGroupPython] H_element033  label="H_element : 016"  # scripted group (container) (typed FeaturePython)
  n = 7
  ref = H_element
FEATURE [App::DocumentObjectGroupPython] N_element015  label="N_element : 008"  # scripted group (container) (typed FeaturePython)
  n = 1
  ref = N_element
FEATURE [App::DocumentObjectGroupPython] O_element033  label="O_element : 016"  # scripted group (container) (typed FeaturePython)
  n = 1
  ref = O_element
FEATURE [App::DocumentObjectGroupPython] G4_N_N_DIMETHYL_FORMAMIDE  label="G4_N.N-DIMETHYL_FORMAMIDE"  # scripted group (container) (typed FeaturePython)
  Dunit = g/cm3
  Dvalue = 0.9487
  Group = -> [C_element036,H_element033,N_element015,O_element033]
  conduct = 2
  density = 1
  expand = 3
  formula = G4_N.N-DIMETHYL_FORMAMIDE
  name = G4_N.N-DIMETHYL_FORMAMIDE
  specific = 4
FEATURE [App::DocumentObjectGroupPython] C_element037  label="C_element : 021"  # scripted group (container) (typed FeaturePython)
  n = 2
  ref = C_element
FEATURE [App::DocumentObjectGroupPython] H_element034  label="H_element : 017"  # scripted group (container) (typed FeaturePython)
  n = 6
  ref = H_element
FEATURE [App::DocumentObjectGroupPython] O_element034  label="O_element : 017"  # scripted group (container) (typed FeaturePython)
  n = 1
  ref = O_element
FEATURE [App::DocumentObjectGroupPython] S_element009  label="S_element : 003"  # scripted group (container) (typed FeaturePython)
  n = 1
  ref = S_element
FEATURE [App::DocumentObjectGroupPython] G4_DIMETHYL_SULFOXIDE  # scripted group (container) (typed FeaturePython)
  Dunit = g/cm3
  Dvalue = 1.1014
  Group = -> [C_element037,H_element034,O_element034,S_element009]
  conduct = 2
  density = 1
  expand = 3
  formula = G4_DIMETHYL_SULFOXIDE
  name = G4_DIMETHYL_SULFOXIDE
  specific = 4
FEATURE [App::DocumentObjectGroupPython] C_element038  label="C_element : 022"  # scripted group (container) (typed FeaturePython)
  n = 2
  ref = C_element
FEATURE [App::DocumentObjectGroupPython] H_element035  label="H_element : 018"  # scripted group (container) (typed FeaturePython)
  n = 6
  ref = H_element
FEATURE [App::DocumentObjectGroupPython] G4_ETHANE  # scripted group (container) (typed FeaturePython)
  Dunit = g/cm3
  Dvalue = 0.00125324
  Group = -> [C_element038,H_element035]
  conduct = 2
  density = 1
  expand = 3
  formula = G4_ETHANE
  name = G4_ETHANE
  specific = 4
FEATURE [App::DocumentObjectGroupPython] C_element039  label="C_element : 023"  # scripted group (container) (typed FeaturePython)
  n = 2
  ref = C_element
FEATURE [App::DocumentObjectGroupPython] H_element036  label="H_element : 019"  # scripted group (container) (typed FeaturePython)
  n = 6
  ref = H_element
FEATURE [App::DocumentObjectGroupPython] O_element035  label="O_element : 018"  # scripted group (container) (typed FeaturePython)
  n = 1
  ref = O_element
FEATURE [App::DocumentObjectGroupPython] G4_ETHYL_ALCOHOL  # scripted group (container) (typed FeaturePython)
  Dunit = g/cm3
  Dvalue = 0.7893
  Group = -> [C_element039,H_element036,O_element035]
  conduct = 2
  density = 1
  expand = 3
  formula = G4_ETHYL_ALCOHOL
  name = G4_ETHYL_ALCOHOL
  specific = 4
FEATURE [App::DocumentObjectGroupPython] H_element037  label="H_element : 0.090"  # scripted group (container) (typed FeaturePython)
  n = 0.090027
FEATURE [App::DocumentObjectGroupPython] C_element040  label="C_element : 0.585"  # scripted group (container) (typed FeaturePython)
  n = 0.585182
FEATURE [App::DocumentObjectGroupPython] O_element036  label="O_element : 0.325"  # scripted group (container) (typed FeaturePython)
  n = 0.324791
FEATURE [App::DocumentObjectGroupPython] G4_ETHYL_CELLULOSE  # scripted group (container) (typed FeaturePython)
  Dunit = g/cm3
  Dvalue = 1.13
  Group = -> [H_element037,C_element040,O_element036]
  conduct = 2
  density = 1
  expand = 3
  formula = G4_ETHYL_CELLULOSE
  name = G4_ETHYL_CELLULOSE
  specific = 4
FEATURE [App::DocumentObjectGroupPython] C_element041  label="C_element : 024"  # scripted group (container) (typed FeaturePython)
  n = 2
  ref = C_element
FEATURE [App::DocumentObjectGroupPython] H_element038  label="H_element : 020"  # scripted group (container) (typed FeaturePython)
  n = 4
  ref = H_element
FEATURE [App::DocumentObjectGroupPython] G4_ETHYLENE  # scripted group (container) (typed FeaturePython)
  Dunit = g/cm3
  Dvalue = 0.00117497
  Group = -> [C_element041,H_element038]
  conduct = 2
  density = 1
  expand = 3
  formula = G4_ETHYLENE
  name = G4_ETHYLENE
  specific = 4
FEATURE [App::DocumentObjectGroupPython] H_element039  label="H_element : 0.096"  # scripted group (container) (typed FeaturePython)
  n = 0.096
FEATURE [App::DocumentObjectGroupPython] C_element042  label="C_element : 0.195"  # scripted group (container) (typed FeaturePython)
  n = 0.195
FEATURE [App::DocumentObjectGroupPython] N_element016  label="N_element : 0.057"  # scripted group (container) (typed FeaturePython)
  n = 0.057
FEATURE [App::DocumentObjectGroupPython] O_element037  label="O_element : 0.646"  # scripted group (container) (typed FeaturePython)
  n = 0.646
FEATURE [App::DocumentObjectGroupPython] Na_element006  label="Na_element : 0.017"  # scripted group (container) (typed FeaturePython)
  n = 0.001
FEATURE [App::DocumentObjectGroupPython] P_element005  label="P_element : 0.104"  # scripted group (container) (typed FeaturePython)
  n = 0.001
FEATURE [App::DocumentObjectGroupPython] S_element010  label="S_element : 0.016"  # scripted group (container) (typed FeaturePython)
  n = 0.003
FEATURE [App::DocumentObjectGroupPython] Cl_element010  label="Cl_element : 0.005"  # scripted group (container) (typed FeaturePython)
  n = 0.001
FEATURE [App::DocumentObjectGroupPython] G4_EYE_LENS_ICRP  # scripted group (container) (typed FeaturePython)
  Dunit = g/cm3
  Dvalue = 1.07
  Group = -> [H_element039,C_element042,N_element016,O_element037,Na_element006,P_element005,S_element010,Cl_element010]
  conduct = 2
  density = 1
  expand = 3
  formula = G4_EYE_LENS_ICRP
  name = G4_EYE_LENS_ICRP
  specific = 4
FEATURE [App::DocumentObjectGroupPython] Fe_element003  label="Fe_element : 2"  # scripted group (container) (typed FeaturePython)
  n = 2
  ref = Fe_element
FEATURE [App::DocumentObjectGroupPython] O_element038  label="O_element : 019"  # scripted group (container) (typed FeaturePython)
  n = 3
  ref = O_element
FEATURE [App::DocumentObjectGroupPython] G4_FERRIC_OXIDE  # scripted group (container) (typed FeaturePython)
  Dunit = g/cm3
  Dvalue = 5.2
  Group = -> [Fe_element003,O_element038]
  conduct = 2
  density = 1
  expand = 3
  formula = G4_FERRIC_OXIDE
  name = G4_FERRIC_OXIDE
  specific = 4
FEATURE [App::DocumentObjectGroupPython] Fe_element004  label="Fe_element : 1"  # scripted group (container) (typed FeaturePython)
  n = 1
  ref = Fe_element
FEATURE [App::DocumentObjectGroupPython] B_element003  label="B_element : 1"  # scripted group (container) (typed FeaturePython)
  n = 1
  ref = B_element
FEATURE [App::DocumentObjectGroupPython] G4_FERROBORIDE  # scripted group (container) (typed FeaturePython)
  Dunit = g/cm3
  Dvalue = 7.15
  Group = -> [Fe_element004,B_element003]
  conduct = 2
  density = 1
  expand = 3
  formula = G4_FERROBORIDE
  name = G4_FERROBORIDE
  specific = 4
FEATURE [App::DocumentObjectGroupPython] Fe_element005  label="Fe_element : 003"  # scripted group (container) (typed FeaturePython)
  n = 1
  ref = Fe_element
FEATURE [App::DocumentObjectGroupPython] O_element039  label="O_element : 020"  # scripted group (container) (typed FeaturePython)
  n = 1
  ref = O_element
FEATURE [App::DocumentObjectGroupPython] G4_FERROUS_OXIDE  # scripted group (container) (typed FeaturePython)
  Dunit = g/cm3
  Dvalue = 5.7
  Group = -> [Fe_element005,O_element039]
  conduct = 2
  density = 1
  expand = 3
  formula = G4_FERROUS_OXIDE
  name = G4_FERROUS_OXIDE
  specific = 4
FEATURE [App::DocumentObjectGroupPython] H_element040  label="H_element : 0.115"  # scripted group (container) (typed FeaturePython)
  n = 0.108259
FEATURE [App::DocumentObjectGroupPython] N_element017  label="N_element : 0.000"  # scripted group (container) (typed FeaturePython)
  n = 2.7e-05
FEATURE [App::DocumentObjectGroupPython] O_element040  label="O_element : 0.879"  # scripted group (container) (typed FeaturePython)
  n = 0.878636
FEATURE [App::DocumentObjectGroupPython] Na_element007  label="Na_element : 0.000"  # scripted group (container) (typed FeaturePython)
  n = 2.2e-05
FEATURE [App::DocumentObjectGroupPython] S_element011  label="S_element : 0.013"  # scripted group (container) (typed FeaturePython)
  n = 0.012968
FEATURE [App::DocumentObjectGroupPython] Cl_element011  label="Cl_element : 0.000"  # scripted group (container) (typed FeaturePython)
  n = 3.4e-05
FEATURE [App::DocumentObjectGroupPython] Fe_element006  label="Fe_element : 0.000"  # scripted group (container) (typed FeaturePython)
  n = 5.4e-05
FEATURE [App::DocumentObjectGroupPython] G4_FERROUS_SULFATE  # scripted group (container) (typed FeaturePython)
  Dunit = g/cm3
  Dvalue = 1.024
  Group = -> [H_element040,N_element017,O_element040,Na_element007,S_element011,Cl_element011,Fe_element006]
  conduct = 2
  density = 1
  expand = 3
  formula = G4_FERROUS_SULFATE
  name = G4_FERROUS_SULFATE
  specific = 4
FEATURE [App::DocumentObjectGroupPython] C_element043  label="C_element : 0.099"  # scripted group (container) (typed FeaturePython)
  n = 0.099335
FEATURE [App::DocumentObjectGroupPython] F_element007  label="F_element : 0.314"  # scripted group (container) (typed FeaturePython)
  n = 0.314247
FEATURE [App::DocumentObjectGroupPython] Cl_element012  label="Cl_element : 0.586"  # scripted group (container) (typed FeaturePython)
  n = 0.586418
FEATURE [App::DocumentObjectGroupPython] G4_FREON_12  label="G4_FREON-12"  # scripted group (container) (typed FeaturePython)
  Dunit = g/cm3
  Dvalue = 1.12
  Group = -> [C_element043,F_element007,Cl_element012]
  conduct = 2
  density = 1
  expand = 3
  formula = G4_FREON-12
  name = G4_FREON-12
  specific = 4
FEATURE [App::DocumentObjectGroupPython] C_element044  label="C_element : 0.057"  # scripted group (container) (typed FeaturePython)
  n = 0.057245
FEATURE [App::DocumentObjectGroupPython] F_element008  label="F_element : 0.181"  # scripted group (container) (typed FeaturePython)
  n = 0.181096
FEATURE [App::DocumentObjectGroupPython] Br_element001  label="Br_element : 0.762"  # scripted group (container) (typed FeaturePython)
  n = 0.761659
FEATURE [App::DocumentObjectGroupPython] G4_FREON_12B2  label="G4_FREON-12B2"  # scripted group (container) (typed FeaturePython)
  Dunit = g/cm3
  Dvalue = 1.8
  Group = -> [C_element044,F_element008,Br_element001]
  conduct = 2
  density = 1
  expand = 3
  formula = G4_FREON-12B2
  name = G4_FREON-12B2
  specific = 4
FEATURE [App::DocumentObjectGroupPython] C_element045  label="C_element : 0.115"  # scripted group (container) (typed FeaturePython)
  n = 0.114983
FEATURE [App::DocumentObjectGroupPython] F_element009  label="F_element : 0.546"  # scripted group (container) (typed FeaturePython)
  n = 0.545621
FEATURE [App::DocumentObjectGroupPython] Cl_element013  label="Cl_element : 0.339"  # scripted group (container) (typed FeaturePython)
  n = 0.339396
FEATURE [App::DocumentObjectGroupPython] G4_FREON_13  label="G4_FREON-13"  # scripted group (container) (typed FeaturePython)
  Dunit = g/cm3
  Dvalue = 0.95
  Group = -> [C_element045,F_element009,Cl_element013]
  conduct = 2
  density = 1
  expand = 3
  formula = G4_FREON-13
  name = G4_FREON-13
  specific = 4
FEATURE [App::DocumentObjectGroupPython] C_element046  label="C_element : 025"  # scripted group (container) (typed FeaturePython)
  n = 1
  ref = C_element
FEATURE [App::DocumentObjectGroupPython] F_element010  label="F_element : 3"  # scripted group (container) (typed FeaturePython)
  n = 3
  ref = F_element
FEATURE [App::DocumentObjectGroupPython] Br_element002  label="Br_element : 1"  # scripted group (container) (typed FeaturePython)
  n = 1
  ref = Br_element
FEATURE [App::DocumentObjectGroupPython] G4_FREON_13B1  label="G4_FREON-13B1"  # scripted group (container) (typed FeaturePython)
  Dunit = g/cm3
  Dvalue = 1.5
  Group = -> [C_element046,F_element010,Br_element002]
  conduct = 2
  density = 1
  expand = 3
  formula = G4_FREON-13B1
  name = G4_FREON-13B1
  specific = 4
FEATURE [App::DocumentObjectGroupPython] C_element047  label="C_element : 0.061"  # scripted group (container) (typed FeaturePython)
  n = 0.061309
FEATURE [App::DocumentObjectGroupPython] F_element011  label="F_element : 0.291"  # scripted group (container) (typed FeaturePython)
  n = 0.290924
FEATURE [App::DocumentObjectGroupPython] I_element002  label="I_element : 0.648"  # scripted group (container) (typed FeaturePython)
  n = 0.647767
FEATURE [App::DocumentObjectGroupPython] G4_FREON_13I1  label="G4_FREON-13I1"  # scripted group (container) (typed FeaturePython)
  Dunit = g/cm3
  Dvalue = 1.8
  Group = -> [C_element047,F_element011,I_element002]
  conduct = 2
  density = 1
  expand = 3
  formula = G4_FREON-13I1
  name = G4_FREON-13I1
  specific = 4
FEATURE [App::DocumentObjectGroupPython] Gd_element001  label="Gd_element : 2"  # scripted group (container) (typed FeaturePython)
  n = 2
  ref = Gd_element
FEATURE [App::DocumentObjectGroupPython] O_element041  label="O_element : 021"  # scripted group (container) (typed FeaturePython)
  n = 2
  ref = O_element
FEATURE [App::DocumentObjectGroupPython] S_element012  label="S_element : 004"  # scripted group (container) (typed FeaturePython)
  n = 1
  ref = S_element
FEATURE [App::DocumentObjectGroupPython] G4_GADOLINIUM_OXYSULFIDE  # scripted group (container) (typed FeaturePython)
  Dunit = g/cm3
  Dvalue = 7.44
  Group = -> [Gd_element001,O_element041,S_element012]
  conduct = 2
  density = 1
  expand = 3
  formula = G4_GADOLINIUM_OXYSULFIDE
  name = G4_GADOLINIUM_OXYSULFIDE
  specific = 4
FEATURE [App::DocumentObjectGroupPython] Ga_element001  label="Ga_element : 1"  # scripted group (container) (typed FeaturePython)
  n = 1
  ref = Ga_element
FEATURE [App::DocumentObjectGroupPython] As_element001  label="As_element : 1"  # scripted group (container) (typed FeaturePython)
  n = 1
  ref = As_element
FEATURE [App::DocumentObjectGroupPython] G4_GALLIUM_ARSENIDE  # scripted group (container) (typed FeaturePython)
  Dunit = g/cm3
  Dvalue = 5.31
  Group = -> [Ga_element001,As_element001]
  conduct = 2
  density = 1
  expand = 3
  formula = G4_GALLIUM_ARSENIDE
  name = G4_GALLIUM_ARSENIDE
  specific = 4
FEATURE [App::DocumentObjectGroupPython] H_element041  label="H_element : 0.081"  # scripted group (container) (typed FeaturePython)
  n = 0.08118
FEATURE [App::DocumentObjectGroupPython] C_element048  label="C_element : 0.416"  # scripted group (container) (typed FeaturePython)
  n = 0.41606
FEATURE [App::DocumentObjectGroupPython] N_element018  label="N_element : 0.111"  # scripted group (container) (typed FeaturePython)
  n = 0.11124
FEATURE [App::DocumentObjectGroupPython] O_element042  label="O_element : 0.381"  # scripted group (container) (typed FeaturePython)
  n = 0.38064
FEATURE [App::DocumentObjectGroupPython] S_element013  label="S_element : 0.011"  # scripted group (container) (typed FeaturePython)
  n = 0.01088
FEATURE [App::DocumentObjectGroupPython] G4_GEL_PHOTO_EMULSION  # scripted group (container) (typed FeaturePython)
  Dunit = g/cm3
  Dvalue = 1.2914
  Group = -> [H_element041,C_element048,N_element018,O_element042,S_element013]
  conduct = 2
  density = 1
  expand = 3
  formula = G4_GEL_PHOTO_EMULSION
  name = G4_GEL_PHOTO_EMULSION
  specific = 4
FEATURE [App::DocumentObjectGroupPython] B_element004  label="B_element : 0.040"  # scripted group (container) (typed FeaturePython)
  n = 0.0400639
FEATURE [App::DocumentObjectGroupPython] O_element043  label="O_element : 0.540"  # scripted group (container) (typed FeaturePython)
  n = 0.539561
FEATURE [App::DocumentObjectGroupPython] Na_element008  label="Na_element : 0.028"  # scripted group (container) (typed FeaturePython)
  n = 0.0281909
FEATURE [App::DocumentObjectGroupPython] Al_element003  label="Al_element : 0.012"  # scripted group (container) (typed FeaturePython)
  n = 0.011644
FEATURE [App::DocumentObjectGroupPython] Si_element003  label="Si_element : 0.377"  # scripted group (container) (typed FeaturePython)
  n = 0.377219
FEATURE [App::DocumentObjectGroupPython] K_element004  label="K_element : 0.014"  # scripted group (container) (typed FeaturePython)
  n = 0.00332099
FEATURE [App::DocumentObjectGroupPython] G4_Pyrex_Glass  # scripted group (container) (typed FeaturePython)
  Dunit = g/cm3
  Dvalue = 2.23
  Group = -> [B_element004,O_element043,Na_element008,Al_element003,Si_element003,K_element004]
  conduct = 2
  density = 1
  expand = 3
  formula = G4_Pyrex_Glass
  name = G4_Pyrex_Glass
  specific = 4
FEATURE [App::DocumentObjectGroupPython] O_element044  label="O_element : 0.156"  # scripted group (container) (typed FeaturePython)
  n = 0.156453
FEATURE [App::DocumentObjectGroupPython] Si_element004  label="Si_element : 0.081"  # scripted group (container) (typed FeaturePython)
  n = 0.080866
FEATURE [App::DocumentObjectGroupPython] Ti_element001  label="Ti_element : 0.008"  # scripted group (container) (typed FeaturePython)
  n = 0.008092
FEATURE [App::DocumentObjectGroupPython] As_element002  label="As_element : 0.003"  # scripted group (container) (typed FeaturePython)
  n = 0.002651
FEATURE [App::DocumentObjectGroupPython] Pb_element001  label="Pb_element : 0.752"  # scripted group (container) (typed FeaturePython)
  n = 0.751938
FEATURE [App::DocumentObjectGroupPython] G4_GLASS_LEAD  # scripted group (container) (typed FeaturePython)
  Dunit = g/cm3
  Dvalue = 6.22
  Group = -> [O_element044,Si_element004,Ti_element001,As_element002,Pb_element001]
  conduct = 2
  density = 1
  expand = 3
  formula = G4_GLASS_LEAD
  name = G4_GLASS_LEAD
  specific = 4
FEATURE [App::DocumentObjectGroupPython] O_element045  label="O_element : 0.460"  # scripted group (container) (typed FeaturePython)
  n = 0.4598
FEATURE [App::DocumentObjectGroupPython] Na_element009  label="Na_element : 0.096"  # scripted group (container) (typed FeaturePython)
  n = 0.0964411
FEATURE [App::DocumentObjectGroupPython] Si_element005  label="Si_element : 0.378"  # scripted group (container) (typed FeaturePython)
  n = 0.336553
FEATURE [App::DocumentObjectGroupPython] Ca_element011  label="Ca_element : 0.107"  # scripted group (container) (typed FeaturePython)
  n = 0.107205
FEATURE [App::DocumentObjectGroupPython] G4_GLASS_PLATE  # scripted group (container) (typed FeaturePython)
  Dunit = g/cm3
  Dvalue = 2.4
  Group = -> [O_element045,Na_element009,Si_element005,Ca_element011]
  conduct = 2
  density = 1
  expand = 3
  formula = G4_GLASS_PLATE
  name = G4_GLASS_PLATE
  specific = 4
FEATURE [App::DocumentObjectGroupPython] C_element049  label="C_element : 026"  # scripted group (container) (typed FeaturePython)
  n = 5
  ref = C_element
FEATURE [App::DocumentObjectGroupPython] H_element042  label="H_element : 021"  # scripted group (container) (typed FeaturePython)
  n = 10
  ref = H_element
FEATURE [App::DocumentObjectGroupPython] N_element019  label="N_element : 2"  # scripted group (container) (typed FeaturePython)
  n = 2
  ref = N_element
FEATURE [App::DocumentObjectGroupPython] O_element046  label="O_element : 022"  # scripted group (container) (typed FeaturePython)
  n = 3
  ref = O_element
FEATURE [App::DocumentObjectGroupPython] G4_GLUTAMINE  # scripted group (container) (typed FeaturePython)
  Dunit = g/cm3
  Dvalue = 1.46
  Group = -> [C_element049,H_element042,N_element019,O_element046]
  conduct = 2
  density = 1
  expand = 3
  formula = G4_GLUTAMINE
  name = G4_GLUTAMINE
  specific = 4
FEATURE [App::DocumentObjectGroupPython] C_element050  label="C_element : 027"  # scripted group (container) (typed FeaturePython)
  n = 3
  ref = C_element
FEATURE [App::DocumentObjectGroupPython] H_element043  label="H_element : 022"  # scripted group (container) (typed FeaturePython)
  n = 8
  ref = H_element
FEATURE [App::DocumentObjectGroupPython] O_element047  label="O_element : 023"  # scripted group (container) (typed FeaturePython)
  n = 3
  ref = O_element
FEATURE [App::DocumentObjectGroupPython] G4_GLYCEROL  # scripted group (container) (typed FeaturePython)
  Dunit = g/cm3
  Dvalue = 1.2613
  Group = -> [C_element050,H_element043,O_element047]
  conduct = 2
  density = 1
  expand = 3
  formula = G4_GLYCEROL
  name = G4_GLYCEROL
  specific = 4
FEATURE [App::DocumentObjectGroupPython] C_element051  label="C_element : 028"  # scripted group (container) (typed FeaturePython)
  n = 5
  ref = C_element
FEATURE [App::DocumentObjectGroupPython] H_element044  label="H_element : 023"  # scripted group (container) (typed FeaturePython)
  n = 5
  ref = H_element
FEATURE [App::DocumentObjectGroupPython] N_element020  label="N_element : 009"  # scripted group (container) (typed FeaturePython)
  n = 5
  ref = N_element
FEATURE [App::DocumentObjectGroupPython] O_element048  label="O_element : 024"  # scripted group (container) (typed FeaturePython)
  n = 1
  ref = O_element
FEATURE [App::DocumentObjectGroupPython] G4_GUANINE  # scripted group (container) (typed FeaturePython)
  Dunit = g/cm3
  Dvalue = 2.2
  Group = -> [C_element051,H_element044,N_element020,O_element048]
  conduct = 2
  density = 1
  expand = 3
  formula = G4_GUANINE
  name = G4_GUANINE
  specific = 4
FEATURE [App::DocumentObjectGroupPython] Ca_element012  label="Ca_element : 006"  # scripted group (container) (typed FeaturePython)
  n = 1
  ref = Ca_element
FEATURE [App::DocumentObjectGroupPython] S_element014  label="S_element : 005"  # scripted group (container) (typed FeaturePython)
  n = 1
  ref = S_element
FEATURE [App::DocumentObjectGroupPython] O_element049  label="O_element : 6"  # scripted group (container) (typed FeaturePython)
  n = 6
  ref = O_element
FEATURE [App::DocumentObjectGroupPython] H_element045  label="H_element : 024"  # scripted group (container) (typed FeaturePython)
  n = 4
  ref = H_element
FEATURE [App::DocumentObjectGroupPython] G4_GYPSUM  # scripted group (container) (typed FeaturePython)
  Dunit = g/cm3
  Dvalue = 2.32
  Group = -> [Ca_element012,S_element014,O_element049,H_element045]
  conduct = 2
  density = 1
  expand = 3
  formula = G4_GYPSUM
  name = G4_GYPSUM
  specific = 4
FEATURE [App::DocumentObjectGroupPython] C_element052  label="C_element : 7"  # scripted group (container) (typed FeaturePython)
  n = 7
  ref = C_element
FEATURE [App::DocumentObjectGroupPython] H_element046  label="H_element : 16"  # scripted group (container) (typed FeaturePython)
  n = 16
  ref = H_element
FEATURE [App::DocumentObjectGroupPython] G4_N_HEPTANE  label="G4_N-HEPTANE"  # scripted group (container) (typed FeaturePython)
  Dunit = g/cm3
  Dvalue = 0.68376
  Group = -> [C_element052,H_element046]
  conduct = 2
  density = 1
  expand = 3
  formula = G4_N-HEPTANE
  name = G4_N-HEPTANE
  specific = 4
FEATURE [App::DocumentObjectGroupPython] C_element053  label="C_element : 029"  # scripted group (container) (typed FeaturePython)
  n = 6
  ref = C_element
FEATURE [App::DocumentObjectGroupPython] H_element047  label="H_element : 14"  # scripted group (container) (typed FeaturePython)
  n = 14
  ref = H_element
FEATURE [App::DocumentObjectGroupPython] G4_N_HEXANE  label="G4_N-HEXANE"  # scripted group (container) (typed FeaturePython)
  Dunit = g/cm3
  Dvalue = 0.6603
  Group = -> [C_element053,H_element047]
  conduct = 2
  density = 1
  expand = 3
  formula = G4_N-HEXANE
  name = G4_N-HEXANE
  specific = 4
FEATURE [App::DocumentObjectGroupPython] C_element054  label="C_element : 22"  # scripted group (container) (typed FeaturePython)
  n = 22
  ref = C_element
FEATURE [App::DocumentObjectGroupPython] H_element048  label="H_element : 025"  # scripted group (container) (typed FeaturePython)
  n = 10
  ref = H_element
FEATURE [App::DocumentObjectGroupPython] N_element021  label="N_element : 010"  # scripted group (container) (typed FeaturePython)
  n = 2
  ref = N_element
FEATURE [App::DocumentObjectGroupPython] O_element050  label="O_element : 025"  # scripted group (container) (typed FeaturePython)
  n = 5
  ref = O_element
FEATURE [App::DocumentObjectGroupPython] G4_KAPTON  # scripted group (container) (typed FeaturePython)
  Dunit = g/cm3
  Dvalue = 1.42
  Group = -> [C_element054,H_element048,N_element021,O_element050]
  conduct = 2
  density = 1
  expand = 3
  formula = G4_KAPTON
  name = G4_KAPTON
  specific = 4
FEATURE [App::DocumentObjectGroupPython] La_element001  label="La_element : 1"  # scripted group (container) (typed FeaturePython)
  n = 1
  ref = La_element
FEATURE [App::DocumentObjectGroupPython] Br_element003  label="Br_element : 002"  # scripted group (container) (typed FeaturePython)
  n = 1
  ref = Br_element
FEATURE [App::DocumentObjectGroupPython] O_element051  label="O_element : 026"  # scripted group (container) (typed FeaturePython)
  n = 1
  ref = O_element
FEATURE [App::DocumentObjectGroupPython] G4_LANTHANUM_OXYBROMIDE  # scripted group (container) (typed FeaturePython)
  Dunit = g/cm3
  Dvalue = 6.28
  Group = -> [La_element001,Br_element003,O_element051]
  conduct = 2
  density = 1
  expand = 3
  formula = G4_LANTHANUM_OXYBROMIDE
  name = G4_LANTHANUM_OXYBROMIDE
  specific = 4
FEATURE [App::DocumentObjectGroupPython] La_element002  label="La_element : 2"  # scripted group (container) (typed FeaturePython)
  n = 2
  ref = La_element
FEATURE [App::DocumentObjectGroupPython] O_element052  label="O_element : 027"  # scripted group (container) (typed FeaturePython)
  n = 2
  ref = O_element
FEATURE [App::DocumentObjectGroupPython] S_element015  label="S_element : 006"  # scripted group (container) (typed FeaturePython)
  n = 1
  ref = S_element
FEATURE [App::DocumentObjectGroupPython] G4_LANTHANUM_OXYSULFIDE  # scripted group (container) (typed FeaturePython)
  Dunit = g/cm3
  Dvalue = 5.86
  Group = -> [La_element002,O_element052,S_element015]
  conduct = 2
  density = 1
  expand = 3
  formula = G4_LANTHANUM_OXYSULFIDE
  name = G4_LANTHANUM_OXYSULFIDE
  specific = 4
FEATURE [App::DocumentObjectGroupPython] O_element053  label="O_element : 0.072"  # scripted group (container) (typed FeaturePython)
  n = 0.071682
FEATURE [App::DocumentObjectGroupPython] Pb_element002  label="Pb_element : 0.928"  # scripted group (container) (typed FeaturePython)
  n = 0.928318
FEATURE [App::DocumentObjectGroupPython] G4_LEAD_OXIDE  # scripted group (container) (typed FeaturePython)
  Dunit = g/cm3
  Dvalue = 9.53
  Group = -> [O_element053,Pb_element002]
  conduct = 2
  density = 1
  expand = 3
  formula = G4_LEAD_OXIDE
  name = G4_LEAD_OXIDE
  specific = 4
FEATURE [App::DocumentObjectGroupPython] Li_element001  label="Li_element : 1"  # scripted group (container) (typed FeaturePython)
  n = 1
  ref = Li_element
FEATURE [App::DocumentObjectGroupPython] N_element022  label="N_element : 011"  # scripted group (container) (typed FeaturePython)
  n = 1
  ref = N_element
FEATURE [App::DocumentObjectGroupPython] H_element049  label="H_element : 026"  # scripted group (container) (typed FeaturePython)
  n = 2
  ref = H_element
FEATURE [App::DocumentObjectGroupPython] G4_LITHIUM_AMIDE  # scripted group (container) (typed FeaturePython)
  Dunit = g/cm3
  Dvalue = 1.178
  Group = -> [Li_element001,N_element022,H_element049]
  conduct = 2
  density = 1
  expand = 3
  formula = G4_LITHIUM_AMIDE
  name = G4_LITHIUM_AMIDE
  specific = 4
FEATURE [App::DocumentObjectGroupPython] Li_element002  label="Li_element : 2"  # scripted group (container) (typed FeaturePython)
  n = 2
  ref = Li_element
FEATURE [App::DocumentObjectGroupPython] C_element055  label="C_element : 030"  # scripted group (container) (typed FeaturePython)
  n = 1
  ref = C_element
FEATURE [App::DocumentObjectGroupPython] O_element054  label="O_element : 028"  # scripted group (container) (typed FeaturePython)
  n = 3
  ref = O_element
FEATURE [App::DocumentObjectGroupPython] G4_LITHIUM_CARBONATE  # scripted group (container) (typed FeaturePython)
  Dunit = g/cm3
  Dvalue = 2.11
  Group = -> [Li_element002,C_element055,O_element054]
  conduct = 2
  density = 1
  expand = 3
  formula = G4_LITHIUM_CARBONATE
  name = G4_LITHIUM_CARBONATE
  specific = 4
FEATURE [App::DocumentObjectGroupPython] Li_element003  label="Li_element : 003"  # scripted group (container) (typed FeaturePython)
  n = 1
  ref = Li_element
FEATURE [App::DocumentObjectGroupPython] F_element012  label="F_element : 004"  # scripted group (container) (typed FeaturePython)
  n = 1
  ref = F_element
FEATURE [App::DocumentObjectGroupPython] G4_LITHIUM_FLUORIDE  # scripted group (container) (typed FeaturePython)
  Dunit = g/cm3
  Dvalue = 2.635
  Group = -> [Li_element003,F_element012]
  conduct = 2
  density = 1
  expand = 3
  formula = G4_LITHIUM_FLUORIDE
  name = G4_LITHIUM_FLUORIDE
  specific = 4
FEATURE [App::DocumentObjectGroupPython] Li_element004  label="Li_element : 004"  # scripted group (container) (typed FeaturePython)
  n = 1
  ref = Li_element
FEATURE [App::DocumentObjectGroupPython] H_element050  label="H_element : 027"  # scripted group (container) (typed FeaturePython)
  n = 1
  ref = H_element
FEATURE [App::DocumentObjectGroupPython] G4_LITHIUM_HYDRIDE  # scripted group (container) (typed FeaturePython)
  Dunit = g/cm3
  Dvalue = 0.82
  Group = -> [Li_element004,H_element050]
  conduct = 2
  density = 1
  expand = 3
  formula = G4_LITHIUM_HYDRIDE
  name = G4_LITHIUM_HYDRIDE
  specific = 4
FEATURE [App::DocumentObjectGroupPython] Li_element005  label="Li_element : 005"  # scripted group (container) (typed FeaturePython)
  n = 1
  ref = Li_element
FEATURE [App::DocumentObjectGroupPython] I_element003  label="I_element : 002"  # scripted group (container) (typed FeaturePython)
  n = 1
  ref = I_element
FEATURE [App::DocumentObjectGroupPython] G4_LITHIUM_IODIDE  # scripted group (container) (typed FeaturePython)
  Dunit = g/cm3
  Dvalue = 3.494
  Group = -> [Li_element005,I_element003]
  conduct = 2
  density = 1
  expand = 3
  formula = G4_LITHIUM_IODIDE
  name = G4_LITHIUM_IODIDE
  specific = 4
FEATURE [App::DocumentObjectGroupPython] Li_element006  label="Li_element : 006"  # scripted group (container) (typed FeaturePython)
  n = 2
  ref = Li_element
FEATURE [App::DocumentObjectGroupPython] O_element055  label="O_element : 029"  # scripted group (container) (typed FeaturePython)
  n = 1
  ref = O_element
FEATURE [App::DocumentObjectGroupPython] G4_LITHIUM_OXIDE  # scripted group (container) (typed FeaturePython)
  Dunit = g/cm3
  Dvalue = 2.013
  Group = -> [Li_element006,O_element055]
  conduct = 2
  density = 1
  expand = 3
  formula = G4_LITHIUM_OXIDE
  name = G4_LITHIUM_OXIDE
  specific = 4
FEATURE [App::DocumentObjectGroupPython] Li_element007  label="Li_element : 007"  # scripted group (container) (typed FeaturePython)
  n = 2
  ref = Li_element
FEATURE [App::DocumentObjectGroupPython] B_element005  label="B_element : 005"  # scripted group (container) (typed FeaturePython)
  n = 4
  ref = B_element
FEATURE [App::DocumentObjectGroupPython] O_element056  label="O_element : 7"  # scripted group (container) (typed FeaturePython)
  n = 7
  ref = O_element
FEATURE [App::DocumentObjectGroupPython] G4_LITHIUM_TETRABORATE  # scripted group (container) (typed FeaturePython)
  Dunit = g/cm3
  Dvalue = 2.44
  Group = -> [Li_element007,B_element005,O_element056]
  conduct = 2
  density = 1
  expand = 3
  formula = G4_LITHIUM_TETRABORATE
  name = G4_LITHIUM_TETRABORATE
  specific = 4
FEATURE [App::DocumentObjectGroupPython] H_element051  label="H_element : 0.105"  # scripted group (container) (typed FeaturePython)
  n = 0.105
FEATURE [App::DocumentObjectGroupPython] C_element056  label="C_element : 0.083"  # scripted group (container) (typed FeaturePython)
  n = 0.083
FEATURE [App::DocumentObjectGroupPython] N_element023  label="N_element : 0.023"  # scripted group (container) (typed FeaturePython)
  n = 0.023
FEATURE [App::DocumentObjectGroupPython] O_element057  label="O_element : 0.779"  # scripted group (container) (typed FeaturePython)
  n = 0.779
FEATURE [App::DocumentObjectGroupPython] Na_element010  label="Na_element : 0.097"  # scripted group (container) (typed FeaturePython)
  n = 0.002
FEATURE [App::DocumentObjectGroupPython] P_element006  label="P_element : 0.105"  # scripted group (container) (typed FeaturePython)
  n = 0.001
FEATURE [App::DocumentObjectGroupPython] S_element016  label="S_element : 0.017"  # scripted group (container) (typed FeaturePython)
  n = 0.002
FEATURE [App::DocumentObjectGroupPython] Cl_element014  label="Cl_element : 0.587"  # scripted group (container) (typed FeaturePython)
  n = 0.003
FEATURE [App::DocumentObjectGroupPython] K_element005  label="K_element : 0.015"  # scripted group (container) (typed FeaturePython)
  n = 0.002
FEATURE [App::DocumentObjectGroupPython] G4_LUNG_ICRP  # scripted group (container) (typed FeaturePython)
  Dunit = g/cm3
  Dvalue = 1.04
  Group = -> [H_element051,C_element056,N_element023,O_element057,Na_element010,P_element006,S_element016,Cl_element014,K_element005]
  conduct = 2
  density = 1
  expand = 3
  formula = G4_LUNG_ICRP
  name = G4_LUNG_ICRP
  specific = 4
FEATURE [App::DocumentObjectGroupPython] H_element052  label="H_element : 0.116"  # scripted group (container) (typed FeaturePython)
  n = 0.114318
FEATURE [App::DocumentObjectGroupPython] C_element057  label="C_element : 0.656"  # scripted group (container) (typed FeaturePython)
  n = 0.655824
FEATURE [App::DocumentObjectGroupPython] O_element058  label="O_element : 0.092"  # scripted group (container) (typed FeaturePython)
  n = 0.0921831
FEATURE [App::DocumentObjectGroupPython] Mg_element004  label="Mg_element : 0.135"  # scripted group (container) (typed FeaturePython)
  n = 0.134792
FEATURE [App::DocumentObjectGroupPython] Ca_element013  label="Ca_element : 0.003"  # scripted group (container) (typed FeaturePython)
  n = 0.002883
FEATURE [App::DocumentObjectGroupPython] G4_M3_WAX  # scripted group (container) (typed FeaturePython)
  Dunit = g/cm3
  Dvalue = 1.05
  Group = -> [H_element052,C_element057,O_element058,Mg_element004,Ca_element013]
  conduct = 2
  density = 1
  expand = 3
  formula = G4_M3_WAX
  name = G4_M3_WAX
  specific = 4
FEATURE [App::DocumentObjectGroupPython] Mg_element005  label="Mg_element : 1"  # scripted group (container) (typed FeaturePython)
  n = 1
  ref = Mg_element
FEATURE [App::DocumentObjectGroupPython] C_element058  label="C_element : 031"  # scripted group (container) (typed FeaturePython)
  n = 1
  ref = C_element
FEATURE [App::DocumentObjectGroupPython] O_element059  label="O_element : 030"  # scripted group (container) (typed FeaturePython)
  n = 3
  ref = O_element
FEATURE [App::DocumentObjectGroupPython] G4_MAGNESIUM_CARBONATE  # scripted group (container) (typed FeaturePython)
  Dunit = g/cm3
  Dvalue = 2.958
  Group = -> [Mg_element005,C_element058,O_element059]
  conduct = 2
  density = 1
  expand = 3
  formula = G4_MAGNESIUM_CARBONATE
  name = G4_MAGNESIUM_CARBONATE
  specific = 4
FEATURE [App::DocumentObjectGroupPython] Mg_element006  label="Mg_element : 002"  # scripted group (container) (typed FeaturePython)
  n = 1
  ref = Mg_element
FEATURE [App::DocumentObjectGroupPython] F_element013  label="F_element : 005"  # scripted group (container) (typed FeaturePython)
  n = 2
  ref = F_element
FEATURE [App::DocumentObjectGroupPython] G4_MAGNESIUM_FLUORIDE  # scripted group (container) (typed FeaturePython)
  Dunit = g/cm3
  Dvalue = 3
  Group = -> [Mg_element006,F_element013]
  conduct = 2
  density = 1
  expand = 3
  formula = G4_MAGNESIUM_FLUORIDE
  name = G4_MAGNESIUM_FLUORIDE
  specific = 4
FEATURE [App::DocumentObjectGroupPython] Mg_element007  label="Mg_element : 003"  # scripted group (container) (typed FeaturePython)
  n = 1
  ref = Mg_element
FEATURE [App::DocumentObjectGroupPython] O_element060  label="O_element : 031"  # scripted group (container) (typed FeaturePython)
  n = 1
  ref = O_element
FEATURE [App::DocumentObjectGroupPython] G4_MAGNESIUM_OXIDE  # scripted group (container) (typed FeaturePython)
  Dunit = g/cm3
  Dvalue = 3.58
  Group = -> [Mg_element007,O_element060]
  conduct = 2
  density = 1
  expand = 3
  formula = G4_MAGNESIUM_OXIDE
  name = G4_MAGNESIUM_OXIDE
  specific = 4
FEATURE [App::DocumentObjectGroupPython] Mg_element008  label="Mg_element : 004"  # scripted group (container) (typed FeaturePython)
  n = 1
  ref = Mg_element
FEATURE [App::DocumentObjectGroupPython] B_element006  label="B_element : 006"  # scripted group (container) (typed FeaturePython)
  n = 4
  ref = B_element
FEATURE [App::DocumentObjectGroupPython] O_element061  label="O_element : 032"  # scripted group (container) (typed FeaturePython)
  n = 7
  ref = O_element
FEATURE [App::DocumentObjectGroupPython] G4_MAGNESIUM_TETRABORATE  # scripted group (container) (typed FeaturePython)
  Dunit = g/cm3
  Dvalue = 2.53
  Group = -> [Mg_element008,B_element006,O_element061]
  conduct = 2
  density = 1
  expand = 3
  formula = G4_MAGNESIUM_TETRABORATE
  name = G4_MAGNESIUM_TETRABORATE
  specific = 4
FEATURE [App::DocumentObjectGroupPython] Hg_element001  label="Hg_element : 1"  # scripted group (container) (typed FeaturePython)
  n = 1
  ref = Hg_element
FEATURE [App::DocumentObjectGroupPython] I_element004  label="I_element : 2"  # scripted group (container) (typed FeaturePython)
  n = 2
  ref = I_element
FEATURE [App::DocumentObjectGroupPython] G4_MERCURIC_IODIDE  # scripted group (container) (typed FeaturePython)
  Dunit = g/cm3
  Dvalue = 6.36
  Group = -> [Hg_element001,I_element004]
  conduct = 2
  density = 1
  expand = 3
  formula = G4_MERCURIC_IODIDE
  name = G4_MERCURIC_IODIDE
  specific = 4
FEATURE [App::DocumentObjectGroupPython] C_element059  label="C_element : 032"  # scripted group (container) (typed FeaturePython)
  n = 1
  ref = C_element
FEATURE [App::DocumentObjectGroupPython] H_element053  label="H_element : 028"  # scripted group (container) (typed FeaturePython)
  n = 4
  ref = H_element
FEATURE [App::DocumentObjectGroupPython] G4_METHANE  # scripted group (container) (typed FeaturePython)
  Dunit = g/cm3
  Dvalue = 0.000667151
  Group = -> [C_element059,H_element053]
  conduct = 2
  density = 1
  expand = 3
  formula = G4_METHANE
  name = G4_METHANE
  specific = 4
FEATURE [App::DocumentObjectGroupPython] C_element060  label="C_element : 033"  # scripted group (container) (typed FeaturePython)
  n = 1
  ref = C_element
FEATURE [App::DocumentObjectGroupPython] H_element054  label="H_element : 029"  # scripted group (container) (typed FeaturePython)
  n = 4
  ref = H_element
FEATURE [App::DocumentObjectGroupPython] O_element062  label="O_element : 033"  # scripted group (container) (typed FeaturePython)
  n = 1
  ref = O_element
FEATURE [App::DocumentObjectGroupPython] G4_METHANOL  # scripted group (container) (typed FeaturePython)
  Dunit = g/cm3
  Dvalue = 0.7914
  Group = -> [C_element060,H_element054,O_element062]
  conduct = 2
  density = 1
  expand = 3
  formula = G4_METHANOL
  name = G4_METHANOL
  specific = 4
FEATURE [App::DocumentObjectGroupPython] H_element055  label="H_element : 0.134"  # scripted group (container) (typed FeaturePython)
  n = 0.13404
FEATURE [App::DocumentObjectGroupPython] C_element061  label="C_element : 0.778"  # scripted group (container) (typed FeaturePython)
  n = 0.77796
FEATURE [App::DocumentObjectGroupPython] O_element063  label="O_element : 0.035"  # scripted group (container) (typed FeaturePython)
  n = 0.03502
FEATURE [App::DocumentObjectGroupPython] Mg_element009  label="Mg_element : 0.039"  # scripted group (container) (typed FeaturePython)
  n = 0.038594
FEATURE [App::DocumentObjectGroupPython] Ti_element002  label="Ti_element : 0.014"  # scripted group (container) (typed FeaturePython)
  n = 0.014386
FEATURE [App::DocumentObjectGroupPython] G4_MIX_D_WAX  # scripted group (container) (typed FeaturePython)
  Dunit = g/cm3
  Dvalue = 0.99
  Group = -> [H_element055,C_element061,O_element063,Mg_element009,Ti_element002]
  conduct = 2
  density = 1
  expand = 3
  formula = G4_MIX_D_WAX
  name = G4_MIX_D_WAX
  specific = 4
FEATURE [App::DocumentObjectGroupPython] H_element056  label="H_element : 0.135"  # scripted group (container) (typed FeaturePython)
  n = 0.081192
FEATURE [App::DocumentObjectGroupPython] C_element062  label="C_element : 0.583"  # scripted group (container) (typed FeaturePython)
  n = 0.583442
FEATURE [App::DocumentObjectGroupPython] N_element024  label="N_element : 0.018"  # scripted group (container) (typed FeaturePython)
  n = 0.017798
FEATURE [App::DocumentObjectGroupPython] O_element064  label="O_element : 0.186"  # scripted group (container) (typed FeaturePython)
  n = 0.186381
FEATURE [App::DocumentObjectGroupPython] Mg_element010  label="Mg_element : 0.130"  # scripted group (container) (typed FeaturePython)
  n = 0.130287
FEATURE [App::DocumentObjectGroupPython] Cl_element015  label="Cl_element : 0.588"  # scripted group (container) (typed FeaturePython)
  n = 0.0009
FEATURE [App::DocumentObjectGroupPython] G4_MS20_TISSUE  # scripted group (container) (typed FeaturePython)
  Dunit = g/cm3
  Dvalue = 1
  Group = -> [H_element056,C_element062,N_element024,O_element064,Mg_element010,Cl_element015]
  conduct = 2
  density = 1
  expand = 3
  formula = G4_MS20_TISSUE
  name = G4_MS20_TISSUE
  specific = 4
FEATURE [App::DocumentObjectGroupPython] H_element057  label="H_element : 0.136"  # scripted group (container) (typed FeaturePython)
  n = 0.102
FEATURE [App::DocumentObjectGroupPython] C_element063  label="C_element : 0.143"  # scripted group (container) (typed FeaturePython)
  n = 0.143
FEATURE [App::DocumentObjectGroupPython] N_element025  label="N_element : 0.034"  # scripted group (container) (typed FeaturePython)
  n = 0.034
FEATURE [App::DocumentObjectGroupPython] O_element065  label="O_element : 0.710"  # scripted group (container) (typed FeaturePython)
  n = 0.71
FEATURE [App::DocumentObjectGroupPython] Na_element011  label="Na_element : 0.098"  # scripted group (container) (typed FeaturePython)
  n = 0.001
FEATURE [App::DocumentObjectGroupPython] P_element007  label="P_element : 0.002"  # scripted group (container) (typed FeaturePython)
  n = 0.002
FEATURE [App::DocumentObjectGroupPython] S_element017  label="S_element : 0.018"  # scripted group (container) (typed FeaturePython)
  n = 0.003
FEATURE [App::DocumentObjectGroupPython] Cl_element016  label="Cl_element : 0.589"  # scripted group (container) (typed FeaturePython)
  n = 0.001
FEATURE [App::DocumentObjectGroupPython] K_element006  label="K_element : 0.004"  # scripted group (container) (typed FeaturePython)
  n = 0.004
FEATURE [App::DocumentObjectGroupPython] G4_MUSCLE_SKELETAL_ICRP  # scripted group (container) (typed FeaturePython)
  Dunit = g/cm3
  Dvalue = 1.05
  Group = -> [H_element057,C_element063,N_element025,O_element065,Na_element011,P_element007,S_element017,Cl_element016,K_element006]
  conduct = 2
  density = 1
  expand = 3
  formula = G4_MUSCLE_SKELETAL_ICRP
  name = G4_MUSCLE_SKELETAL_ICRP
  specific = 4
FEATURE [App::DocumentObjectGroupPython] H_element058  label="H_element : 0.137"  # scripted group (container) (typed FeaturePython)
  n = 0.102102
FEATURE [App::DocumentObjectGroupPython] C_element064  label="C_element : 0.123"  # scripted group (container) (typed FeaturePython)
  n = 0.123123
FEATURE [App::DocumentObjectGroupPython] N_element026  label="N_element : 0.756"  # scripted group (container) (typed FeaturePython)
  n = 0.035035
FEATURE [App::DocumentObjectGroupPython] O_element066  label="O_element : 0.730"  # scripted group (container) (typed FeaturePython)
  n = 0.72973
FEATURE [App::DocumentObjectGroupPython] Na_element012  label="Na_element : 0.099"  # scripted group (container) (typed FeaturePython)
  n = 0.001001
FEATURE [App::DocumentObjectGroupPython] P_element008  label="P_element : 0.106"  # scripted group (container) (typed FeaturePython)
  n = 0.002002
FEATURE [App::DocumentObjectGroupPython] S_element018  label="S_element : 0.019"  # scripted group (container) (typed FeaturePython)
  n = 0.004004
FEATURE [App::DocumentObjectGroupPython] K_element007  label="K_element : 0.016"  # scripted group (container) (typed FeaturePython)
  n = 0.003003
FEATURE [App::DocumentObjectGroupPython] G4_MUSCLE_STRIATED_ICRU  # scripted group (container) (typed FeaturePython)
  Dunit = g/cm3
  Dvalue = 1.04
  Group = -> [H_element058,C_element064,N_element026,O_element066,Na_element012,P_element008,S_element018,K_element007]
  conduct = 2
  density = 1
  expand = 3
  formula = G4_MUSCLE_STRIATED_ICRU
  name = G4_MUSCLE_STRIATED_ICRU
  specific = 4
FEATURE [App::DocumentObjectGroupPython] H_element059  label="H_element : 0.098"  # scripted group (container) (typed FeaturePython)
  n = 0.0982341
FEATURE [App::DocumentObjectGroupPython] C_element065  label="C_element : 0.156"  # scripted group (container) (typed FeaturePython)
  n = 0.156214
FEATURE [App::DocumentObjectGroupPython] N_element027  label="N_element : 0.757"  # scripted group (container) (typed FeaturePython)
  n = 0.035451
FEATURE [App::DocumentObjectGroupPython] O_element067  label="O_element : 0.880"  # scripted group (container) (typed FeaturePython)
  n = 0.710101
FEATURE [App::DocumentObjectGroupPython] G4_MUSCLE_WITH_SUCROSE  # scripted group (container) (typed FeaturePython)
  Dunit = g/cm3
  Dvalue = 1.11
  Group = -> [H_element059,C_element065,N_element027,O_element067]
  conduct = 2
  density = 1
  expand = 3
  formula = G4_MUSCLE_WITH_SUCROSE
  name = G4_MUSCLE_WITH_SUCROSE
  specific = 4
FEATURE [App::DocumentObjectGroupPython] H_element060  label="H_element : 0.138"  # scripted group (container) (typed FeaturePython)
  n = 0.101969
FEATURE [App::DocumentObjectGroupPython] C_element066  label="C_element : 0.120"  # scripted group (container) (typed FeaturePython)
  n = 0.120058
FEATURE [App::DocumentObjectGroupPython] N_element028  label="N_element : 0.758"  # scripted group (container) (typed FeaturePython)
  n = 0.035451
FEATURE [App::DocumentObjectGroupPython] O_element068  label="O_element : 0.743"  # scripted group (container) (typed FeaturePython)
  n = 0.742522
FEATURE [App::DocumentObjectGroupPython] G4_MUSCLE_WITHOUT_SUCROSE  # scripted group (container) (typed FeaturePython)
  Dunit = g/cm3
  Dvalue = 1.07
  Group = -> [H_element060,C_element066,N_element028,O_element068]
  conduct = 2
  density = 1
  expand = 3
  formula = G4_MUSCLE_WITHOUT_SUCROSE
  name = G4_MUSCLE_WITHOUT_SUCROSE
  specific = 4
FEATURE [App::DocumentObjectGroupPython] C_element067  label="C_element : 10"  # scripted group (container) (typed FeaturePython)
  n = 10
  ref = C_element
FEATURE [App::DocumentObjectGroupPython] H_element061  label="H_element : 030"  # scripted group (container) (typed FeaturePython)
  n = 8
  ref = H_element
FEATURE [App::DocumentObjectGroupPython] G4_NAPHTHALENE  # scripted group (container) (typed FeaturePython)
  Dunit = g/cm3
  Dvalue = 1.145
  Group = -> [C_element067,H_element061]
  conduct = 2
  density = 1
  expand = 3
  formula = G4_NAPHTHALENE
  name = G4_NAPHTHALENE
  specific = 4
FEATURE [App::DocumentObjectGroupPython] C_element068  label="C_element : 034"  # scripted group (container) (typed FeaturePython)
  n = 6
  ref = C_element
FEATURE [App::DocumentObjectGroupPython] H_element062  label="H_element : 031"  # scripted group (container) (typed FeaturePython)
  n = 5
  ref = H_element
FEATURE [App::DocumentObjectGroupPython] N_element029  label="N_element : 012"  # scripted group (container) (typed FeaturePython)
  n = 1
  ref = N_element
FEATURE [App::DocumentObjectGroupPython] O_element069  label="O_element : 034"  # scripted group (container) (typed FeaturePython)
  n = 2
  ref = O_element
FEATURE [App::DocumentObjectGroupPython] G4_NITROBENZENE  # scripted group (container) (typed FeaturePython)
  Dunit = g/cm3
  Dvalue = 1.19867
  Group = -> [C_element068,H_element062,N_element029,O_element069]
  conduct = 2
  density = 1
  expand = 3
  formula = G4_NITROBENZENE
  name = G4_NITROBENZENE
  specific = 4
FEATURE [App::DocumentObjectGroupPython] N_element030  label="N_element : 013"  # scripted group (container) (typed FeaturePython)
  n = 2
  ref = N_element
FEATURE [App::DocumentObjectGroupPython] O_element070  label="O_element : 035"  # scripted group (container) (typed FeaturePython)
  n = 1
  ref = O_element
FEATURE [App::DocumentObjectGroupPython] G4_NITROUS_OXIDE  # scripted group (container) (typed FeaturePython)
  Dunit = g/cm3
  Dvalue = 0.00183094
  Group = -> [N_element030,O_element070]
  conduct = 2
  density = 1
  expand = 3
  formula = G4_NITROUS_OXIDE
  name = G4_NITROUS_OXIDE
  specific = 4
FEATURE [App::DocumentObjectGroupPython] H_element063  label="H_element : 0.104"  # scripted group (container) (typed FeaturePython)
  n = 0.103509
FEATURE [App::DocumentObjectGroupPython] C_element069  label="C_element : 0.648"  # scripted group (container) (typed FeaturePython)
  n = 0.648416
FEATURE [App::DocumentObjectGroupPython] N_element031  label="N_element : 0.100"  # scripted group (container) (typed FeaturePython)
  n = 0.0995361
FEATURE [App::DocumentObjectGroupPython] O_element071  label="O_element : 0.149"  # scripted group (container) (typed FeaturePython)
  n = 0.148539
FEATURE [App::DocumentObjectGroupPython] G4_NYLON_8062  label="G4_NYLON-8062"  # scripted group (container) (typed FeaturePython)
  Dunit = g/cm3
  Dvalue = 1.08
  Group = -> [H_element063,C_element069,N_element031,O_element071]
  conduct = 2
  density = 1
  expand = 3
  formula = G4_NYLON-8062
  name = G4_NYLON-8062
  specific = 4
FEATURE [App::DocumentObjectGroupPython] C_element070  label="C_element : 035"  # scripted group (container) (typed FeaturePython)
  n = 6
  ref = C_element
FEATURE [App::DocumentObjectGroupPython] H_element064  label="H_element : 11"  # scripted group (container) (typed FeaturePython)
  n = 11
  ref = H_element
FEATURE [App::DocumentObjectGroupPython] N_element032  label="N_element : 014"  # scripted group (container) (typed FeaturePython)
  n = 1
  ref = N_element
FEATURE [App::DocumentObjectGroupPython] O_element072  label="O_element : 036"  # scripted group (container) (typed FeaturePython)
  n = 1
  ref = O_element
FEATURE [App::DocumentObjectGroupPython] G4_NYLON_6_6  label="G4_NYLON-6-6"  # scripted group (container) (typed FeaturePython)
  Dunit = g/cm3
  Dvalue = 1.14
  Group = -> [C_element070,H_element064,N_element032,O_element072]
  conduct = 2
  density = 1
  expand = 3
  formula = G4_NYLON-6-6
  name = G4_NYLON-6-6
  specific = 4
FEATURE [App::DocumentObjectGroupPython] H_element065  label="H_element : 0.139"  # scripted group (container) (typed FeaturePython)
  n = 0.107062
FEATURE [App::DocumentObjectGroupPython] C_element071  label="C_element : 0.680"  # scripted group (container) (typed FeaturePython)
  n = 0.680449
FEATURE [App::DocumentObjectGroupPython] N_element033  label="N_element : 0.099"  # scripted group (container) (typed FeaturePython)
  n = 0.099189
FEATURE [App::DocumentObjectGroupPython] O_element073  label="O_element : 0.113"  # scripted group (container) (typed FeaturePython)
  n = 0.1133
FEATURE [App::DocumentObjectGroupPython] G4_NYLON_6_10  label="G4_NYLON-6-10"  # scripted group (container) (typed FeaturePython)
  Dunit = g/cm3
  Dvalue = 1.14
  Group = -> [H_element065,C_element071,N_element033,O_element073]
  conduct = 2
  density = 1
  expand = 3
  formula = G4_NYLON-6-10
  name = G4_NYLON-6-10
  specific = 4
FEATURE [App::DocumentObjectGroupPython] H_element066  label="H_element : 0.140"  # scripted group (container) (typed FeaturePython)
  n = 0.115476
FEATURE [App::DocumentObjectGroupPython] C_element072  label="C_element : 0.721"  # scripted group (container) (typed FeaturePython)
  n = 0.720818
FEATURE [App::DocumentObjectGroupPython] N_element034  label="N_element : 0.076"  # scripted group (container) (typed FeaturePython)
  n = 0.0764169
FEATURE [App::DocumentObjectGroupPython] O_element074  label="O_element : 0.087"  # scripted group (container) (typed FeaturePython)
  n = 0.0872889
FEATURE [App::DocumentObjectGroupPython] G4_NYLON_11_RILSAN  label="G4_NYLON-11_RILSAN"  # scripted group (container) (typed FeaturePython)
  Dunit = g/cm3
  Dvalue = 1.425
  Group = -> [H_element066,C_element072,N_element034,O_element074]
  conduct = 2
  density = 1
  expand = 3
  formula = G4_NYLON-11_RILSAN
  name = G4_NYLON-11_RILSAN
  specific = 4
FEATURE [App::DocumentObjectGroupPython] C_element073  label="C_element : 8"  # scripted group (container) (typed FeaturePython)
  n = 8
  ref = C_element
FEATURE [App::DocumentObjectGroupPython] H_element067  label="H_element : 18"  # scripted group (container) (typed FeaturePython)
  n = 18
  ref = H_element
FEATURE [App::DocumentObjectGroupPython] G4_OCTANE  # scripted group (container) (typed FeaturePython)
  Dunit = g/cm3
  Dvalue = 0.7026
  Group = -> [C_element073,H_element067]
  conduct = 2
  density = 1
  expand = 3
  formula = G4_OCTANE
  name = G4_OCTANE
  specific = 4
FEATURE [App::DocumentObjectGroupPython] C_element074  label="C_element : 25"  # scripted group (container) (typed FeaturePython)
  n = 25
  ref = C_element
FEATURE [App::DocumentObjectGroupPython] H_element068  label="H_element : 52"  # scripted group (container) (typed FeaturePython)
  n = 52
  ref = H_element
FEATURE [App::DocumentObjectGroupPython] G4_PARAFFIN  # scripted group (container) (typed FeaturePython)
  Dunit = g/cm3
  Dvalue = 0.93
  Group = -> [C_element074,H_element068]
  conduct = 2
  density = 1
  expand = 3
  formula = G4_PARAFFIN
  name = G4_PARAFFIN
  specific = 4
FEATURE [App::DocumentObjectGroupPython] C_element075  label="C_element : 036"  # scripted group (container) (typed FeaturePython)
  n = 5
  ref = C_element
FEATURE [App::DocumentObjectGroupPython] H_element069  label="H_element : 032"  # scripted group (container) (typed FeaturePython)
  n = 12
  ref = H_element
FEATURE [App::DocumentObjectGroupPython] G4_N_PENTANE  label="G4_N-PENTANE"  # scripted group (container) (typed FeaturePython)
  Dunit = g/cm3
  Dvalue = 0.6262
  Group = -> [C_element075,H_element069]
  conduct = 2
  density = 1
  expand = 3
  formula = G4_N-PENTANE
  name = G4_N-PENTANE
  specific = 4
FEATURE [App::DocumentObjectGroupPython] H_element070  label="H_element : 0.014"  # scripted group (container) (typed FeaturePython)
  n = 0.0141
FEATURE [App::DocumentObjectGroupPython] C_element076  label="C_element : 0.072"  # scripted group (container) (typed FeaturePython)
  n = 0.072261
FEATURE [App::DocumentObjectGroupPython] N_element035  label="N_element : 0.019"  # scripted group (container) (typed FeaturePython)
  n = 0.01932
FEATURE [App::DocumentObjectGroupPython] O_element075  label="O_element : 0.066"  # scripted group (container) (typed FeaturePython)
  n = 0.066101
FEATURE [App::DocumentObjectGroupPython] S_element019  label="S_element : 0.020"  # scripted group (container) (typed FeaturePython)
  n = 0.00189
FEATURE [App::DocumentObjectGroupPython] Br_element004  label="Br_element : 0.349"  # scripted group (container) (typed FeaturePython)
  n = 0.349103
FEATURE [App::DocumentObjectGroupPython] Ag_element001  label="Ag_element : 0.474"  # scripted group (container) (typed FeaturePython)
  n = 0.474105
FEATURE [App::DocumentObjectGroupPython] I_element005  label="I_element : 0.003"  # scripted group (container) (typed FeaturePython)
  n = 0.00312
FEATURE [App::DocumentObjectGroupPython] G4_PHOTO_EMULSION  # scripted group (container) (typed FeaturePython)
  Dunit = g/cm3
  Dvalue = 3.815
  Group = -> [H_element070,C_element076,N_element035,O_element075,S_element019,Br_element004,Ag_element001,I_element005]
  conduct = 2
  density = 1
  expand = 3
  formula = G4_PHOTO_EMULSION
  name = G4_PHOTO_EMULSION
  specific = 4
FEATURE [App::DocumentObjectGroupPython] C_element077  label="C_element : 9"  # scripted group (container) (typed FeaturePython)
  n = 9
  ref = C_element
FEATURE [App::DocumentObjectGroupPython] H_element071  label="H_element : 033"  # scripted group (container) (typed FeaturePython)
  n = 10
  ref = H_element
FEATURE [App::DocumentObjectGroupPython] G4_PLASTIC_SC_VINYLTOLUENE  # scripted group (container) (typed FeaturePython)
  Dunit = g/cm3
  Dvalue = 1.032
  Group = -> [C_element077,H_element071]
  conduct = 2
  density = 1
  expand = 3
  formula = G4_PLASTIC_SC_VINYLTOLUENE
  name = G4_PLASTIC_SC_VINYLTOLUENE
  specific = 4
FEATURE [App::DocumentObjectGroupPython] Pu_element001  label="Pu_element : 1"  # scripted group (container) (typed FeaturePython)
  n = 1
  ref = Pu_element
FEATURE [App::DocumentObjectGroupPython] O_element076  label="O_element : 037"  # scripted group (container) (typed FeaturePython)
  n = 2
  ref = O_element
FEATURE [App::DocumentObjectGroupPython] G4_PLUTONIUM_DIOXIDE  # scripted group (container) (typed FeaturePython)
  Dunit = g/cm3
  Dvalue = 11.46
  Group = -> [Pu_element001,O_element076]
  conduct = 2
  density = 1
  expand = 3
  formula = G4_PLUTONIUM_DIOXIDE
  name = G4_PLUTONIUM_DIOXIDE
  specific = 4
FEATURE [App::DocumentObjectGroupPython] C_element078  label="C_element : 037"  # scripted group (container) (typed FeaturePython)
  n = 3
  ref = C_element
FEATURE [App::DocumentObjectGroupPython] H_element072  label="H_element : 034"  # scripted group (container) (typed FeaturePython)
  n = 3
  ref = H_element
FEATURE [App::DocumentObjectGroupPython] N_element036  label="N_element : 015"  # scripted group (container) (typed FeaturePython)
  n = 1
  ref = N_element
FEATURE [App::DocumentObjectGroupPython] G4_POLYACRYLONITRILE  # scripted group (container) (typed FeaturePython)
  Dunit = g/cm3
  Dvalue = 1.17
  Group = -> [C_element078,H_element072,N_element036]
  conduct = 2
  density = 1
  expand = 3
  formula = G4_POLYACRYLONITRILE
  name = G4_POLYACRYLONITRILE
  specific = 4
FEATURE [App::DocumentObjectGroupPython] C_element079  label="C_element : 16"  # scripted group (container) (typed FeaturePython)
  n = 16
  ref = C_element
FEATURE [App::DocumentObjectGroupPython] H_element073  label="H_element : 035"  # scripted group (container) (typed FeaturePython)
  n = 14
  ref = H_element
FEATURE [App::DocumentObjectGroupPython] O_element077  label="O_element : 038"  # scripted group (container) (typed FeaturePython)
  n = 3
  ref = O_element
FEATURE [App::DocumentObjectGroupPython] G4_POLYCARBONATE  # scripted group (container) (typed FeaturePython)
  Dunit = g/cm3
  Dvalue = 1.2
  Group = -> [C_element079,H_element073,O_element077]
  conduct = 2
  density = 1
  expand = 3
  formula = G4_POLYCARBONATE
  name = G4_POLYCARBONATE
  specific = 4
FEATURE [App::DocumentObjectGroupPython] C_element080  label="C_element : 038"  # scripted group (container) (typed FeaturePython)
  n = 8
  ref = C_element
FEATURE [App::DocumentObjectGroupPython] H_element074  label="H_element : 036"  # scripted group (container) (typed FeaturePython)
  n = 7
  ref = H_element
FEATURE [App::DocumentObjectGroupPython] Cl_element017  label="Cl_element : 007"  # scripted group (container) (typed FeaturePython)
  n = 1
  ref = Cl_element
FEATURE [App::DocumentObjectGroupPython] G4_POLYCHLOROSTYRENE  # scripted group (container) (typed FeaturePython)
  Dunit = g/cm3
  Dvalue = 1.3
  Group = -> [C_element080,H_element074,Cl_element017]
  conduct = 2
  density = 1
  expand = 3
  formula = G4_POLYCHLOROSTYRENE
  name = G4_POLYCHLOROSTYRENE
  specific = 4
FEATURE [App::DocumentObjectGroupPython] C_element081  label="C_element : 039"  # scripted group (container) (typed FeaturePython)
  n = 1
  ref = C_element
FEATURE [App::DocumentObjectGroupPython] H_element075  label="H_element : 037"  # scripted group (container) (typed FeaturePython)
  n = 2
  ref = H_element
FEATURE [App::DocumentObjectGroupPython] G4_POLYETHYLENE  # scripted group (container) (typed FeaturePython)
  Dunit = g/cm3
  Dvalue = 0.94
  Group = -> [C_element081,H_element075]
  conduct = 2
  density = 1
  expand = 3
  formula = G4_POLYETHYLENE
  name = G4_POLYETHYLENE
  specific = 4
FEATURE [App::DocumentObjectGroupPython] C_element082  label="C_element : 040"  # scripted group (container) (typed FeaturePython)
  n = 10
  ref = C_element
FEATURE [App::DocumentObjectGroupPython] H_element076  label="H_element : 038"  # scripted group (container) (typed FeaturePython)
  n = 8
  ref = H_element
FEATURE [App::DocumentObjectGroupPython] O_element078  label="O_element : 039"  # scripted group (container) (typed FeaturePython)
  n = 4
  ref = O_element
FEATURE [App::DocumentObjectGroupPython] G4_MYLAR  # scripted group (container) (typed FeaturePython)
  Dunit = g/cm3
  Dvalue = 1.4
  Group = -> [C_element082,H_element076,O_element078]
  conduct = 2
  density = 1
  expand = 3
  formula = G4_MYLAR
  name = G4_MYLAR
  specific = 4
FEATURE [App::DocumentObjectGroupPython] C_element083  label="C_element : 041"  # scripted group (container) (typed FeaturePython)
  n = 5
  ref = C_element
FEATURE [App::DocumentObjectGroupPython] H_element077  label="H_element : 039"  # scripted group (container) (typed FeaturePython)
  n = 8
  ref = H_element
FEATURE [App::DocumentObjectGroupPython] O_element079  label="O_element : 040"  # scripted group (container) (typed FeaturePython)
  n = 2
  ref = O_element
FEATURE [App::DocumentObjectGroupPython] G4_PLEXIGLASS  # scripted group (container) (typed FeaturePython)
  Dunit = g/cm3
  Dvalue = 1.19
  Group = -> [C_element083,H_element077,O_element079]
  conduct = 2
  density = 1
  expand = 3
  formula = G4_PLEXIGLASS
  name = G4_PLEXIGLASS
  specific = 4
FEATURE [App::DocumentObjectGroupPython] C_element084  label="C_element : 042"  # scripted group (container) (typed FeaturePython)
  n = 1
  ref = C_element
FEATURE [App::DocumentObjectGroupPython] H_element078  label="H_element : 040"  # scripted group (container) (typed FeaturePython)
  n = 2
  ref = H_element
FEATURE [App::DocumentObjectGroupPython] O_element080  label="O_element : 041"  # scripted group (container) (typed FeaturePython)
  n = 1
  ref = O_element
FEATURE [App::DocumentObjectGroupPython] G4_POLYOXYMETHYLENE  # scripted group (container) (typed FeaturePython)
  Dunit = g/cm3
  Dvalue = 1.425
  Group = -> [C_element084,H_element078,O_element080]
  conduct = 2
  density = 1
  expand = 3
  formula = G4_POLYOXYMETHYLENE
  name = G4_POLYOXYMETHYLENE
  specific = 4
FEATURE [App::DocumentObjectGroupPython] C_element085  label="C_element : 043"  # scripted group (container) (typed FeaturePython)
  n = 2
  ref = C_element
FEATURE [App::DocumentObjectGroupPython] H_element079  label="H_element : 041"  # scripted group (container) (typed FeaturePython)
  n = 4
  ref = H_element
FEATURE [App::DocumentObjectGroupPython] G4_POLYPROPYLENE  # scripted group (container) (typed FeaturePython)
  Dunit = g/cm3
  Dvalue = 0.9
  Group = -> [C_element085,H_element079]
  conduct = 2
  density = 1
  expand = 3
  formula = G4_POLYPROPYLENE
  name = G4_POLYPROPYLENE
  specific = 4
FEATURE [App::DocumentObjectGroupPython] C_element086  label="C_element : 044"  # scripted group (container) (typed FeaturePython)
  n = 8
  ref = C_element
FEATURE [App::DocumentObjectGroupPython] H_element080  label="H_element : 042"  # scripted group (container) (typed FeaturePython)
  n = 8
  ref = H_element
FEATURE [App::DocumentObjectGroupPython] G4_POLYSTYRENE  # scripted group (container) (typed FeaturePython)
  Dunit = g/cm3
  Dvalue = 1.06
  Group = -> [C_element086,H_element080]
  conduct = 2
  density = 1
  expand = 3
  formula = G4_POLYSTYRENE
  name = G4_POLYSTYRENE
  specific = 4
FEATURE [App::DocumentObjectGroupPython] C_element087  label="C_element : 045"  # scripted group (container) (typed FeaturePython)
  n = 2
  ref = C_element
FEATURE [App::DocumentObjectGroupPython] F_element014  label="F_element : 4"  # scripted group (container) (typed FeaturePython)
  n = 4
  ref = F_element
FEATURE [App::DocumentObjectGroupPython] G4_TEFLON  # scripted group (container) (typed FeaturePython)
  Dunit = g/cm3
  Dvalue = 2.2
  Group = -> [C_element087,F_element014]
  conduct = 2
  density = 1
  expand = 3
  formula = G4_TEFLON
  name = G4_TEFLON
  specific = 4
FEATURE [App::DocumentObjectGroupPython] C_element088  label="C_element : 046"  # scripted group (container) (typed FeaturePython)
  n = 2
  ref = C_element
FEATURE [App::DocumentObjectGroupPython] F_element015  label="F_element : 006"  # scripted group (container) (typed FeaturePython)
  n = 3
  ref = F_element
FEATURE [App::DocumentObjectGroupPython] Cl_element018  label="Cl_element : 008"  # scripted group (container) (typed FeaturePython)
  n = 1
  ref = Cl_element
FEATURE [App::DocumentObjectGroupPython] G4_POLYTRIFLUOROCHLOROETHYLENE  # scripted group (container) (typed FeaturePython)
  Dunit = g/cm3
  Dvalue = 2.1
  Group = -> [C_element088,F_element015,Cl_element018]
  conduct = 2
  density = 1
  expand = 3
  formula = G4_POLYTRIFLUOROCHLOROETHYLENE
  name = G4_POLYTRIFLUOROCHLOROETHYLENE
  specific = 4
FEATURE [App::DocumentObjectGroupPython] C_element089  label="C_element : 047"  # scripted group (container) (typed FeaturePython)
  n = 4
  ref = C_element
FEATURE [App::DocumentObjectGroupPython] H_element081  label="H_element : 043"  # scripted group (container) (typed FeaturePython)
  n = 6
  ref = H_element
FEATURE [App::DocumentObjectGroupPython] O_element081  label="O_element : 042"  # scripted group (container) (typed FeaturePython)
  n = 2
  ref = O_element
FEATURE [App::DocumentObjectGroupPython] G4_POLYVINYL_ACETATE  # scripted group (container) (typed FeaturePython)
  Dunit = g/cm3
  Dvalue = 1.19
  Group = -> [C_element089,H_element081,O_element081]
  conduct = 2
  density = 1
  expand = 3
  formula = G4_POLYVINYL_ACETATE
  name = G4_POLYVINYL_ACETATE
  specific = 4
FEATURE [App::DocumentObjectGroupPython] C_element090  label="C_element : 048"  # scripted group (container) (typed FeaturePython)
  n = 2
  ref = C_element
FEATURE [App::DocumentObjectGroupPython] H_element082  label="H_element : 044"  # scripted group (container) (typed FeaturePython)
  n = 4
  ref = H_element
FEATURE [App::DocumentObjectGroupPython] O_element082  label="O_element : 043"  # scripted group (container) (typed FeaturePython)
  n = 1
  ref = O_element
FEATURE [App::DocumentObjectGroupPython] G4_POLYVINYL_ALCOHOL  # scripted group (container) (typed FeaturePython)
  Dunit = g/cm3
  Dvalue = 1.3
  Group = -> [C_element090,H_element082,O_element082]
  conduct = 2
  density = 1
  expand = 3
  formula = G4_POLYVINYL_ALCOHOL
  name = G4_POLYVINYL_ALCOHOL
  specific = 4
FEATURE [App::DocumentObjectGroupPython] C_element091  label="C_element : 049"  # scripted group (container) (typed FeaturePython)
  n = 8
  ref = C_element
FEATURE [App::DocumentObjectGroupPython] H_element083  label="H_element : 045"  # scripted group (container) (typed FeaturePython)
  n = 14
  ref = H_element
FEATURE [App::DocumentObjectGroupPython] O_element083  label="O_element : 044"  # scripted group (container) (typed FeaturePython)
  n = 2
  ref = O_element
FEATURE [App::DocumentObjectGroupPython] G4_POLYVINYL_BUTYRAL  # scripted group (container) (typed FeaturePython)
  Dunit = g/cm3
  Dvalue = 1.12
  Group = -> [C_element091,H_element083,O_element083]
  conduct = 2
  density = 1
  expand = 3
  formula = G4_POLYVINYL_BUTYRAL
  name = G4_POLYVINYL_BUTYRAL
  specific = 4
FEATURE [App::DocumentObjectGroupPython] C_element092  label="C_element : 050"  # scripted group (container) (typed FeaturePython)
  n = 2
  ref = C_element
FEATURE [App::DocumentObjectGroupPython] H_element084  label="H_element : 046"  # scripted group (container) (typed FeaturePython)
  n = 3
  ref = H_element
FEATURE [App::DocumentObjectGroupPython] Cl_element019  label="Cl_element : 009"  # scripted group (container) (typed FeaturePython)
  n = 1
  ref = Cl_element
FEATURE [App::DocumentObjectGroupPython] G4_POLYVINYL_CHLORIDE  # scripted group (container) (typed FeaturePython)
  Dunit = g/cm3
  Dvalue = 1.3
  Group = -> [C_element092,H_element084,Cl_element019]
  conduct = 2
  density = 1
  expand = 3
  formula = G4_POLYVINYL_CHLORIDE
  name = G4_POLYVINYL_CHLORIDE
  specific = 4
FEATURE [App::DocumentObjectGroupPython] C_element093  label="C_element : 051"  # scripted group (container) (typed FeaturePython)
  n = 2
  ref = C_element
FEATURE [App::DocumentObjectGroupPython] H_element085  label="H_element : 047"  # scripted group (container) (typed FeaturePython)
  n = 2
  ref = H_element
FEATURE [App::DocumentObjectGroupPython] Cl_element020  label="Cl_element : 010"  # scripted group (container) (typed FeaturePython)
  n = 2
  ref = Cl_element
FEATURE [App::DocumentObjectGroupPython] G4_POLYVINYLIDENE_CHLORIDE  # scripted group (container) (typed FeaturePython)
  Dunit = g/cm3
  Dvalue = 1.7
  Group = -> [C_element093,H_element085,Cl_element020]
  conduct = 2
  density = 1
  expand = 3
  formula = G4_POLYVINYLIDENE_CHLORIDE
  name = G4_POLYVINYLIDENE_CHLORIDE
  specific = 4
FEATURE [App::DocumentObjectGroupPython] C_element094  label="C_element : 052"  # scripted group (container) (typed FeaturePython)
  n = 2
  ref = C_element
FEATURE [App::DocumentObjectGroupPython] H_element086  label="H_element : 048"  # scripted group (container) (typed FeaturePython)
  n = 2
  ref = H_element
FEATURE [App::DocumentObjectGroupPython] F_element016  label="F_element : 007"  # scripted group (container) (typed FeaturePython)
  n = 2
  ref = F_element
FEATURE [App::DocumentObjectGroupPython] G4_POLYVINYLIDENE_FLUORIDE  # scripted group (container) (typed FeaturePython)
  Dunit = g/cm3
  Dvalue = 1.76
  Group = -> [C_element094,H_element086,F_element016]
  conduct = 2
  density = 1
  expand = 3
  formula = G4_POLYVINYLIDENE_FLUORIDE
  name = G4_POLYVINYLIDENE_FLUORIDE
  specific = 4
FEATURE [App::DocumentObjectGroupPython] C_element095  label="C_element : 053"  # scripted group (container) (typed FeaturePython)
  n = 6
  ref = C_element
FEATURE [App::DocumentObjectGroupPython] H_element087  label="H_element : 9"  # scripted group (container) (typed FeaturePython)
  n = 9
  ref = H_element
FEATURE [App::DocumentObjectGroupPython] N_element037  label="N_element : 016"  # scripted group (container) (typed FeaturePython)
  n = 1
  ref = N_element
FEATURE [App::DocumentObjectGroupPython] O_element084  label="O_element : 045"  # scripted group (container) (typed FeaturePython)
  n = 1
  ref = O_element
FEATURE [App::DocumentObjectGroupPython] G4_POLYVINYL_PYRROLIDONE  # scripted group (container) (typed FeaturePython)
  Dunit = g/cm3
  Dvalue = 1.25
  Group = -> [C_element095,H_element087,N_element037,O_element084]
  conduct = 2
  density = 1
  expand = 3
  formula = G4_POLYVINYL_PYRROLIDONE
  name = G4_POLYVINYL_PYRROLIDONE
  specific = 4
FEATURE [App::DocumentObjectGroupPython] K_element008  label="K_element : 1"  # scripted group (container) (typed FeaturePython)
  n = 1
  ref = K_element
FEATURE [App::DocumentObjectGroupPython] I_element006  label="I_element : 003"  # scripted group (container) (typed FeaturePython)
  n = 1
  ref = I_element
FEATURE [App::DocumentObjectGroupPython] G4_POTASSIUM_IODIDE  # scripted group (container) (typed FeaturePython)
  Dunit = g/cm3
  Dvalue = 3.13
  Group = -> [K_element008,I_element006]
  conduct = 2
  density = 1
  expand = 3
  formula = G4_POTASSIUM_IODIDE
  name = G4_POTASSIUM_IODIDE
  specific = 4
FEATURE [App::DocumentObjectGroupPython] K_element009  label="K_element : 2"  # scripted group (container) (typed FeaturePython)
  n = 2
  ref = K_element
FEATURE [App::DocumentObjectGroupPython] O_element085  label="O_element : 046"  # scripted group (container) (typed FeaturePython)
  n = 1
  ref = O_element
FEATURE [App::DocumentObjectGroupPython] G4_POTASSIUM_OXIDE  # scripted group (container) (typed FeaturePython)
  Dunit = g/cm3
  Dvalue = 2.32
  Group = -> [K_element009,O_element085]
  conduct = 2
  density = 1
  expand = 3
  formula = G4_POTASSIUM_OXIDE
  name = G4_POTASSIUM_OXIDE
  specific = 4
FEATURE [App::DocumentObjectGroupPython] C_element096  label="C_element : 054"  # scripted group (container) (typed FeaturePython)
  n = 3
  ref = C_element
FEATURE [App::DocumentObjectGroupPython] H_element088  label="H_element : 049"  # scripted group (container) (typed FeaturePython)
  n = 8
  ref = H_element
FEATURE [App::DocumentObjectGroupPython] G4_PROPANE  # scripted group (container) (typed FeaturePython)
  Dunit = g/cm3
  Dvalue = 0.00187939
  Group = -> [C_element096,H_element088]
  conduct = 2
  density = 1
  expand = 3
  formula = G4_PROPANE
  name = G4_PROPANE
  specific = 4
FEATURE [App::DocumentObjectGroupPython] C_element097  label="C_element : 055"  # scripted group (container) (typed FeaturePython)
  n = 3
  ref = C_element
FEATURE [App::DocumentObjectGroupPython] H_element089  label="H_element : 050"  # scripted group (container) (typed FeaturePython)
  n = 8
  ref = H_element
FEATURE [App::DocumentObjectGroupPython] G4_lPROPANE  # scripted group (container) (typed FeaturePython)
  Dunit = g/cm3
  Dvalue = 0.43
  Group = -> [C_element097,H_element089]
  conduct = 2
  density = 1
  expand = 3
  formula = G4_lPROPANE
  name = G4_lPROPANE
  specific = 4
FEATURE [App::DocumentObjectGroupPython] C_element098  label="C_element : 056"  # scripted group (container) (typed FeaturePython)
  n = 3
  ref = C_element
FEATURE [App::DocumentObjectGroupPython] H_element090  label="H_element : 051"  # scripted group (container) (typed FeaturePython)
  n = 8
  ref = H_element
FEATURE [App::DocumentObjectGroupPython] O_element086  label="O_element : 047"  # scripted group (container) (typed FeaturePython)
  n = 1
  ref = O_element
FEATURE [App::DocumentObjectGroupPython] G4_N_PROPYL_ALCOHOL  label="G4_N-PROPYL_ALCOHOL"  # scripted group (container) (typed FeaturePython)
  Dunit = g/cm3
  Dvalue = 0.8035
  Group = -> [C_element098,H_element090,O_element086]
  conduct = 2
  density = 1
  expand = 3
  formula = G4_N-PROPYL_ALCOHOL
  name = G4_N-PROPYL_ALCOHOL
  specific = 4
FEATURE [App::DocumentObjectGroupPython] C_element099  label="C_element : 057"  # scripted group (container) (typed FeaturePython)
  n = 5
  ref = C_element
FEATURE [App::DocumentObjectGroupPython] H_element091  label="H_element : 052"  # scripted group (container) (typed FeaturePython)
  n = 5
  ref = H_element
FEATURE [App::DocumentObjectGroupPython] N_element038  label="N_element : 017"  # scripted group (container) (typed FeaturePython)
  n = 1
  ref = N_element
FEATURE [App::DocumentObjectGroupPython] G4_PYRIDINE  # scripted group (container) (typed FeaturePython)
  Dunit = g/cm3
  Dvalue = 0.9819
  Group = -> [C_element099,H_element091,N_element038]
  conduct = 2
  density = 1
  expand = 3
  formula = G4_PYRIDINE
  name = G4_PYRIDINE
  specific = 4
FEATURE [App::DocumentObjectGroupPython] H_element092  label="H_element : 0.144"  # scripted group (container) (typed FeaturePython)
  n = 0.143711
FEATURE [App::DocumentObjectGroupPython] C_element100  label="C_element : 0.856"  # scripted group (container) (typed FeaturePython)
  n = 0.856289
FEATURE [App::DocumentObjectGroupPython] G4_RUBBER_BUTYL  # scripted group (container) (typed FeaturePython)
  Dunit = g/cm3
  Dvalue = 0.92
  Group = -> [H_element092,C_element100]
  conduct = 2
  density = 1
  expand = 3
  formula = G4_RUBBER_BUTYL
  name = G4_RUBBER_BUTYL
  specific = 4
FEATURE [App::DocumentObjectGroupPython] H_element093  label="H_element : 0.118"  # scripted group (container) (typed FeaturePython)
  n = 0.118371
FEATURE [App::DocumentObjectGroupPython] C_element101  label="C_element : 0.882"  # scripted group (container) (typed FeaturePython)
  n = 0.881629
FEATURE [App::DocumentObjectGroupPython] G4_RUBBER_NATURAL  # scripted group (container) (typed FeaturePython)
  Dunit = g/cm3
  Dvalue = 0.92
  Group = -> [H_element093,C_element101]
  conduct = 2
  density = 1
  expand = 3
  formula = G4_RUBBER_NATURAL
  name = G4_RUBBER_NATURAL
  specific = 4
FEATURE [App::DocumentObjectGroupPython] H_element094  label="H_element : 0.145"  # scripted group (container) (typed FeaturePython)
  n = 0.05692
FEATURE [App::DocumentObjectGroupPython] C_element102  label="C_element : 0.543"  # scripted group (container) (typed FeaturePython)
  n = 0.542646
FEATURE [App::DocumentObjectGroupPython] Cl_element021  label="Cl_element : 0.400"  # scripted group (container) (typed FeaturePython)
  n = 0.400434
FEATURE [App::DocumentObjectGroupPython] G4_RUBBER_NEOPRENE  # scripted group (container) (typed FeaturePython)
  Dunit = g/cm3
  Dvalue = 1.23
  Group = -> [H_element094,C_element102,Cl_element021]
  conduct = 2
  density = 1
  expand = 3
  formula = G4_RUBBER_NEOPRENE
  name = G4_RUBBER_NEOPRENE
  specific = 4
FEATURE [App::DocumentObjectGroupPython] Si_element006  label="Si_element : 1"  # scripted group (container) (typed FeaturePython)
  n = 1
  ref = Si_element
FEATURE [App::DocumentObjectGroupPython] O_element087  label="O_element : 048"  # scripted group (container) (typed FeaturePython)
  n = 2
  ref = O_element
FEATURE [App::DocumentObjectGroupPython] G4_SILICON_DIOXIDE001  label="G4_SILICON_DIOXIDE"  # scripted group (container) (typed FeaturePython)
  Dunit = g/cm3
  Dvalue = 2.32
  Group = -> [Si_element006,O_element087]
  conduct = 2
  density = 1
  expand = 3
  formula = G4_SILICON_DIOXIDE
  name = G4_SILICON_DIOXIDE
  specific = 4
FEATURE [App::DocumentObjectGroupPython] Ag_element002  label="Ag_element : 1"  # scripted group (container) (typed FeaturePython)
  n = 1
  ref = Ag_element
FEATURE [App::DocumentObjectGroupPython] Br_element005  label="Br_element : 003"  # scripted group (container) (typed FeaturePython)
  n = 1
  ref = Br_element
FEATURE [App::DocumentObjectGroupPython] G4_SILVER_BROMIDE  # scripted group (container) (typed FeaturePython)
  Dunit = g/cm3
  Dvalue = 6.473
  Group = -> [Ag_element002,Br_element005]
  conduct = 2
  density = 1
  expand = 3
  formula = G4_SILVER_BROMIDE
  name = G4_SILVER_BROMIDE
  specific = 4
FEATURE [App::DocumentObjectGroupPython] Ag_element003  label="Ag_element : 002"  # scripted group (container) (typed FeaturePython)
  n = 1
  ref = Ag_element
FEATURE [App::DocumentObjectGroupPython] Cl_element022  label="Cl_element : 011"  # scripted group (container) (typed FeaturePython)
  n = 1
  ref = Cl_element
FEATURE [App::DocumentObjectGroupPython] G4_SILVER_CHLORIDE  # scripted group (container) (typed FeaturePython)
  Dunit = g/cm3
  Dvalue = 5.56
  Group = -> [Ag_element003,Cl_element022]
  conduct = 2
  density = 1
  expand = 3
  formula = G4_SILVER_CHLORIDE
  name = G4_SILVER_CHLORIDE
  specific = 4
FEATURE [App::DocumentObjectGroupPython] Br_element006  label="Br_element : 0.423"  # scripted group (container) (typed FeaturePython)
  n = 0.422895
FEATURE [App::DocumentObjectGroupPython] Ag_element004  label="Ag_element : 0.574"  # scripted group (container) (typed FeaturePython)
  n = 0.573748
FEATURE [App::DocumentObjectGroupPython] I_element007  label="I_element : 0.649"  # scripted group (container) (typed FeaturePython)
  n = 0.003357
FEATURE [App::DocumentObjectGroupPython] G4_SILVER_HALIDES  # scripted group (container) (typed FeaturePython)
  Dunit = g/cm3
  Dvalue = 6.47
  Group = -> [Br_element006,Ag_element004,I_element007]
  conduct = 2
  density = 1
  expand = 3
  formula = G4_SILVER_HALIDES
  name = G4_SILVER_HALIDES
  specific = 4
FEATURE [App::DocumentObjectGroupPython] Ag_element005  label="Ag_element : 003"  # scripted group (container) (typed FeaturePython)
  n = 1
  ref = Ag_element
FEATURE [App::DocumentObjectGroupPython] I_element008  label="I_element : 004"  # scripted group (container) (typed FeaturePython)
  n = 1
  ref = I_element
FEATURE [App::DocumentObjectGroupPython] G4_SILVER_IODIDE  # scripted group (container) (typed FeaturePython)
  Dunit = g/cm3
  Dvalue = 6.01
  Group = -> [Ag_element005,I_element008]
  conduct = 2
  density = 1
  expand = 3
  formula = G4_SILVER_IODIDE
  name = G4_SILVER_IODIDE
  specific = 4
FEATURE [App::DocumentObjectGroupPython] H_element095  label="H_element : 0.100"  # scripted group (container) (typed FeaturePython)
  n = 0.1
FEATURE [App::DocumentObjectGroupPython] C_element103  label="C_element : 0.204"  # scripted group (container) (typed FeaturePython)
  n = 0.204
FEATURE [App::DocumentObjectGroupPython] N_element039  label="N_element : 0.759"  # scripted group (container) (typed FeaturePython)
  n = 0.042
FEATURE [App::DocumentObjectGroupPython] O_element088  label="O_element : 0.645"  # scripted group (container) (typed FeaturePython)
  n = 0.645
FEATURE [App::DocumentObjectGroupPython] Na_element013  label="Na_element : 0.100"  # scripted group (container) (typed FeaturePython)
  n = 0.002
FEATURE [App::DocumentObjectGroupPython] P_element009  label="P_element : 0.107"  # scripted group (container) (typed FeaturePython)
  n = 0.001
FEATURE [App::DocumentObjectGroupPython] S_element020  label="S_element : 0.021"  # scripted group (container) (typed FeaturePython)
  n = 0.002
FEATURE [App::DocumentObjectGroupPython] Cl_element023  label="Cl_element : 0.590"  # scripted group (container) (typed FeaturePython)
  n = 0.003
FEATURE [App::DocumentObjectGroupPython] K_element010  label="K_element : 0.001"  # scripted group (container) (typed FeaturePython)
  n = 0.001
FEATURE [App::DocumentObjectGroupPython] G4_SKIN_ICRP  # scripted group (container) (typed FeaturePython)
  Dunit = g/cm3
  Dvalue = 1.09
  Group = -> [H_element095,C_element103,N_element039,O_element088,Na_element013,P_element009,S_element020,Cl_element023,K_element010]
  conduct = 2
  density = 1
  expand = 3
  formula = G4_SKIN_ICRP
  name = G4_SKIN_ICRP
  specific = 4
FEATURE [App::DocumentObjectGroupPython] Na_element014  label="Na_element : 2"  # scripted group (container) (typed FeaturePython)
  n = 2
  ref = Na_element
FEATURE [App::DocumentObjectGroupPython] C_element104  label="C_element : 058"  # scripted group (container) (typed FeaturePython)
  n = 1
  ref = C_element
FEATURE [App::DocumentObjectGroupPython] O_element089  label="O_element : 049"  # scripted group (container) (typed FeaturePython)
  n = 3
  ref = O_element
FEATURE [App::DocumentObjectGroupPython] G4_SODIUM_CARBONATE  # scripted group (container) (typed FeaturePython)
  Dunit = g/cm3
  Dvalue = 2.532
  Group = -> [Na_element014,C_element104,O_element089]
  conduct = 2
  density = 1
  expand = 3
  formula = G4_SODIUM_CARBONATE
  name = G4_SODIUM_CARBONATE
  specific = 4
FEATURE [App::DocumentObjectGroupPython] Na_element015  label="Na_element : 1"  # scripted group (container) (typed FeaturePython)
  n = 1
  ref = Na_element
FEATURE [App::DocumentObjectGroupPython] I_element009  label="I_element : 005"  # scripted group (container) (typed FeaturePython)
  n = 1
  ref = I_element
FEATURE [App::DocumentObjectGroupPython] G4_SODIUM_IODIDE  # scripted group (container) (typed FeaturePython)
  Dunit = g/cm3
  Dvalue = 3.667
  Group = -> [Na_element015,I_element009]
  conduct = 2
  density = 1
  expand = 3
  formula = G4_SODIUM_IODIDE
  name = G4_SODIUM_IODIDE
  specific = 4
FEATURE [App::DocumentObjectGroupPython] Na_element016  label="Na_element : 003"  # scripted group (container) (typed FeaturePython)
  n = 2
  ref = Na_element
FEATURE [App::DocumentObjectGroupPython] O_element090  label="O_element : 050"  # scripted group (container) (typed FeaturePython)
  n = 1
  ref = O_element
FEATURE [App::DocumentObjectGroupPython] G4_SODIUM_MONOXIDE  # scripted group (container) (typed FeaturePython)
  Dunit = g/cm3
  Dvalue = 2.27
  Group = -> [Na_element016,O_element090]
  conduct = 2
  density = 1
  expand = 3
  formula = G4_SODIUM_MONOXIDE
  name = G4_SODIUM_MONOXIDE
  specific = 4
FEATURE [App::DocumentObjectGroupPython] Na_element017  label="Na_element : 004"  # scripted group (container) (typed FeaturePython)
  n = 1
  ref = Na_element
FEATURE [App::DocumentObjectGroupPython] N_element040  label="N_element : 018"  # scripted group (container) (typed FeaturePython)
  n = 1
  ref = N_element
FEATURE [App::DocumentObjectGroupPython] O_element091  label="O_element : 051"  # scripted group (container) (typed FeaturePython)
  n = 3
  ref = O_element
FEATURE [App::DocumentObjectGroupPython] G4_SODIUM_NITRATE  # scripted group (container) (typed FeaturePython)
  Dunit = g/cm3
  Dvalue = 2.261
  Group = -> [Na_element017,N_element040,O_element091]
  conduct = 2
  density = 1
  expand = 3
  formula = G4_SODIUM_NITRATE
  name = G4_SODIUM_NITRATE
  specific = 4
FEATURE [App::DocumentObjectGroupPython] C_element105  label="C_element : 059"  # scripted group (container) (typed FeaturePython)
  n = 14
  ref = C_element
FEATURE [App::DocumentObjectGroupPython] H_element096  label="H_element : 053"  # scripted group (container) (typed FeaturePython)
  n = 12
  ref = H_element
FEATURE [App::DocumentObjectGroupPython] G4_STILBENE  # scripted group (container) (typed FeaturePython)
  Dunit = g/cm3
  Dvalue = 0.9707
  Group = -> [C_element105,H_element096]
  conduct = 2
  density = 1
  expand = 3
  formula = G4_STILBENE
  name = G4_STILBENE
  specific = 4
FEATURE [App::DocumentObjectGroupPython] C_element106  label="C_element : 12"  # scripted group (container) (typed FeaturePython)
  n = 12
  ref = C_element
FEATURE [App::DocumentObjectGroupPython] H_element097  label="H_element : 22"  # scripted group (container) (typed FeaturePython)
  n = 22
  ref = H_element
FEATURE [App::DocumentObjectGroupPython] O_element092  label="O_element : 11"  # scripted group (container) (typed FeaturePython)
  n = 11
  ref = O_element
FEATURE [App::DocumentObjectGroupPython] G4_SUCROSE  # scripted group (container) (typed FeaturePython)
  Dunit = g/cm3
  Dvalue = 1.5805
  Group = -> [C_element106,H_element097,O_element092]
  conduct = 2
  density = 1
  expand = 3
  formula = G4_SUCROSE
  name = G4_SUCROSE
  specific = 4
FEATURE [App::DocumentObjectGroupPython] C_element107  label="C_element : 18"  # scripted group (container) (typed FeaturePython)
  n = 18
  ref = C_element
FEATURE [App::DocumentObjectGroupPython] H_element098  label="H_element : 054"  # scripted group (container) (typed FeaturePython)
  n = 14
  ref = H_element
FEATURE [App::DocumentObjectGroupPython] G4_TERPHENYL  # scripted group (container) (typed FeaturePython)
  Dunit = g/cm3
  Dvalue = 1.24
  Group = -> [C_element107,H_element098]
  conduct = 2
  density = 1
  expand = 3
  formula = G4_TERPHENYL
  name = G4_TERPHENYL
  specific = 4
FEATURE [App::DocumentObjectGroupPython] H_element099  label="H_element : 0.146"  # scripted group (container) (typed FeaturePython)
  n = 0.106
FEATURE [App::DocumentObjectGroupPython] C_element108  label="C_element : 0.883"  # scripted group (container) (typed FeaturePython)
  n = 0.099
FEATURE [App::DocumentObjectGroupPython] N_element041  label="N_element : 0.020"  # scripted group (container) (typed FeaturePython)
  n = 0.02
FEATURE [App::DocumentObjectGroupPython] O_element093  label="O_element : 0.766"  # scripted group (container) (typed FeaturePython)
  n = 0.766
FEATURE [App::DocumentObjectGroupPython] Na_element018  label="Na_element : 0.101"  # scripted group (container) (typed FeaturePython)
  n = 0.002
FEATURE [App::DocumentObjectGroupPython] P_element010  label="P_element : 0.108"  # scripted group (container) (typed FeaturePython)
  n = 0.001
FEATURE [App::DocumentObjectGroupPython] S_element021  label="S_element : 0.022"  # scripted group (container) (typed FeaturePython)
  n = 0.002
FEATURE [App::DocumentObjectGroupPython] Cl_element024  label="Cl_element : 0.002"  # scripted group (container) (typed FeaturePython)
  n = 0.002
FEATURE [App::DocumentObjectGroupPython] K_element011  label="K_element : 0.017"  # scripted group (container) (typed FeaturePython)
  n = 0.002
FEATURE [App::DocumentObjectGroupPython] G4_TESTIS_ICRP  # scripted group (container) (typed FeaturePython)
  Dunit = g/cm3
  Dvalue = 1.04
  Group = -> [H_element099,C_element108,N_element041,O_element093,Na_element018,P_element010,S_element021,Cl_element024,K_element011]
  conduct = 2
  density = 1
  expand = 3
  formula = G4_TESTIS_ICRP
  name = G4_TESTIS_ICRP
  specific = 4
FEATURE [App::DocumentObjectGroupPython] C_element109  label="C_element : 060"  # scripted group (container) (typed FeaturePython)
  n = 2
  ref = C_element
FEATURE [App::DocumentObjectGroupPython] Cl_element025  label="Cl_element : 012"  # scripted group (container) (typed FeaturePython)
  n = 4
  ref = Cl_element
FEATURE [App::DocumentObjectGroupPython] G4_TETRACHLOROETHYLENE  # scripted group (container) (typed FeaturePython)
  Dunit = g/cm3
  Dvalue = 1.625
  Group = -> [C_element109,Cl_element025]
  conduct = 2
  density = 1
  expand = 3
  formula = G4_TETRACHLOROETHYLENE
  name = G4_TETRACHLOROETHYLENE
  specific = 4
FEATURE [App::DocumentObjectGroupPython] Tl_element001  label="Tl_element : 1"  # scripted group (container) (typed FeaturePython)
  n = 1
  ref = Tl_element
FEATURE [App::DocumentObjectGroupPython] Cl_element026  label="Cl_element : 013"  # scripted group (container) (typed FeaturePython)
  n = 1
  ref = Cl_element
FEATURE [App::DocumentObjectGroupPython] G4_THALLIUM_CHLORIDE  # scripted group (container) (typed FeaturePython)
  Dunit = g/cm3
  Dvalue = 7.004
  Group = -> [Tl_element001,Cl_element026]
  conduct = 2
  density = 1
  expand = 3
  formula = G4_THALLIUM_CHLORIDE
  name = G4_THALLIUM_CHLORIDE
  specific = 4
FEATURE [App::DocumentObjectGroupPython] H_element100  label="H_element : 0.147"  # scripted group (container) (typed FeaturePython)
  n = 0.105
FEATURE [App::DocumentObjectGroupPython] C_element110  label="C_element : 0.256"  # scripted group (container) (typed FeaturePython)
  n = 0.256
FEATURE [App::DocumentObjectGroupPython] N_element042  label="N_element : 0.760"  # scripted group (container) (typed FeaturePython)
  n = 0.027
FEATURE [App::DocumentObjectGroupPython] O_element094  label="O_element : 0.602"  # scripted group (container) (typed FeaturePython)
  n = 0.602
FEATURE [App::DocumentObjectGroupPython] Na_element019  label="Na_element : 0.102"  # scripted group (container) (typed FeaturePython)
  n = 0.001
FEATURE [App::DocumentObjectGroupPython] P_element011  label="P_element : 0.109"  # scripted group (container) (typed FeaturePython)
  n = 0.002
FEATURE [App::DocumentObjectGroupPython] S_element022  label="S_element : 0.023"  # scripted group (container) (typed FeaturePython)
  n = 0.003
FEATURE [App::DocumentObjectGroupPython] Cl_element027  label="Cl_element : 0.591"  # scripted group (container) (typed FeaturePython)
  n = 0.002
FEATURE [App::DocumentObjectGroupPython] K_element012  label="K_element : 0.018"  # scripted group (container) (typed FeaturePython)
  n = 0.002
FEATURE [App::DocumentObjectGroupPython] G4_TISSUE_SOFT_ICRP  # scripted group (container) (typed FeaturePython)
  Dunit = g/cm3
  Dvalue = 1.03
  Group = -> [H_element100,C_element110,N_element042,O_element094,Na_element019,P_element011,S_element022,Cl_element027,K_element012]
  conduct = 2
  density = 1
  expand = 3
  formula = G4_TISSUE_SOFT_ICRP
  name = G4_TISSUE_SOFT_ICRP
  specific = 4
FEATURE [App::DocumentObjectGroupPython] H_element101  label="H_element : 0.148"  # scripted group (container) (typed FeaturePython)
  n = 0.101
FEATURE [App::DocumentObjectGroupPython] C_element111  label="C_element : 0.111"  # scripted group (container) (typed FeaturePython)
  n = 0.111
FEATURE [App::DocumentObjectGroupPython] N_element043  label="N_element : 0.026"  # scripted group (container) (typed FeaturePython)
  n = 0.026
FEATURE [App::DocumentObjectGroupPython] O_element095  label="O_element : 0.762"  # scripted group (container) (typed FeaturePython)
  n = 0.762
FEATURE [App::DocumentObjectGroupPython] G4_TISSUE_SOFT_ICRU_4  label="G4_TISSUE_SOFT_ICRU-4"  # scripted group (container) (typed FeaturePython)
  Dunit = g/cm3
  Dvalue = 1
  Group = -> [H_element101,C_element111,N_element043,O_element095]
  conduct = 2
  density = 1
  expand = 3
  formula = G4_TISSUE_SOFT_ICRU-4
  name = G4_TISSUE_SOFT_ICRU-4
  specific = 4
FEATURE [App::DocumentObjectGroupPython] H_element102  label="H_element : 0.149"  # scripted group (container) (typed FeaturePython)
  n = 0.101869
FEATURE [App::DocumentObjectGroupPython] C_element112  label="C_element : 0.456"  # scripted group (container) (typed FeaturePython)
  n = 0.456179
FEATURE [App::DocumentObjectGroupPython] N_element044  label="N_element : 0.761"  # scripted group (container) (typed FeaturePython)
  n = 0.035172
FEATURE [App::DocumentObjectGroupPython] O_element096  label="O_element : 0.407"  # scripted group (container) (typed FeaturePython)
  n = 0.40678
FEATURE [App::DocumentObjectGroupPython] G4_TISSUE_METHANE  label="G4_TISSUE-METHANE"  # scripted group (container) (typed FeaturePython)
  Dunit = g/cm3
  Dvalue = 0.00106409
  Group = -> [H_element102,C_element112,N_element044,O_element096]
  conduct = 2
  density = 1
  expand = 3
  formula = G4_TISSUE-METHANE
  name = G4_TISSUE-METHANE
  specific = 4
FEATURE [App::DocumentObjectGroupPython] H_element103  label="H_element : 0.103"  # scripted group (container) (typed FeaturePython)
  n = 0.102672
FEATURE [App::DocumentObjectGroupPython] C_element113  label="C_element : 0.569"  # scripted group (container) (typed FeaturePython)
  n = 0.56894
FEATURE [App::DocumentObjectGroupPython] N_element045  label="N_element : 0.762"  # scripted group (container) (typed FeaturePython)
  n = 0.035022
FEATURE [App::DocumentObjectGroupPython] O_element097  label="O_element : 0.293"  # scripted group (container) (typed FeaturePython)
  n = 0.293366
FEATURE [App::DocumentObjectGroupPython] G4_TISSUE_PROPANE  label="G4_TISSUE-PROPANE"  # scripted group (container) (typed FeaturePython)
  Dunit = g/cm3
  Dvalue = 0.00182628
  Group = -> [H_element103,C_element113,N_element045,O_element097]
  conduct = 2
  density = 1
  expand = 3
  formula = G4_TISSUE-PROPANE
  name = G4_TISSUE-PROPANE
  specific = 4
FEATURE [App::DocumentObjectGroupPython] Ti_element003  label="Ti_element : 1"  # scripted group (container) (typed FeaturePython)
  n = 1
  ref = Ti_element
FEATURE [App::DocumentObjectGroupPython] O_element098  label="O_element : 052"  # scripted group (container) (typed FeaturePython)
  n = 2
  ref = O_element
FEATURE [App::DocumentObjectGroupPython] G4_TITANIUM_DIOXIDE  # scripted group (container) (typed FeaturePython)
  Dunit = g/cm3
  Dvalue = 4.26
  Group = -> [Ti_element003,O_element098]
  conduct = 2
  density = 1
  expand = 3
  formula = G4_TITANIUM_DIOXIDE
  name = G4_TITANIUM_DIOXIDE
  specific = 4
FEATURE [App::DocumentObjectGroupPython] C_element114  label="C_element : 061"  # scripted group (container) (typed FeaturePython)
  n = 7
  ref = C_element
FEATURE [App::DocumentObjectGroupPython] H_element104  label="H_element : 055"  # scripted group (container) (typed FeaturePython)
  n = 8
  ref = H_element
FEATURE [App::DocumentObjectGroupPython] G4_TOLUENE  # scripted group (container) (typed FeaturePython)
  Dunit = g/cm3
  Dvalue = 0.8669
  Group = -> [C_element114,H_element104]
  conduct = 2
  density = 1
  expand = 3
  formula = G4_TOLUENE
  name = G4_TOLUENE
  specific = 4
FEATURE [App::DocumentObjectGroupPython] C_element115  label="C_element : 062"  # scripted group (container) (typed FeaturePython)
  n = 2
  ref = C_element
FEATURE [App::DocumentObjectGroupPython] H_element105  label="H_element : 056"  # scripted group (container) (typed FeaturePython)
  n = 1
  ref = H_element
FEATURE [App::DocumentObjectGroupPython] Cl_element028  label="Cl_element : 014"  # scripted group (container) (typed FeaturePython)
  n = 3
  ref = Cl_element
FEATURE [App::DocumentObjectGroupPython] G4_TRICHLOROETHYLENE  # scripted group (container) (typed FeaturePython)
  Dunit = g/cm3
  Dvalue = 1.46
  Group = -> [C_element115,H_element105,Cl_element028]
  conduct = 2
  density = 1
  expand = 3
  formula = G4_TRICHLOROETHYLENE
  name = G4_TRICHLOROETHYLENE
  specific = 4
FEATURE [App::DocumentObjectGroupPython] C_element116  label="C_element : 063"  # scripted group (container) (typed FeaturePython)
  n = 6
  ref = C_element
FEATURE [App::DocumentObjectGroupPython] H_element106  label="H_element : 15"  # scripted group (container) (typed FeaturePython)
  n = 15
  ref = H_element
FEATURE [App::DocumentObjectGroupPython] O_element099  label="O_element : 053"  # scripted group (container) (typed FeaturePython)
  n = 4
  ref = O_element
FEATURE [App::DocumentObjectGroupPython] P_element012  label="P_element : 1"  # scripted group (container) (typed FeaturePython)
  n = 1
  ref = P_element
FEATURE [App::DocumentObjectGroupPython] G4_TRIETHYL_PHOSPHATE  # scripted group (container) (typed FeaturePython)
  Dunit = g/cm3
  Dvalue = 1.07
  Group = -> [C_element116,H_element106,O_element099,P_element012]
  conduct = 2
  density = 1
  expand = 3
  formula = G4_TRIETHYL_PHOSPHATE
  name = G4_TRIETHYL_PHOSPHATE
  specific = 4
FEATURE [App::DocumentObjectGroupPython] W_element003  label="W_element : 003"  # scripted group (container) (typed FeaturePython)
  n = 1
  ref = W_element
FEATURE [App::DocumentObjectGroupPython] F_element017  label="F_element : 6"  # scripted group (container) (typed FeaturePython)
  n = 6
  ref = F_element
FEATURE [App::DocumentObjectGroupPython] G4_TUNGSTEN_HEXAFLUORIDE  # scripted group (container) (typed FeaturePython)
  Dunit = g/cm3
  Dvalue = 2.4
  Group = -> [W_element003,F_element017]
  conduct = 2
  density = 1
  expand = 3
  formula = G4_TUNGSTEN_HEXAFLUORIDE
  name = G4_TUNGSTEN_HEXAFLUORIDE
  specific = 4
FEATURE [App::DocumentObjectGroupPython] U_element001  label="U_element : 1"  # scripted group (container) (typed FeaturePython)
  n = 1
  ref = U_element
FEATURE [App::DocumentObjectGroupPython] C_element117  label="C_element : 064"  # scripted group (container) (typed FeaturePython)
  n = 2
  ref = C_element
FEATURE [App::DocumentObjectGroupPython] G4_URANIUM_DICARBIDE  # scripted group (container) (typed FeaturePython)
  Dunit = g/cm3
  Dvalue = 11.28
  Group = -> [U_element001,C_element117]
  conduct = 2
  density = 1
  expand = 3
  formula = G4_URANIUM_DICARBIDE
  name = G4_URANIUM_DICARBIDE
  specific = 4
FEATURE [App::DocumentObjectGroupPython] U_element002  label="U_element : 002"  # scripted group (container) (typed FeaturePython)
  n = 1
  ref = U_element
FEATURE [App::DocumentObjectGroupPython] C_element118  label="C_element : 065"  # scripted group (container) (typed FeaturePython)
  n = 1
  ref = C_element
FEATURE [App::DocumentObjectGroupPython] G4_URANIUM_MONOCARBIDE  # scripted group (container) (typed FeaturePython)
  Dunit = g/cm3
  Dvalue = 13.63
  Group = -> [U_element002,C_element118]
  conduct = 2
  density = 1
  expand = 3
  formula = G4_URANIUM_MONOCARBIDE
  name = G4_URANIUM_MONOCARBIDE
  specific = 4
FEATURE [App::DocumentObjectGroupPython] U_element003  label="U_element : 003"  # scripted group (container) (typed FeaturePython)
  n = 1
  ref = U_element
FEATURE [App::DocumentObjectGroupPython] O_element100  label="O_element : 054"  # scripted group (container) (typed FeaturePython)
  n = 2
  ref = O_element
FEATURE [App::DocumentObjectGroupPython] G4_URANIUM_OXIDE  # scripted group (container) (typed FeaturePython)
  Dunit = g/cm3
  Dvalue = 10.96
  Group = -> [U_element003,O_element100]
  conduct = 2
  density = 1
  expand = 3
  formula = G4_URANIUM_OXIDE
  name = G4_URANIUM_OXIDE
  specific = 4
FEATURE [App::DocumentObjectGroupPython] C_element119  label="C_element : 066"  # scripted group (container) (typed FeaturePython)
  n = 1
  ref = C_element
FEATURE [App::DocumentObjectGroupPython] H_element107  label="H_element : 057"  # scripted group (container) (typed FeaturePython)
  n = 4
  ref = H_element
FEATURE [App::DocumentObjectGroupPython] N_element046  label="N_element : 019"  # scripted group (container) (typed FeaturePython)
  n = 2
  ref = N_element
FEATURE [App::DocumentObjectGroupPython] O_element101  label="O_element : 055"  # scripted group (container) (typed FeaturePython)
  n = 1
  ref = O_element
FEATURE [App::DocumentObjectGroupPython] G4_UREA  # scripted group (container) (typed FeaturePython)
  Dunit = g/cm3
  Dvalue = 1.323
  Group = -> [C_element119,H_element107,N_element046,O_element101]
  conduct = 2
  density = 1
  expand = 3
  formula = G4_UREA
  name = G4_UREA
  specific = 4
FEATURE [App::DocumentObjectGroupPython] C_element120  label="C_element : 067"  # scripted group (container) (typed FeaturePython)
  n = 5
  ref = C_element
FEATURE [App::DocumentObjectGroupPython] H_element108  label="H_element : 058"  # scripted group (container) (typed FeaturePython)
  n = 11
  ref = H_element
FEATURE [App::DocumentObjectGroupPython] N_element047  label="N_element : 020"  # scripted group (container) (typed FeaturePython)
  n = 1
  ref = N_element
FEATURE [App::DocumentObjectGroupPython] O_element102  label="O_element : 056"  # scripted group (container) (typed FeaturePython)
  n = 2
  ref = O_element
FEATURE [App::DocumentObjectGroupPython] G4_VALINE  # scripted group (container) (typed FeaturePython)
  Dunit = g/cm3
  Dvalue = 1.23
  Group = -> [C_element120,H_element108,N_element047,O_element102]
  conduct = 2
  density = 1
  expand = 3
  formula = G4_VALINE
  name = G4_VALINE
  specific = 4
FEATURE [App::DocumentObjectGroupPython] H_element109  label="H_element : 0.009"  # scripted group (container) (typed FeaturePython)
  n = 0.009417
FEATURE [App::DocumentObjectGroupPython] C_element121  label="C_element : 0.281"  # scripted group (container) (typed FeaturePython)
  n = 0.280555
FEATURE [App::DocumentObjectGroupPython] F_element018  label="F_element : 0.710"  # scripted group (container) (typed FeaturePython)
  n = 0.710028
FEATURE [App::DocumentObjectGroupPython] G4_VITON  # scripted group (container) (typed FeaturePython)
  Dunit = g/cm3
  Dvalue = 1.8
  Group = -> [H_element109,C_element121,F_element018]
  conduct = 2
  density = 1
  expand = 3
  formula = G4_VITON
  name = G4_VITON
  specific = 4
FEATURE [App::DocumentObjectGroupPython] H_element110  label="H_element : 059"  # scripted group (container) (typed FeaturePython)
  n = 2
  ref = H_element
FEATURE [App::DocumentObjectGroupPython] O_element103  label="O_element : 057"  # scripted group (container) (typed FeaturePython)
  n = 1
  ref = O_element
FEATURE [App::DocumentObjectGroupPython] G4_WATER  # scripted group (container) (typed FeaturePython)
  Dunit = g/cm3
  Dvalue = 1
  Group = -> [H_element110,O_element103]
  conduct = 2
  density = 1
  expand = 3
  formula = G4_WATER
  name = G4_WATER
  specific = 4
FEATURE [App::DocumentObjectGroupPython] H_element111  label="H_element : 060"  # scripted group (container) (typed FeaturePython)
  n = 2
  ref = H_element
FEATURE [App::DocumentObjectGroupPython] O_element104  label="O_element : 058"  # scripted group (container) (typed FeaturePython)
  n = 1
  ref = O_element
FEATURE [App::DocumentObjectGroupPython] G4_WATER_VAPOR  # scripted group (container) (typed FeaturePython)
  Dunit = g/cm3
  Dvalue = 0.000756182
  Group = -> [H_element111,O_element104]
  conduct = 2
  density = 1
  expand = 3
  formula = G4_WATER_VAPOR
  name = G4_WATER_VAPOR
  specific = 4
FEATURE [App::DocumentObjectGroupPython] C_element122  label="C_element : 068"  # scripted group (container) (typed FeaturePython)
  n = 8
  ref = C_element
FEATURE [App::DocumentObjectGroupPython] H_element112  label="H_element : 061"  # scripted group (container) (typed FeaturePython)
  n = 10
  ref = H_element
FEATURE [App::DocumentObjectGroupPython] G4_XYLENE  # scripted group (container) (typed FeaturePython)
  Dunit = g/cm3
  Dvalue = 0.87
  Group = -> [C_element122,H_element112]
  conduct = 2
  density = 1
  expand = 3
  formula = G4_XYLENE
  name = G4_XYLENE
  specific = 4
FEATURE [App::DocumentObjectGroupPython] C_element123  label="C_element : 069"  # scripted group (container) (typed FeaturePython)
  n = 1
  ref = C_element
FEATURE [App::DocumentObjectGroupPython] G4_GRAPHITE  # scripted group (container) (typed FeaturePython)
  Dunit = g/cm3
  Dvalue = 2.21
  Group = -> [C_element123]
  conduct = 2
  density = 1
  expand = 3
  formula = G4_GRAPHITE
  name = G4_GRAPHITE
  specific = 4
FEATURE [App::DocumentObjectGroupPython] NIST  # scripted group (container) (typed FeaturePython)
  Group = -> [G4_A_150_TISSUE,G4_ACETONE,G4_ACETYLENE,G4_ADENINE,G4_ADIPOSE_TISSUE_ICRP,G4_AIR001,G4_ALANINE,G4_ALUMINUM_OXIDE,G4_AMBER,G4_AMMONIA,G4_ANILINE,G4_ANTHRACENE,G4_B_100_BONE,G4_BAKELITE,G4_BARIUM_FLUORIDE,G4_BARIUM_SULFATE,G4_BENZENE,G4_BERYLLIUM_OXIDE,G4_BGO,G4_BLOOD_ICRP,G4_BONE_COMPACT_ICRU,G4_BONE_CORTICAL_ICRP,G4_BORON_CARBIDE,G4_BORON_OXIDE,G4_BRAIN_ICRP,G4_BUTANE,G4_N_BUTYL_ALCOHOL,G4_C_552,+152 more]
FEATURE [App::DocumentObjectGroupPython] H_element113  label="H_element : 062"  # scripted group (container) (typed FeaturePython)
  n = 1
  ref = H_element
FEATURE [App::DocumentObjectGroupPython] G4_H  # scripted group (container) (typed FeaturePython)
  Dunit = g/cm3
  Dvalue = 8.3748e-05
  Group = -> [H_element113]
  conduct = 2
  density = 1
  expand = 3
  formula = H
  name = G4_H
  specific = 4
FEATURE [App::DocumentObjectGroupPython] He_element001  label="He_element : 1"  # scripted group (container) (typed FeaturePython)
  n = 1
  ref = He_element
FEATURE [App::DocumentObjectGroupPython] G4_He  # scripted group (container) (typed FeaturePython)
  Dunit = g/cm3
  Dvalue = 0.000166322
  Group = -> [He_element001]
  conduct = 2
  density = 1
  expand = 3
  formula = He
  name = G4_He
  specific = 4
FEATURE [App::DocumentObjectGroupPython] Li_element008  label="Li_element : 008"  # scripted group (container) (typed FeaturePython)
  n = 1
  ref = Li_element
FEATURE [App::DocumentObjectGroupPython] G4_Li  # scripted group (container) (typed FeaturePython)
  Dunit = g/cm3
  Dvalue = 0.534
  Group = -> [Li_element008]
  conduct = 2
  density = 1
  expand = 3
  formula = Li
  name = G4_Li
  specific = 4
FEATURE [App::DocumentObjectGroupPython] Be_element002  label="Be_element : 002"  # scripted group (container) (typed FeaturePython)
  n = 1
  ref = Be_element
FEATURE [App::DocumentObjectGroupPython] G4_Be  # scripted group (container) (typed FeaturePython)
  Dunit = g/cm3
  Dvalue = 1.848
  Group = -> [Be_element002]
  conduct = 2
  density = 1
  expand = 3
  formula = Be
  name = G4_Be
  specific = 4
FEATURE [App::DocumentObjectGroupPython] B_element007  label="B_element : 007"  # scripted group (container) (typed FeaturePython)
  n = 1
  ref = B_element
FEATURE [App::DocumentObjectGroupPython] G4_B  # scripted group (container) (typed FeaturePython)
  Dunit = g/cm3
  Dvalue = 2.37
  Group = -> [B_element007]
  conduct = 2
  density = 1
  expand = 3
  formula = B
  name = G4_B
  specific = 4
FEATURE [App::DocumentObjectGroupPython] C_element124  label="C_element : 070"  # scripted group (container) (typed FeaturePython)
  n = 1
  ref = C_element
FEATURE [App::DocumentObjectGroupPython] G4_C  # scripted group (container) (typed FeaturePython)
  Dunit = g/cm3
  Dvalue = 2
  Group = -> [C_element124]
  conduct = 2
  density = 1
  expand = 3
  formula = C
  name = G4_C
  specific = 4
FEATURE [App::DocumentObjectGroupPython] N_element048  label="N_element : 021"  # scripted group (container) (typed FeaturePython)
  n = 1
  ref = N_element
FEATURE [App::DocumentObjectGroupPython] G4_N  # scripted group (container) (typed FeaturePython)
  Dunit = g/cm3
  Dvalue = 0.0011652
  Group = -> [N_element048]
  conduct = 2
  density = 1
  expand = 3
  formula = N
  name = G4_N
  specific = 4
FEATURE [App::DocumentObjectGroupPython] O_element105  label="O_element : 059"  # scripted group (container) (typed FeaturePython)
  n = 1
  ref = O_element
FEATURE [App::DocumentObjectGroupPython] G4_O  # scripted group (container) (typed FeaturePython)
  Dunit = g/cm3
  Dvalue = 0.00133151
  Group = -> [O_element105]
  conduct = 2
  density = 1
  expand = 3
  formula = O
  name = G4_O
  specific = 4
FEATURE [App::DocumentObjectGroupPython] F_element019  label="F_element : 008"  # scripted group (container) (typed FeaturePython)
  n = 1
  ref = F_element
FEATURE [App::DocumentObjectGroupPython] G4_F  # scripted group (container) (typed FeaturePython)
  Dunit = g/cm3
  Dvalue = 0.00158029
  Group = -> [F_element019]
  conduct = 2
  density = 1
  expand = 3
  formula = F
  name = G4_F
  specific = 4
FEATURE [App::DocumentObjectGroupPython] Ne_element001  label="Ne_element : 1"  # scripted group (container) (typed FeaturePython)
  n = 1
  ref = Ne_element
FEATURE [App::DocumentObjectGroupPython] G4_Ne  # scripted group (container) (typed FeaturePython)
  Dunit = g/cm3
  Dvalue = 0.000838505
  Group = -> [Ne_element001]
  conduct = 2
  density = 1
  expand = 3
  formula = Ne
  name = G4_Ne
  specific = 4
FEATURE [App::DocumentObjectGroupPython] Na_element020  label="Na_element : 005"  # scripted group (container) (typed FeaturePython)
  n = 1
  ref = Na_element
FEATURE [App::DocumentObjectGroupPython] G4_Na  # scripted group (container) (typed FeaturePython)
  Dunit = g/cm3
  Dvalue = 0.971
  Group = -> [Na_element020]
  conduct = 2
  density = 1
  expand = 3
  formula = Na
  name = G4_Na
  specific = 4
FEATURE [App::DocumentObjectGroupPython] Mg_element011  label="Mg_element : 005"  # scripted group (container) (typed FeaturePython)
  n = 1
  ref = Mg_element
FEATURE [App::DocumentObjectGroupPython] G4_Mg  # scripted group (container) (typed FeaturePython)
  Dunit = g/cm3
  Dvalue = 1.74
  Group = -> [Mg_element011]
  conduct = 2
  density = 1
  expand = 3
  formula = Mg
  name = G4_Mg
  specific = 4
FEATURE [App::DocumentObjectGroupPython] Al_element004  label="Al_element : 1"  # scripted group (container) (typed FeaturePython)
  n = 1
  ref = Al_element
FEATURE [App::DocumentObjectGroupPython] G4_Al  # scripted group (container) (typed FeaturePython)
  Dunit = g/cm3
  Dvalue = 2.699
  Group = -> [Al_element004]
  conduct = 2
  density = 1
  expand = 3
  formula = Al
  name = G4_Al
  specific = 4
FEATURE [App::DocumentObjectGroupPython] Si_element007  label="Si_element : 002"  # scripted group (container) (typed FeaturePython)
  n = 1
  ref = Si_element
FEATURE [App::DocumentObjectGroupPython] G4_Si  # scripted group (container) (typed FeaturePython)
  Dunit = g/cm3
  Dvalue = 2.33
  Group = -> [Si_element007]
  conduct = 2
  density = 1
  expand = 3
  formula = Si
  name = G4_Si
  specific = 4
FEATURE [App::DocumentObjectGroupPython] P_element013  label="P_element : 002"  # scripted group (container) (typed FeaturePython)
  n = 1
  ref = P_element
FEATURE [App::DocumentObjectGroupPython] G4_P  # scripted group (container) (typed FeaturePython)
  Dunit = g/cm3
  Dvalue = 2.2
  Group = -> [P_element013]
  conduct = 2
  density = 1
  expand = 3
  formula = P
  name = G4_P
  specific = 4
FEATURE [App::DocumentObjectGroupPython] S_element023  label="S_element : 007"  # scripted group (container) (typed FeaturePython)
  n = 1
  ref = S_element
FEATURE [App::DocumentObjectGroupPython] G4_S  # scripted group (container) (typed FeaturePython)
  Dunit = g/cm3
  Dvalue = 2
  Group = -> [S_element023]
  conduct = 2
  density = 1
  expand = 3
  formula = S
  name = G4_S
  specific = 4
FEATURE [App::DocumentObjectGroupPython] Cl_element029  label="Cl_element : 015"  # scripted group (container) (typed FeaturePython)
  n = 1
  ref = Cl_element
FEATURE [App::DocumentObjectGroupPython] G4_Cl  # scripted group (container) (typed FeaturePython)
  Dunit = g/cm3
  Dvalue = 0.00299473
  Group = -> [Cl_element029]
  conduct = 2
  density = 1
  expand = 3
  formula = Cl
  name = G4_Cl
  specific = 4
FEATURE [App::DocumentObjectGroupPython] Ar_element002  label="Ar_element : 1"  # scripted group (container) (typed FeaturePython)
  n = 1
  ref = Ar_element
FEATURE [App::DocumentObjectGroupPython] G4_Ar  # scripted group (container) (typed FeaturePython)
  Dunit = g/cm3
  Dvalue = 0.00166201
  Group = -> [Ar_element002]
  conduct = 2
  density = 1
  expand = 3
  formula = Ar
  name = G4_Ar
  specific = 4
FEATURE [App::DocumentObjectGroupPython] K_element013  label="K_element : 003"  # scripted group (container) (typed FeaturePython)
  n = 1
  ref = K_element
FEATURE [App::DocumentObjectGroupPython] G4_K  # scripted group (container) (typed FeaturePython)
  Dunit = g/cm3
  Dvalue = 0.862
  Group = -> [K_element013]
  conduct = 2
  density = 1
  expand = 3
  formula = K
  name = G4_K
  specific = 4
FEATURE [App::DocumentObjectGroupPython] Ca_element014  label="Ca_element : 007"  # scripted group (container) (typed FeaturePython)
  n = 1
  ref = Ca_element
FEATURE [App::DocumentObjectGroupPython] G4_Ca  # scripted group (container) (typed FeaturePython)
  Dunit = g/cm3
  Dvalue = 1.55
  Group = -> [Ca_element014]
  conduct = 2
  density = 1
  expand = 3
  formula = Ca
  name = G4_Ca
  specific = 4
FEATURE [App::DocumentObjectGroupPython] Sc_element001  label="Sc_element : 1"  # scripted group (container) (typed FeaturePython)
  n = 1
  ref = Sc_element
FEATURE [App::DocumentObjectGroupPython] G4_Sc  # scripted group (container) (typed FeaturePython)
  Dunit = g/cm3
  Dvalue = 2.989
  Group = -> [Sc_element001]
  conduct = 2
  density = 1
  expand = 3
  formula = Sc
  name = G4_Sc
  specific = 4
FEATURE [App::DocumentObjectGroupPython] Ti_element004  label="Ti_element : 002"  # scripted group (container) (typed FeaturePython)
  n = 1
  ref = Ti_element
FEATURE [App::DocumentObjectGroupPython] G4_Ti  # scripted group (container) (typed FeaturePython)
  Dunit = g/cm3
  Dvalue = 4.54
  Group = -> [Ti_element004]
  conduct = 2
  density = 1
  expand = 3
  formula = Ti
  name = G4_Ti
  specific = 4
FEATURE [App::DocumentObjectGroupPython] V_element001  label="V_element : 1"  # scripted group (container) (typed FeaturePython)
  n = 1
  ref = V_element
FEATURE [App::DocumentObjectGroupPython] G4_V  # scripted group (container) (typed FeaturePython)
  Dunit = g/cm3
  Dvalue = 6.11
  Group = -> [V_element001]
  conduct = 2
  density = 1
  expand = 3
  formula = V
  name = G4_V
  specific = 4
FEATURE [App::DocumentObjectGroupPython] Cr_element001  label="Cr_element : 1"  # scripted group (container) (typed FeaturePython)
  n = 1
  ref = Cr_element
FEATURE [App::DocumentObjectGroupPython] G4_Cr  # scripted group (container) (typed FeaturePython)
  Dunit = g/cm3
  Dvalue = 7.18
  Group = -> [Cr_element001]
  conduct = 2
  density = 1
  expand = 3
  formula = Cr
  name = G4_Cr
  specific = 4
FEATURE [App::DocumentObjectGroupPython] Mn_element001  label="Mn_element : 1"  # scripted group (container) (typed FeaturePython)
  n = 1
  ref = Mn_element
FEATURE [App::DocumentObjectGroupPython] G4_Mn  # scripted group (container) (typed FeaturePython)
  Dunit = g/cm3
  Dvalue = 7.44
  Group = -> [Mn_element001]
  conduct = 2
  density = 1
  expand = 3
  formula = Mn
  name = G4_Mn
  specific = 4
FEATURE [App::DocumentObjectGroupPython] Fe_element007  label="Fe_element : 004"  # scripted group (container) (typed FeaturePython)
  n = 1
  ref = Fe_element
FEATURE [App::DocumentObjectGroupPython] G4_Fe  # scripted group (container) (typed FeaturePython)
  Dunit = g/cm3
  Dvalue = 7.874
  Group = -> [Fe_element007]
  conduct = 2
  density = 1
  expand = 3
  formula = Fe
  name = G4_Fe
  specific = 4
FEATURE [App::DocumentObjectGroupPython] Co_element001  label="Co_element : 1"  # scripted group (container) (typed FeaturePython)
  n = 1
  ref = Co_element
FEATURE [App::DocumentObjectGroupPython] G4_Co  # scripted group (container) (typed FeaturePython)
  Dunit = g/cm3
  Dvalue = 8.9
  Group = -> [Co_element001]
  conduct = 2
  density = 1
  expand = 3
  formula = Co
  name = G4_Co
  specific = 4
FEATURE [App::DocumentObjectGroupPython] Ni_element001  label="Ni_element : 1"  # scripted group (container) (typed FeaturePython)
  n = 1
  ref = Ni_element
FEATURE [App::DocumentObjectGroupPython] G4_Ni  # scripted group (container) (typed FeaturePython)
  Dunit = g/cm3
  Dvalue = 8.902
  Group = -> [Ni_element001]
  conduct = 2
  density = 1
  expand = 3
  formula = Ni
  name = G4_Ni
  specific = 4
FEATURE [App::DocumentObjectGroupPython] Cu_element001  label="Cu_element : 1"  # scripted group (container) (typed FeaturePython)
  n = 1
  ref = Cu_element
FEATURE [App::DocumentObjectGroupPython] G4_Cu  # scripted group (container) (typed FeaturePython)
  Dunit = g/cm3
  Dvalue = 8.96
  Group = -> [Cu_element001]
  conduct = 2
  density = 1
  expand = 3
  formula = Cu
  name = G4_Cu
  specific = 4
FEATURE [App::DocumentObjectGroupPython] Zn_element001  label="Zn_element : 1"  # scripted group (container) (typed FeaturePython)
  n = 1
  ref = Zn_element
FEATURE [App::DocumentObjectGroupPython] G4_Zn  # scripted group (container) (typed FeaturePython)
  Dunit = g/cm3
  Dvalue = 7.133
  Group = -> [Zn_element001]
  conduct = 2
  density = 1
  expand = 3
  formula = Zn
  name = G4_Zn
  specific = 4
FEATURE [App::DocumentObjectGroupPython] Ga_element002  label="Ga_element : 002"  # scripted group (container) (typed FeaturePython)
  n = 1
  ref = Ga_element
FEATURE [App::DocumentObjectGroupPython] G4_Ga  # scripted group (container) (typed FeaturePython)
  Dunit = g/cm3
  Dvalue = 5.904
  Group = -> [Ga_element002]
  conduct = 2
  density = 1
  expand = 3
  formula = Ga
  name = G4_Ga
  specific = 4
FEATURE [App::DocumentObjectGroupPython] Ge_element002  label="Ge_element : 1"  # scripted group (container) (typed FeaturePython)
  n = 1
  ref = Ge_element
FEATURE [App::DocumentObjectGroupPython] G4_Ge  # scripted group (container) (typed FeaturePython)
  Dunit = g/cm3
  Dvalue = 5.323
  Group = -> [Ge_element002]
  conduct = 2
  density = 1
  expand = 3
  formula = Ge
  name = G4_Ge
  specific = 4
FEATURE [App::DocumentObjectGroupPython] As_element003  label="As_element : 002"  # scripted group (container) (typed FeaturePython)
  n = 1
  ref = As_element
FEATURE [App::DocumentObjectGroupPython] G4_As  # scripted group (container) (typed FeaturePython)
  Dunit = g/cm3
  Dvalue = 5.73
  Group = -> [As_element003]
  conduct = 2
  density = 1
  expand = 3
  formula = As
  name = G4_As
  specific = 4
FEATURE [App::DocumentObjectGroupPython] Se_element001  label="Se_element : 1"  # scripted group (container) (typed FeaturePython)
  n = 1
  ref = Se_element
FEATURE [App::DocumentObjectGroupPython] G4_Se  # scripted group (container) (typed FeaturePython)
  Dunit = g/cm3
  Dvalue = 4.5
  Group = -> [Se_element001]
  conduct = 2
  density = 1
  expand = 3
  formula = Se
  name = G4_Se
  specific = 4
FEATURE [App::DocumentObjectGroupPython] Br_element007  label="Br_element : 004"  # scripted group (container) (typed FeaturePython)
  n = 1
  ref = Br_element
FEATURE [App::DocumentObjectGroupPython] G4_Br  # scripted group (container) (typed FeaturePython)
  Dunit = g/cm3
  Dvalue = 0.0070721
  Group = -> [Br_element007]
  conduct = 2
  density = 1
  expand = 3
  formula = Br
  name = G4_Br
  specific = 4
FEATURE [App::DocumentObjectGroupPython] Kr_element001  label="Kr_element : 1"  # scripted group (container) (typed FeaturePython)
  n = 1
  ref = Kr_element
FEATURE [App::DocumentObjectGroupPython] G4_Kr  # scripted group (container) (typed FeaturePython)
  Dunit = g/cm3
  Dvalue = 0.00347832
  Group = -> [Kr_element001]
  conduct = 2
  density = 1
  expand = 3
  formula = Kr
  name = G4_Kr
  specific = 4
FEATURE [App::DocumentObjectGroupPython] Rb_element001  label="Rb_element : 1"  # scripted group (container) (typed FeaturePython)
  n = 1
  ref = Rb_element
FEATURE [App::DocumentObjectGroupPython] G4_Rb  # scripted group (container) (typed FeaturePython)
  Dunit = g/cm3
  Dvalue = 1.532
  Group = -> [Rb_element001]
  conduct = 2
  density = 1
  expand = 3
  formula = Rb
  name = G4_Rb
  specific = 4
FEATURE [App::DocumentObjectGroupPython] Sr_element001  label="Sr_element : 1"  # scripted group (container) (typed FeaturePython)
  n = 1
  ref = Sr_element
FEATURE [App::DocumentObjectGroupPython] G4_Sr  # scripted group (container) (typed FeaturePython)
  Dunit = g/cm3
  Dvalue = 2.54
  Group = -> [Sr_element001]
  conduct = 2
  density = 1
  expand = 3
  formula = Sr
  name = G4_Sr
  specific = 4
FEATURE [App::DocumentObjectGroupPython] Y_element001  label="Y_element : 1"  # scripted group (container) (typed FeaturePython)
  n = 1
  ref = Y_element
FEATURE [App::DocumentObjectGroupPython] G4_Y  # scripted group (container) (typed FeaturePython)
  Dunit = g/cm3
  Dvalue = 4.469
  Group = -> [Y_element001]
  conduct = 2
  density = 1
  expand = 3
  formula = Y
  name = G4_Y
  specific = 4
FEATURE [App::DocumentObjectGroupPython] Zr_element001  label="Zr_element : 1"  # scripted group (container) (typed FeaturePython)
  n = 1
  ref = Zr_element
FEATURE [App::DocumentObjectGroupPython] G4_Zr  # scripted group (container) (typed FeaturePython)
  Dunit = g/cm3
  Dvalue = 6.506
  Group = -> [Zr_element001]
  conduct = 2
  density = 1
  expand = 3
  formula = Zr
  name = G4_Zr
  specific = 4
FEATURE [App::DocumentObjectGroupPython] Nb_element001  label="Nb_element : 1"  # scripted group (container) (typed FeaturePython)
  n = 1
  ref = Nb_element
FEATURE [App::DocumentObjectGroupPython] G4_Nb  # scripted group (container) (typed FeaturePython)
  Dunit = g/cm3
  Dvalue = 8.57
  Group = -> [Nb_element001]
  conduct = 2
  density = 1
  expand = 3
  formula = Nb
  name = G4_Nb
  specific = 4
FEATURE [App::DocumentObjectGroupPython] Mo_element001  label="Mo_element : 1"  # scripted group (container) (typed FeaturePython)
  n = 1
  ref = Mo_element
FEATURE [App::DocumentObjectGroupPython] G4_Mo  # scripted group (container) (typed FeaturePython)
  Dunit = g/cm3
  Dvalue = 10.22
  Group = -> [Mo_element001]
  conduct = 2
  density = 1
  expand = 3
  formula = Mo
  name = G4_Mo
  specific = 4
FEATURE [App::DocumentObjectGroupPython] Tc_element001  label="Tc_element : 1"  # scripted group (container) (typed FeaturePython)
  n = 1
  ref = Tc_element
FEATURE [App::DocumentObjectGroupPython] G4_Tc  # scripted group (container) (typed FeaturePython)
  Dunit = g/cm3
  Dvalue = 11.5
  Group = -> [Tc_element001]
  conduct = 2
  density = 1
  expand = 3
  formula = Tc
  name = G4_Tc
  specific = 4
FEATURE [App::DocumentObjectGroupPython] Ru_element001  label="Ru_element : 1"  # scripted group (container) (typed FeaturePython)
  n = 1
  ref = Ru_element
FEATURE [App::DocumentObjectGroupPython] G4_Ru  # scripted group (container) (typed FeaturePython)
  Dunit = g/cm3
  Dvalue = 12.41
  Group = -> [Ru_element001]
  conduct = 2
  density = 1
  expand = 3
  formula = Ru
  name = G4_Ru
  specific = 4
FEATURE [App::DocumentObjectGroupPython] Rh_element001  label="Rh_element : 1"  # scripted group (container) (typed FeaturePython)
  n = 1
  ref = Rh_element
FEATURE [App::DocumentObjectGroupPython] G4_Rh  # scripted group (container) (typed FeaturePython)
  Dunit = g/cm3
  Dvalue = 12.41
  Group = -> [Rh_element001]
  conduct = 2
  density = 1
  expand = 3
  formula = Rh
  name = G4_Rh
  specific = 4
FEATURE [App::DocumentObjectGroupPython] Pd_element001  label="Pd_element : 1"  # scripted group (container) (typed FeaturePython)
  n = 1
  ref = Pd_element
FEATURE [App::DocumentObjectGroupPython] G4_Pd  # scripted group (container) (typed FeaturePython)
  Dunit = g/cm3
  Dvalue = 12.02
  Group = -> [Pd_element001]
  conduct = 2
  density = 1
  expand = 3
  formula = Pd
  name = G4_Pd
  specific = 4
FEATURE [App::DocumentObjectGroupPython] Ag_element006  label="Ag_element : 004"  # scripted group (container) (typed FeaturePython)
  n = 1
  ref = Ag_element
FEATURE [App::DocumentObjectGroupPython] G4_Ag  # scripted group (container) (typed FeaturePython)
  Dunit = g/cm3
  Dvalue = 10.5
  Group = -> [Ag_element006]
  conduct = 2
  density = 1
  expand = 3
  formula = Ag
  name = G4_Ag
  specific = 4
FEATURE [App::DocumentObjectGroupPython] Cd_element003  label="Cd_element : 003"  # scripted group (container) (typed FeaturePython)
  n = 1
  ref = Cd_element
FEATURE [App::DocumentObjectGroupPython] G4_Cd  # scripted group (container) (typed FeaturePython)
  Dunit = g/cm3
  Dvalue = 8.65
  Group = -> [Cd_element003]
  conduct = 2
  density = 1
  expand = 3
  formula = Cd
  name = G4_Cd
  specific = 4
FEATURE [App::DocumentObjectGroupPython] In_element001  label="In_element : 1"  # scripted group (container) (typed FeaturePython)
  n = 1
  ref = In_element
FEATURE [App::DocumentObjectGroupPython] G4_In  # scripted group (container) (typed FeaturePython)
  Dunit = g/cm3
  Dvalue = 7.31
  Group = -> [In_element001]
  conduct = 2
  density = 1
  expand = 3
  formula = In
  name = G4_In
  specific = 4
FEATURE [App::DocumentObjectGroupPython] Sn_element001  label="Sn_element : 1"  # scripted group (container) (typed FeaturePython)
  n = 1
  ref = Sn_element
FEATURE [App::DocumentObjectGroupPython] G4_Sn  # scripted group (container) (typed FeaturePython)
  Dunit = g/cm3
  Dvalue = 7.31
  Group = -> [Sn_element001]
  conduct = 2
  density = 1
  expand = 3
  formula = Sn
  name = G4_Sn
  specific = 4
FEATURE [App::DocumentObjectGroupPython] Sb_element001  label="Sb_element : 1"  # scripted group (container) (typed FeaturePython)
  n = 1
  ref = Sb_element
FEATURE [App::DocumentObjectGroupPython] G4_Sb  # scripted group (container) (typed FeaturePython)
  Dunit = g/cm3
  Dvalue = 6.691
  Group = -> [Sb_element001]
  conduct = 2
  density = 1
  expand = 3
  formula = Sb
  name = G4_Sb
  specific = 4
FEATURE [App::DocumentObjectGroupPython] Te_element002  label="Te_element : 002"  # scripted group (container) (typed FeaturePython)
  n = 1
  ref = Te_element
FEATURE [App::DocumentObjectGroupPython] G4_Te  # scripted group (container) (typed FeaturePython)
  Dunit = g/cm3
  Dvalue = 6.24
  Group = -> [Te_element002]
  conduct = 2
  density = 1
  expand = 3
  formula = Te
  name = G4_Te
  specific = 4
FEATURE [App::DocumentObjectGroupPython] I_element010  label="I_element : 006"  # scripted group (container) (typed FeaturePython)
  n = 1
  ref = I_element
FEATURE [App::DocumentObjectGroupPython] G4_I  # scripted group (container) (typed FeaturePython)
  Dunit = g/cm3
  Dvalue = 4.93
  Group = -> [I_element010]
  conduct = 2
  density = 1
  expand = 3
  formula = I
  name = G4_I
  specific = 4
FEATURE [App::DocumentObjectGroupPython] Xe_element001  label="Xe_element : 1"  # scripted group (container) (typed FeaturePython)
  n = 1
  ref = Xe_element
FEATURE [App::DocumentObjectGroupPython] G4_Xe  # scripted group (container) (typed FeaturePython)
  Dunit = g/cm3
  Dvalue = 0.00548536
  Group = -> [Xe_element001]
  conduct = 2
  density = 1
  expand = 3
  formula = Xe
  name = G4_Xe
  specific = 4
FEATURE [App::DocumentObjectGroupPython] Cs_element003  label="Cs_element : 003"  # scripted group (container) (typed FeaturePython)
  n = 1
  ref = Cs_element
FEATURE [App::DocumentObjectGroupPython] G4_Cs  # scripted group (container) (typed FeaturePython)
  Dunit = g/cm3
  Dvalue = 1.873
  Group = -> [Cs_element003]
  conduct = 2
  density = 1
  expand = 3
  formula = Cs
  name = G4_Cs
  specific = 4
FEATURE [App::DocumentObjectGroupPython] Ba_element003  label="Ba_element : 003"  # scripted group (container) (typed FeaturePython)
  n = 1
  ref = Ba_element
FEATURE [App::DocumentObjectGroupPython] G4_Ba  # scripted group (container) (typed FeaturePython)
  Dunit = g/cm3
  Dvalue = 3.5
  Group = -> [Ba_element003]
  conduct = 2
  density = 1
  expand = 3
  formula = Ba
  name = G4_Ba
  specific = 4
FEATURE [App::DocumentObjectGroupPython] La_element003  label="La_element : 003"  # scripted group (container) (typed FeaturePython)
  n = 1
  ref = La_element
FEATURE [App::DocumentObjectGroupPython] G4_La  # scripted group (container) (typed FeaturePython)
  Dunit = g/cm3
  Dvalue = 6.154
  Group = -> [La_element003]
  conduct = 2
  density = 1
  expand = 3
  formula = La
  name = G4_La
  specific = 4
FEATURE [App::DocumentObjectGroupPython] Ce_element002  label="Ce_element : 1"  # scripted group (container) (typed FeaturePython)
  n = 1
  ref = Ce_element
FEATURE [App::DocumentObjectGroupPython] G4_Ce  # scripted group (container) (typed FeaturePython)
  Dunit = g/cm3
  Dvalue = 6.657
  Group = -> [Ce_element002]
  conduct = 2
  density = 1
  expand = 3
  formula = Ce
  name = G4_Ce
  specific = 4
FEATURE [App::DocumentObjectGroupPython] Pr_element001  label="Pr_element : 1"  # scripted group (container) (typed FeaturePython)
  n = 1
  ref = Pr_element
FEATURE [App::DocumentObjectGroupPython] G4_Pr  # scripted group (container) (typed FeaturePython)
  Dunit = g/cm3
  Dvalue = 6.71
  Group = -> [Pr_element001]
  conduct = 2
  density = 1
  expand = 3
  formula = Pr
  name = G4_Pr
  specific = 4
FEATURE [App::DocumentObjectGroupPython] Nd_element001  label="Nd_element : 1"  # scripted group (container) (typed FeaturePython)
  n = 1
  ref = Nd_element
FEATURE [App::DocumentObjectGroupPython] G4_Nd  # scripted group (container) (typed FeaturePython)
  Dunit = g/cm3
  Dvalue = 6.9
  Group = -> [Nd_element001]
  conduct = 2
  density = 1
  expand = 3
  formula = Nd
  name = G4_Nd
  specific = 4
FEATURE [App::DocumentObjectGroupPython] Pm_element001  label="Pm_element : 1"  # scripted group (container) (typed FeaturePython)
  n = 1
  ref = Pm_element
FEATURE [App::DocumentObjectGroupPython] G4_Pm  # scripted group (container) (typed FeaturePython)
  Dunit = g/cm3
  Dvalue = 7.22
  Group = -> [Pm_element001]
  conduct = 2
  density = 1
  expand = 3
  formula = Pm
  name = G4_Pm
  specific = 4
FEATURE [App::DocumentObjectGroupPython] Sm_element001  label="Sm_element : 1"  # scripted group (container) (typed FeaturePython)
  n = 1
  ref = Sm_element
FEATURE [App::DocumentObjectGroupPython] G4_Sm  # scripted group (container) (typed FeaturePython)
  Dunit = g/cm3
  Dvalue = 7.46
  Group = -> [Sm_element001]
  conduct = 2
  density = 1
  expand = 3
  formula = Sm
  name = G4_Sm
  specific = 4
FEATURE [App::DocumentObjectGroupPython] Eu_element001  label="Eu_element : 1"  # scripted group (container) (typed FeaturePython)
  n = 1
  ref = Eu_element
FEATURE [App::DocumentObjectGroupPython] G4_Eu  # scripted group (container) (typed FeaturePython)
  Dunit = g/cm3
  Dvalue = 5.243
  Group = -> [Eu_element001]
  conduct = 2
  density = 1
  expand = 3
  formula = Eu
  name = G4_Eu
  specific = 4
FEATURE [App::DocumentObjectGroupPython] Gd_element002  label="Gd_element : 1"  # scripted group (container) (typed FeaturePython)
  n = 1
  ref = Gd_element
FEATURE [App::DocumentObjectGroupPython] G4_Gd  # scripted group (container) (typed FeaturePython)
  Dunit = g/cm3
  Dvalue = 7.9004
  Group = -> [Gd_element002]
  conduct = 2
  density = 1
  expand = 3
  formula = Gd
  name = G4_Gd
  specific = 4
FEATURE [App::DocumentObjectGroupPython] Tb_element001  label="Tb_element : 1"  # scripted group (container) (typed FeaturePython)
  n = 1
  ref = Tb_element
FEATURE [App::DocumentObjectGroupPython] G4_Tb  # scripted group (container) (typed FeaturePython)
  Dunit = g/cm3
  Dvalue = 8.229
  Group = -> [Tb_element001]
  conduct = 2
  density = 1
  expand = 3
  formula = Tb
  name = G4_Tb
  specific = 4
FEATURE [App::DocumentObjectGroupPython] Dy_element001  label="Dy_element : 1"  # scripted group (container) (typed FeaturePython)
  n = 1
  ref = Dy_element
FEATURE [App::DocumentObjectGroupPython] G4_Dy  # scripted group (container) (typed FeaturePython)
  Dunit = g/cm3
  Dvalue = 8.55
  Group = -> [Dy_element001]
  conduct = 2
  density = 1
  expand = 3
  formula = Dy
  name = G4_Dy
  specific = 4
FEATURE [App::DocumentObjectGroupPython] Ho_element001  label="Ho_element : 1"  # scripted group (container) (typed FeaturePython)
  n = 1
  ref = Ho_element
FEATURE [App::DocumentObjectGroupPython] G4_Ho  # scripted group (container) (typed FeaturePython)
  Dunit = g/cm3
  Dvalue = 8.795
  Group = -> [Ho_element001]
  conduct = 2
  density = 1
  expand = 3
  formula = Ho
  name = G4_Ho
  specific = 4
FEATURE [App::DocumentObjectGroupPython] Er_element001  label="Er_element : 1"  # scripted group (container) (typed FeaturePython)
  n = 1
  ref = Er_element
FEATURE [App::DocumentObjectGroupPython] G4_Er  # scripted group (container) (typed FeaturePython)
  Dunit = g/cm3
  Dvalue = 9.066
  Group = -> [Er_element001]
  conduct = 2
  density = 1
  expand = 3
  formula = Er
  name = G4_Er
  specific = 4
FEATURE [App::DocumentObjectGroupPython] Tm_element001  label="Tm_element : 1"  # scripted group (container) (typed FeaturePython)
  n = 1
  ref = Tm_element
FEATURE [App::DocumentObjectGroupPython] G4_Tm  # scripted group (container) (typed FeaturePython)
  Dunit = g/cm3
  Dvalue = 9.321
  Group = -> [Tm_element001]
  conduct = 2
  density = 1
  expand = 3
  formula = Tm
  name = G4_Tm
  specific = 4
FEATURE [App::DocumentObjectGroupPython] Yb_element001  label="Yb_element : 1"  # scripted group (container) (typed FeaturePython)
  n = 1
  ref = Yb_element
FEATURE [App::DocumentObjectGroupPython] G4_Yb  # scripted group (container) (typed FeaturePython)
  Dunit = g/cm3
  Dvalue = 6.73
  Group = -> [Yb_element001]
  conduct = 2
  density = 1
  expand = 3
  formula = Yb
  name = G4_Yb
  specific = 4
FEATURE [App::DocumentObjectGroupPython] Lu_element001  label="Lu_element : 1"  # scripted group (container) (typed FeaturePython)
  n = 1
  ref = Lu_element
FEATURE [App::DocumentObjectGroupPython] G4_Lu  # scripted group (container) (typed FeaturePython)
  Dunit = g/cm3
  Dvalue = 9.84
  Group = -> [Lu_element001]
  conduct = 2
  density = 1
  expand = 3
  formula = Lu
  name = G4_Lu
  specific = 4
FEATURE [App::DocumentObjectGroupPython] Hf_element001  label="Hf_element : 1"  # scripted group (container) (typed FeaturePython)
  n = 1
  ref = Hf_element
FEATURE [App::DocumentObjectGroupPython] G4_Hf  # scripted group (container) (typed FeaturePython)
  Dunit = g/cm3
  Dvalue = 13.31
  Group = -> [Hf_element001]
  conduct = 2
  density = 1
  expand = 3
  formula = Hf
  name = G4_Hf
  specific = 4
FEATURE [App::DocumentObjectGroupPython] Ta_element001  label="Ta_element : 1"  # scripted group (container) (typed FeaturePython)
  n = 1
  ref = Ta_element
FEATURE [App::DocumentObjectGroupPython] G4_Ta  # scripted group (container) (typed FeaturePython)
  Dunit = g/cm3
  Dvalue = 16.654
  Group = -> [Ta_element001]
  conduct = 2
  density = 1
  expand = 3
  formula = Ta
  name = G4_Ta
  specific = 4
FEATURE [App::DocumentObjectGroupPython] W_element004  label="W_element : 004"  # scripted group (container) (typed FeaturePython)
  n = 1
  ref = W_element
FEATURE [App::DocumentObjectGroupPython] G4_W  # scripted group (container) (typed FeaturePython)
  Dunit = g/cm3
  Dvalue = 19.3
  Group = -> [W_element004]
  conduct = 2
  density = 1
  expand = 3
  formula = W
  name = G4_W
  specific = 4
FEATURE [App::DocumentObjectGroupPython] Re_element001  label="Re_element : 1"  # scripted group (container) (typed FeaturePython)
  n = 1
  ref = Re_element
FEATURE [App::DocumentObjectGroupPython] G4_Re  # scripted group (container) (typed FeaturePython)
  Dunit = g/cm3
  Dvalue = 21.02
  Group = -> [Re_element001]
  conduct = 2
  density = 1
  expand = 3
  formula = Re
  name = G4_Re
  specific = 4
FEATURE [App::DocumentObjectGroupPython] Os_element001  label="Os_element : 1"  # scripted group (container) (typed FeaturePython)
  n = 1
  ref = Os_element
FEATURE [App::DocumentObjectGroupPython] G4_Os  # scripted group (container) (typed FeaturePython)
  Dunit = g/cm3
  Dvalue = 22.57
  Group = -> [Os_element001]
  conduct = 2
  density = 1
  expand = 3
  formula = Os
  name = G4_Os
  specific = 4
FEATURE [App::DocumentObjectGroupPython] Ir_element001  label="Ir_element : 1"  # scripted group (container) (typed FeaturePython)
  n = 1
  ref = Ir_element
FEATURE [App::DocumentObjectGroupPython] G4_Ir  # scripted group (container) (typed FeaturePython)
  Dunit = g/cm3
  Dvalue = 22.42
  Group = -> [Ir_element001]
  conduct = 2
  density = 1
  expand = 3
  formula = Ir
  name = G4_Ir
  specific = 4
FEATURE [App::DocumentObjectGroupPython] Pt_element001  label="Pt_element : 1"  # scripted group (container) (typed FeaturePython)
  n = 1
  ref = Pt_element
FEATURE [App::DocumentObjectGroupPython] G4_Pt  # scripted group (container) (typed FeaturePython)
  Dunit = g/cm3
  Dvalue = 21.45
  Group = -> [Pt_element001]
  conduct = 2
  density = 1
  expand = 3
  formula = Pt
  name = G4_Pt
  specific = 4
FEATURE [App::DocumentObjectGroupPython] Au_element001  label="Au_element : 1"  # scripted group (container) (typed FeaturePython)
  n = 1
  ref = Au_element
FEATURE [App::DocumentObjectGroupPython] G4_Au  # scripted group (container) (typed FeaturePython)
  Dunit = g/cm3
  Dvalue = 19.32
  Group = -> [Au_element001]
  conduct = 2
  density = 1
  expand = 3
  formula = Au
  name = G4_Au
  specific = 4
FEATURE [App::DocumentObjectGroupPython] Hg_element002  label="Hg_element : 002"  # scripted group (container) (typed FeaturePython)
  n = 1
  ref = Hg_element
FEATURE [App::DocumentObjectGroupPython] G4_Hg  # scripted group (container) (typed FeaturePython)
  Dunit = g/cm3
  Dvalue = 13.546
  Group = -> [Hg_element002]
  conduct = 2
  density = 1
  expand = 3
  formula = Hg
  name = G4_Hg
  specific = 4
FEATURE [App::DocumentObjectGroupPython] Tl_element002  label="Tl_element : 002"  # scripted group (container) (typed FeaturePython)
  n = 1
  ref = Tl_element
FEATURE [App::DocumentObjectGroupPython] G4_Tl  # scripted group (container) (typed FeaturePython)
  Dunit = g/cm3
  Dvalue = 11.72
  Group = -> [Tl_element002]
  conduct = 2
  density = 1
  expand = 3
  formula = Tl
  name = G4_Tl
  specific = 4
FEATURE [App::DocumentObjectGroupPython] Pb_element003  label="Pb_element : 1"  # scripted group (container) (typed FeaturePython)
  n = 1
  ref = Pb_element
FEATURE [App::DocumentObjectGroupPython] G4_Pb  # scripted group (container) (typed FeaturePython)
  Dunit = g/cm3
  Dvalue = 11.35
  Group = -> [Pb_element003]
  conduct = 2
  density = 1
  expand = 3
  formula = Pb
  name = G4_Pb
  specific = 4
FEATURE [App::DocumentObjectGroupPython] Bi_element002  label="Bi_element : 1"  # scripted group (container) (typed FeaturePython)
  n = 1
  ref = Bi_element
FEATURE [App::DocumentObjectGroupPython] G4_Bi  # scripted group (container) (typed FeaturePython)
  Dunit = g/cm3
  Dvalue = 9.747
  Group = -> [Bi_element002]
  conduct = 2
  density = 1
  expand = 3
  formula = Bi
  name = G4_Bi
  specific = 4
FEATURE [App::DocumentObjectGroupPython] Po_element001  label="Po_element : 1"  # scripted group (container) (typed FeaturePython)
  n = 1
  ref = Po_element
FEATURE [App::DocumentObjectGroupPython] G4_Po  # scripted group (container) (typed FeaturePython)
  Dunit = g/cm3
  Dvalue = 9.32
  Group = -> [Po_element001]
  conduct = 2
  density = 1
  expand = 3
  formula = Po
  name = G4_Po
  specific = 4
FEATURE [App::DocumentObjectGroupPython] At_element001  label="At_element : 1"  # scripted group (container) (typed FeaturePython)
  n = 1
  ref = At_element
FEATURE [App::DocumentObjectGroupPython] G4_At  # scripted group (container) (typed FeaturePython)
  Dunit = g/cm3
  Dvalue = 9.32
  Group = -> [At_element001]
  conduct = 2
  density = 1
  expand = 3
  formula = At
  name = G4_At
  specific = 4
FEATURE [App::DocumentObjectGroupPython] Rn_element001  label="Rn_element : 1"  # scripted group (container) (typed FeaturePython)
  n = 1
  ref = Rn_element
FEATURE [App::DocumentObjectGroupPython] G4_Rn  # scripted group (container) (typed FeaturePython)
  Dunit = g/cm3
  Dvalue = 0.00900662
  Group = -> [Rn_element001]
  conduct = 2
  density = 1
  expand = 3
  formula = Rn
  name = G4_Rn
  specific = 4
FEATURE [App::DocumentObjectGroupPython] Fr_element001  label="Fr_element : 1"  # scripted group (container) (typed FeaturePython)
  n = 1
  ref = Fr_element
FEATURE [App::DocumentObjectGroupPython] G4_Fr  # scripted group (container) (typed FeaturePython)
  Dunit = g/cm3
  Dvalue = 1
  Group = -> [Fr_element001]
  conduct = 2
  density = 1
  expand = 3
  formula = Fr
  name = G4_Fr
  specific = 4
FEATURE [App::DocumentObjectGroupPython] Ra_element001  label="Ra_element : 1"  # scripted group (container) (typed FeaturePython)
  n = 1
  ref = Ra_element
FEATURE [App::DocumentObjectGroupPython] G4_Ra  # scripted group (container) (typed FeaturePython)
  Dunit = g/cm3
  Dvalue = 5
  Group = -> [Ra_element001]
  conduct = 2
  density = 1
  expand = 3
  formula = Ra
  name = G4_Ra
  specific = 4
FEATURE [App::DocumentObjectGroupPython] Ac_element001  label="Ac_element : 1"  # scripted group (container) (typed FeaturePython)
  n = 1
  ref = Ac_element
FEATURE [App::DocumentObjectGroupPython] G4_Ac  # scripted group (container) (typed FeaturePython)
  Dunit = g/cm3
  Dvalue = 10.07
  Group = -> [Ac_element001]
  conduct = 2
  density = 1
  expand = 3
  formula = Ac
  name = G4_Ac
  specific = 4
FEATURE [App::DocumentObjectGroupPython] Th_element001  label="Th_element : 1"  # scripted group (container) (typed FeaturePython)
  n = 1
  ref = Th_element
FEATURE [App::DocumentObjectGroupPython] G4_Th  # scripted group (container) (typed FeaturePython)
  Dunit = g/cm3
  Dvalue = 11.72
  Group = -> [Th_element001]
  conduct = 2
  density = 1
  expand = 3
  formula = Th
  name = G4_Th
  specific = 4
FEATURE [App::DocumentObjectGroupPython] Pa_element001  label="Pa_element : 1"  # scripted group (container) (typed FeaturePython)
  n = 1
  ref = Pa_element
FEATURE [App::DocumentObjectGroupPython] G4_Pa  # scripted group (container) (typed FeaturePython)
  Dunit = g/cm3
  Dvalue = 15.37
  Group = -> [Pa_element001]
  conduct = 2
  density = 1
  expand = 3
  formula = Pa
  name = G4_Pa
  specific = 4
FEATURE [App::DocumentObjectGroupPython] U_element004  label="U_element : 004"  # scripted group (container) (typed FeaturePython)
  n = 1
  ref = U_element
FEATURE [App::DocumentObjectGroupPython] G4_U  # scripted group (container) (typed FeaturePython)
  Dunit = g/cm3
  Dvalue = 18.95
  Group = -> [U_element004]
  conduct = 2
  density = 1
  expand = 3
  formula = U
  name = G4_U
  specific = 4
FEATURE [App::DocumentObjectGroupPython] Np_element001  label="Np_element : 1"  # scripted group (container) (typed FeaturePython)
  n = 1
  ref = Np_element
FEATURE [App::DocumentObjectGroupPython] G4_Np  # scripted group (container) (typed FeaturePython)
  Dunit = g/cm3
  Dvalue = 20.25
  Group = -> [Np_element001]
  conduct = 2
  density = 1
  expand = 3
  formula = Np
  name = G4_Np
  specific = 4
FEATURE [App::DocumentObjectGroupPython] Pu_element002  label="Pu_element : 002"  # scripted group (container) (typed FeaturePython)
  n = 1
  ref = Pu_element
FEATURE [App::DocumentObjectGroupPython] G4_Pu  # scripted group (container) (typed FeaturePython)
  Dunit = g/cm3
  Dvalue = 19.84
  Group = -> [Pu_element002]
  conduct = 2
  density = 1
  expand = 3
  formula = Pu
  name = G4_Pu
  specific = 4
FEATURE [App::DocumentObjectGroupPython] Am_element001  label="Am_element : 1"  # scripted group (container) (typed FeaturePython)
  n = 1
  ref = Am_element
FEATURE [App::DocumentObjectGroupPython] G4_Am  # scripted group (container) (typed FeaturePython)
  Dunit = g/cm3
  Dvalue = 13.67
  Group = -> [Am_element001]
  conduct = 2
  density = 1
  expand = 3
  formula = Am
  name = G4_Am
  specific = 4
FEATURE [App::DocumentObjectGroupPython] Cm_element001  label="Cm_element : 1"  # scripted group (container) (typed FeaturePython)
  n = 1
  ref = Cm_element
FEATURE [App::DocumentObjectGroupPython] G4_Cm  # scripted group (container) (typed FeaturePython)
  Dunit = g/cm3
  Dvalue = 13.51
  Group = -> [Cm_element001]
  conduct = 2
  density = 1
  expand = 3
  formula = Cm
  name = G4_Cm
  specific = 4
FEATURE [App::DocumentObjectGroupPython] Bk_element001  label="Bk_element : 1"  # scripted group (container) (typed FeaturePython)
  n = 1
  ref = Bk_element
FEATURE [App::DocumentObjectGroupPython] G4_Bk  # scripted group (container) (typed FeaturePython)
  Dunit = g/cm3
  Dvalue = 14
  Group = -> [Bk_element001]
  conduct = 2
  density = 1
  expand = 3
  formula = Bk
  name = G4_Bk
  specific = 4
FEATURE [App::DocumentObjectGroupPython] Cf_element001  label="Cf_element : 1"  # scripted group (container) (typed FeaturePython)
  n = 1
  ref = Cf_element
FEATURE [App::DocumentObjectGroupPython] G4_Cf  # scripted group (container) (typed FeaturePython)
  Dunit = g/cm3
  Dvalue = 10
  Group = -> [Cf_element001]
  conduct = 2
  density = 1
  expand = 3
  formula = Cf
  name = G4_Cf
  specific = 4
FEATURE [App::DocumentObjectGroupPython] Element  # scripted group (container) (typed FeaturePython)
  Group = -> [G4_H,G4_He,G4_Li,G4_Be,G4_B,G4_C,G4_N,G4_O,G4_F,G4_Ne,G4_Na,G4_Mg,G4_Al,G4_Si,G4_P,G4_S,G4_Cl,G4_Ar,G4_K,G4_Ca,G4_Sc,G4_Ti,G4_V,G4_Cr,G4_Mn,G4_Fe,G4_Co,G4_Ni,G4_Cu,G4_Zn,G4_Ga,G4_Ge,G4_As,G4_Se,G4_Br,G4_Kr,G4_Rb,G4_Sr,G4_Y,G4_Zr,G4_Nb,G4_Mo,G4_Tc,G4_Ru,G4_Rh,G4_Pd,G4_Ag,G4_Cd,G4_In,G4_Sn,G4_Sb,G4_Te,G4_I,G4_Xe,G4_Cs,G4_Ba,G4_La,G4_Ce,G4_Pr,G4_Nd,G4_Pm,G4_Sm,G4_Eu,G4_Gd,G4_Tb,G4_Dy,G4_Ho,G4_Er,+30 more]
FEATURE [App::DocumentObjectGroupPython] H_element114  label="H_element : 063"  # scripted group (container) (typed FeaturePython)
  n = 2
  ref = H_element
FEATURE [App::DocumentObjectGroupPython] G4_lH2  # scripted group (container) (typed FeaturePython)
  Dunit = g/cm3
  Dvalue = 0.0708
  Group = -> [H_element114]
  conduct = 2
  density = 1
  expand = 3
  formula = G4_lH2
  name = G4_lH2
  specific = 4
FEATURE [App::DocumentObjectGroupPython] N_element049  label="N_element : 022"  # scripted group (container) (typed FeaturePython)
  n = 2
  ref = N_element
FEATURE [App::DocumentObjectGroupPython] G4_lN2  # scripted group (container) (typed FeaturePython)
  Dunit = g/cm3
  Dvalue = 0.807
  Group = -> [N_element049]
  conduct = 2
  density = 1
  expand = 3
  formula = G4_lN2
  name = G4_lN2
  specific = 4
FEATURE [App::DocumentObjectGroupPython] O_element106  label="O_element : 060"  # scripted group (container) (typed FeaturePython)
  n = 2
  ref = O_element
FEATURE [App::DocumentObjectGroupPython] G4_lO2  # scripted group (container) (typed FeaturePython)
  Dunit = g/cm3
  Dvalue = 1.141
  Group = -> [O_element106]
  conduct = 2
  density = 1
  expand = 3
  formula = G4_lO2
  name = G4_lO2
  specific = 4
FEATURE [App::DocumentObjectGroupPython] Ar  label="Ar : 1"  # scripted group (container) (typed FeaturePython)
  n = 1
  ref = Ar
FEATURE [App::DocumentObjectGroupPython] G4_lAr  # scripted group (container) (typed FeaturePython)
  Dunit = g/cm3
  Dvalue = 1.396
  Group = -> [Ar]
  conduct = 2
  density = 1
  expand = 3
  formula = G4_lAr
  name = G4_lAr
  specific = 4
FEATURE [App::DocumentObjectGroupPython] Br  label="Br : 1"  # scripted group (container) (typed FeaturePython)
  n = 1
  ref = Br
FEATURE [App::DocumentObjectGroupPython] G4_lBr  # scripted group (container) (typed FeaturePython)
  Dunit = g/cm3
  Dvalue = 3.1028
  Group = -> [Br]
  conduct = 2
  density = 1
  expand = 3
  formula = G4_lBr
  name = G4_lBr
  specific = 4
FEATURE [App::DocumentObjectGroupPython] Kr  label="Kr : 1"  # scripted group (container) (typed FeaturePython)
  n = 1
  ref = Kr
FEATURE [App::DocumentObjectGroupPython] G4_lKr  # scripted group (container) (typed FeaturePython)
  Dunit = g/cm3
  Dvalue = 2.418
  Group = -> [Kr]
  conduct = 2
  density = 1
  expand = 3
  formula = G4_lKr
  name = G4_lKr
  specific = 4
FEATURE [App::DocumentObjectGroupPython] Xe  label="Xe : 1"  # scripted group (container) (typed FeaturePython)
  n = 1
  ref = Xe
FEATURE [App::DocumentObjectGroupPython] G4_lXe  # scripted group (container) (typed FeaturePython)
  Dunit = g/cm3
  Dvalue = 2.953
  Group = -> [Xe]
  conduct = 2
  density = 1
  expand = 3
  formula = G4_lXe
  name = G4_lXe
  specific = 4
FEATURE [App::DocumentObjectGroupPython] O_element107  label="O_element : 061"  # scripted group (container) (typed FeaturePython)
  n = 4
  ref = O_element
FEATURE [App::DocumentObjectGroupPython] Pb_element004  label="Pb_element : 002"  # scripted group (container) (typed FeaturePython)
  n = 1
  ref = Pb_element
FEATURE [App::DocumentObjectGroupPython] W_element005  label="W_element : 005"  # scripted group (container) (typed FeaturePython)
  n = 1
  ref = W_element
FEATURE [App::DocumentObjectGroupPython] G4_PbWO4  # scripted group (container) (typed FeaturePython)
  Dunit = g/cm3
  Dvalue = 8.28
  Group = -> [O_element107,Pb_element004,W_element005]
  conduct = 2
  density = 1
  expand = 3
  formula = G4_PbWO4
  name = G4_PbWO4
  specific = 4
FEATURE [App::DocumentObjectGroupPython] alactic  label="alactic : 1"  # scripted group (container) (typed FeaturePython)
  n = 1
  ref = alactic
FEATURE [App::DocumentObjectGroupPython] G4_Galactic  # scripted group (container) (typed FeaturePython)
  Dunit = g/cm3
  Dvalue = 0
  Group = -> [alactic]
  conduct = 2
  density = 1
  expand = 3
  formula = G4_Galactic
  name = G4_Galactic
  specific = 4
FEATURE [App::DocumentObjectGroupPython] RAPHITE_POROUS  label="RAPHITE_POROUS : 1"  # scripted group (container) (typed FeaturePython)
  n = 1
  ref = RAPHITE_POROUS
FEATURE [App::DocumentObjectGroupPython] G4_GRAPHITE_POROUS  # scripted group (container) (typed FeaturePython)
  Dunit = g/cm3
  Dvalue = 1.7
  Group = -> [RAPHITE_POROUS]
  conduct = 2
  density = 1
  expand = 3
  formula = G4_GRAPHITE_POROUS
  name = G4_GRAPHITE_POROUS
  specific = 4
FEATURE [App::DocumentObjectGroupPython] H_element115  label="H_element : 0.150"  # scripted group (container) (typed FeaturePython)
  n = 0.080538
FEATURE [App::DocumentObjectGroupPython] C_element125  label="C_element : 0.600"  # scripted group (container) (typed FeaturePython)
  n = 0.599848
FEATURE [App::DocumentObjectGroupPython] O_element108  label="O_element : 0.320"  # scripted group (container) (typed FeaturePython)
  n = 0.319614
FEATURE [App::DocumentObjectGroupPython] G4_LUCITE  # scripted group (container) (typed FeaturePython)
  Dunit = g/cm3
  Dvalue = 1.19
  Group = -> [H_element115,C_element125,O_element108]
  conduct = 2
  density = 1
  expand = 3
  formula = G4_LUCITE
  name = G4_LUCITE
  specific = 4
FEATURE [App::DocumentObjectGroupPython] Cu_element002  label="Cu_element : 62"  # scripted group (container) (typed FeaturePython)
  n = 62
  ref = Cu_element
FEATURE [App::DocumentObjectGroupPython] Zn_element002  label="Zn_element : 35"  # scripted group (container) (typed FeaturePython)
  n = 35
  ref = Zn_element
FEATURE [App::DocumentObjectGroupPython] Pb_element005  label="Pb_element : 3"  # scripted group (container) (typed FeaturePython)
  n = 3
  ref = Pb_element
FEATURE [App::DocumentObjectGroupPython] G4_BRASS  # scripted group (container) (typed FeaturePython)
  Dunit = g/cm3
  Dvalue = 8.52
  Group = -> [Cu_element002,Zn_element002,Pb_element005]
  conduct = 2
  density = 1
  expand = 3
  formula = G4_BRASS
  name = G4_BRASS
  specific = 4
FEATURE [App::DocumentObjectGroupPython] Cu_element003  label="Cu_element : 89"  # scripted group (container) (typed FeaturePython)
  n = 89
  ref = Cu_element
FEATURE [App::DocumentObjectGroupPython] Zn_element003  label="Zn_element : 9"  # scripted group (container) (typed FeaturePython)
  n = 9
  ref = Zn_element
FEATURE [App::DocumentObjectGroupPython] Pb_element006  label="Pb_element : 2"  # scripted group (container) (typed FeaturePython)
  n = 2
  ref = Pb_element
FEATURE [App::DocumentObjectGroupPython] G4_BRONZE  # scripted group (container) (typed FeaturePython)
  Dunit = g/cm3
  Dvalue = 8.82
  Group = -> [Cu_element003,Zn_element003,Pb_element006]
  conduct = 2
  density = 1
  expand = 3
  formula = G4_BRONZE
  name = G4_BRONZE
  specific = 4
FEATURE [App::DocumentObjectGroupPython] Fe_element008  label="Fe_element : 74"  # scripted group (container) (typed FeaturePython)
  n = 74
  ref = Fe_element
FEATURE [App::DocumentObjectGroupPython] Cr_element002  label="Cr_element : 18"  # scripted group (container) (typed FeaturePython)
  n = 18
  ref = Cr_element
FEATURE [App::DocumentObjectGroupPython] Ni_element002  label="Ni_element : 8"  # scripted group (container) (typed FeaturePython)
  n = 8
  ref = Ni_element
FEATURE [App::DocumentObjectGroupPython] G4_STAINLESS_STEEL  label="G4_STAINLESS-STEEL"  # scripted group (container) (typed FeaturePython)
  Dunit = g/cm3
  Dvalue = 8
  Group = -> [Fe_element008,Cr_element002,Ni_element002]
  conduct = 2
  density = 1
  expand = 3
  formula = G4_STAINLESS-STEEL
  name = G4_STAINLESS-STEEL
  specific = 4
FEATURE [App::DocumentObjectGroupPython] H_element116  label="H_element : 064"  # scripted group (container) (typed FeaturePython)
  n = 18
  ref = H_element
FEATURE [App::DocumentObjectGroupPython] C_element126  label="C_element : 071"  # scripted group (container) (typed FeaturePython)
  n = 12
  ref = C_element
FEATURE [App::DocumentObjectGroupPython] O_element109  label="O_element : 062"  # scripted group (container) (typed FeaturePython)
  n = 7
  ref = O_element
FEATURE [App::DocumentObjectGroupPython] G4_CR39  # scripted group (container) (typed FeaturePython)
  Dunit = g/cm3
  Dvalue = 1.32
  Group = -> [H_element116,C_element126,O_element109]
  conduct = 2
  density = 1
  expand = 3
  formula = G4_CR39
  name = G4_CR39
  specific = 4
FEATURE [App::DocumentObjectGroupPython] H_element117  label="H_element : 38"  # scripted group (container) (typed FeaturePython)
  n = 38
  ref = H_element
FEATURE [App::DocumentObjectGroupPython] C_element127  label="C_element : 072"  # scripted group (container) (typed FeaturePython)
  n = 18
  ref = C_element
FEATURE [App::DocumentObjectGroupPython] O_element110  label="O_element : 063"  # scripted group (container) (typed FeaturePython)
  n = 1
  ref = O_element
FEATURE [App::DocumentObjectGroupPython] G4_OCTADECANOL  # scripted group (container) (typed FeaturePython)
  Dunit = g/cm3
  Dvalue = 0.812
  Group = -> [H_element117,C_element127,O_element110]
  conduct = 2
  density = 1
  expand = 3
  formula = G4_OCTADECANOL
  name = G4_OCTADECANOL
  specific = 4
FEATURE [App::DocumentObjectGroupPython] HEP  # scripted group (container) (typed FeaturePython)
  Group = -> [G4_lH2,G4_lN2,G4_lO2,G4_lAr,G4_lBr,G4_lKr,G4_lXe,G4_PbWO4,G4_Galactic,G4_GRAPHITE_POROUS,G4_LUCITE,G4_BRASS,G4_BRONZE,G4_STAINLESS_STEEL,G4_CR39,G4_OCTADECANOL]
FEATURE [App::DocumentObjectGroupPython] C_element128  label="C_element : 073"  # scripted group (container) (typed FeaturePython)
  n = 14
  ref = C_element
FEATURE [App::DocumentObjectGroupPython] H_element118  label="H_element : 065"  # scripted group (container) (typed FeaturePython)
  n = 10
  ref = H_element
FEATURE [App::DocumentObjectGroupPython] O_element111  label="O_element : 064"  # scripted group (container) (typed FeaturePython)
  n = 2
  ref = O_element
FEATURE [App::DocumentObjectGroupPython] N_element050  label="N_element : 023"  # scripted group (container) (typed FeaturePython)
  n = 2
  ref = N_element
FEATURE [App::DocumentObjectGroupPython] G4_KEVLAR  # scripted group (container) (typed FeaturePython)
  Dunit = g/cm3
  Dvalue = 1.44
  Group = -> [C_element128,H_element118,O_element111,N_element050]
  conduct = 2
  density = 1
  expand = 3
  formula = G4_KEVLAR
  name = G4_KEVLAR
  specific = 4
FEATURE [App::DocumentObjectGroupPython] C_element129  label="C_element : 074"  # scripted group (container) (typed FeaturePython)
  n = 10
  ref = C_element
FEATURE [App::DocumentObjectGroupPython] H_element119  label="H_element : 066"  # scripted group (container) (typed FeaturePython)
  n = 8
  ref = H_element
FEATURE [App::DocumentObjectGroupPython] O_element112  label="O_element : 065"  # scripted group (container) (typed FeaturePython)
  n = 4
  ref = O_element
FEATURE [App::DocumentObjectGroupPython] G4_DACRON  # scripted group (container) (typed FeaturePython)
  Dunit = g/cm3
  Dvalue = 1.4
  Group = -> [C_element129,H_element119,O_element112]
  conduct = 2
  density = 1
  expand = 3
  formula = G4_DACRON
  name = G4_DACRON
  specific = 4
FEATURE [App::DocumentObjectGroupPython] C_element130  label="C_element : 075"  # scripted group (container) (typed FeaturePython)
  n = 4
  ref = C_element
FEATURE [App::DocumentObjectGroupPython] H_element120  label="H_element : 067"  # scripted group (container) (typed FeaturePython)
  n = 5
  ref = H_element
FEATURE [App::DocumentObjectGroupPython] Cl_element030  label="Cl_element : 016"  # scripted group (container) (typed FeaturePython)
  n = 1
  ref = Cl_element
FEATURE [App::DocumentObjectGroupPython] G4_NEOPRENE  # scripted group (container) (typed FeaturePython)
  Dunit = g/cm3
  Dvalue = 1.23
  Group = -> [C_element130,H_element120,Cl_element030]
  conduct = 2
  density = 1
  expand = 3
  formula = G4_NEOPRENE
  name = G4_NEOPRENE
  specific = 4
FEATURE [App::DocumentObjectGroupPython] Space  # scripted group (container) (typed FeaturePython)
  Group = -> [G4_KEVLAR,G4_DACRON,G4_NEOPRENE]
FEATURE [App::DocumentObjectGroupPython] H_element121  label="H_element : 068"  # scripted group (container) (typed FeaturePython)
  n = 5
  ref = H_element
FEATURE [App::DocumentObjectGroupPython] C_element131  label="C_element : 076"  # scripted group (container) (typed FeaturePython)
  n = 4
  ref = C_element
FEATURE [App::DocumentObjectGroupPython] N_element051  label="N_element : 3"  # scripted group (container) (typed FeaturePython)
  n = 3
  ref = N_element
FEATURE [App::DocumentObjectGroupPython] O_element113  label="O_element : 066"  # scripted group (container) (typed FeaturePython)
  n = 1
  ref = O_element
FEATURE [App::DocumentObjectGroupPython] G4_CYTOSINE  # scripted group (container) (typed FeaturePython)
  Dunit = g/cm3
  Dvalue = 1.55
  Group = -> [H_element121,C_element131,N_element051,O_element113]
  conduct = 2
  density = 1
  expand = 3
  formula = G4_CYTOSINE
  name = G4_CYTOSINE
  specific = 4
FEATURE [App::DocumentObjectGroupPython] H_element122  label="H_element : 069"  # scripted group (container) (typed FeaturePython)
  n = 6
  ref = H_element
FEATURE [App::DocumentObjectGroupPython] C_element132  label="C_element : 077"  # scripted group (container) (typed FeaturePython)
  n = 5
  ref = C_element
FEATURE [App::DocumentObjectGroupPython] N_element052  label="N_element : 024"  # scripted group (container) (typed FeaturePython)
  n = 2
  ref = N_element
FEATURE [App::DocumentObjectGroupPython] O_element114  label="O_element : 067"  # scripted group (container) (typed FeaturePython)
  n = 2
  ref = O_element
FEATURE [App::DocumentObjectGroupPython] G4_THYMINE  # scripted group (container) (typed FeaturePython)
  Dunit = g/cm3
  Dvalue = 1.23
  Group = -> [H_element122,C_element132,N_element052,O_element114]
  conduct = 2
  density = 1
  expand = 3
  formula = G4_THYMINE
  name = G4_THYMINE
  specific = 4
FEATURE [App::DocumentObjectGroupPython] H_element123  label="H_element : 070"  # scripted group (container) (typed FeaturePython)
  n = 4
  ref = H_element
FEATURE [App::DocumentObjectGroupPython] C_element133  label="C_element : 078"  # scripted group (container) (typed FeaturePython)
  n = 4
  ref = C_element
FEATURE [App::DocumentObjectGroupPython] N_element053  label="N_element : 025"  # scripted group (container) (typed FeaturePython)
  n = 2
  ref = N_element
FEATURE [App::DocumentObjectGroupPython] O_element115  label="O_element : 068"  # scripted group (container) (typed FeaturePython)
  n = 2
  ref = O_element
FEATURE [App::DocumentObjectGroupPython] G4_URACIL  # scripted group (container) (typed FeaturePython)
  Dunit = g/cm3
  Dvalue = 1.32
  Group = -> [H_element123,C_element133,N_element053,O_element115]
  conduct = 2
  density = 1
  expand = 3
  formula = G4_URACIL
  name = G4_URACIL
  specific = 4
FEATURE [App::DocumentObjectGroupPython] H_element124  label="H_element : 071"  # scripted group (container) (typed FeaturePython)
  n = 4
  ref = H_element
FEATURE [App::DocumentObjectGroupPython] C_element134  label="C_element : 079"  # scripted group (container) (typed FeaturePython)
  n = 5
  ref = C_element
FEATURE [App::DocumentObjectGroupPython] N_element054  label="N_element : 026"  # scripted group (container) (typed FeaturePython)
  n = 5
  ref = N_element
FEATURE [App::DocumentObjectGroupPython] G4_DNA_ADENINE  # scripted group (container) (typed FeaturePython)
  Dunit = g/cm3
  Dvalue = 1
  Group = -> [H_element124,C_element134,N_element054]
  conduct = 2
  density = 1
  expand = 3
  formula = G4_DNA_ADENINE
  name = G4_DNA_ADENINE
  specific = 4
FEATURE [App::DocumentObjectGroupPython] H_element125  label="H_element : 072"  # scripted group (container) (typed FeaturePython)
  n = 4
  ref = H_element
FEATURE [App::DocumentObjectGroupPython] C_element135  label="C_element : 080"  # scripted group (container) (typed FeaturePython)
  n = 5
  ref = C_element
FEATURE [App::DocumentObjectGroupPython] N_element055  label="N_element : 027"  # scripted group (container) (typed FeaturePython)
  n = 5
  ref = N_element
FEATURE [App::DocumentObjectGroupPython] O_element116  label="O_element : 069"  # scripted group (container) (typed FeaturePython)
  n = 1
  ref = O_element
FEATURE [App::DocumentObjectGroupPython] G4_DNA_GUANINE  # scripted group (container) (typed FeaturePython)
  Dunit = g/cm3
  Dvalue = 1
  Group = -> [H_element125,C_element135,N_element055,O_element116]
  conduct = 2
  density = 1
  expand = 3
  formula = G4_DNA_GUANINE
  name = G4_DNA_GUANINE
  specific = 4
FEATURE [App::DocumentObjectGroupPython] H_element126  label="H_element : 073"  # scripted group (container) (typed FeaturePython)
  n = 4
  ref = H_element
FEATURE [App::DocumentObjectGroupPython] C_element136  label="C_element : 081"  # scripted group (container) (typed FeaturePython)
  n = 4
  ref = C_element
FEATURE [App::DocumentObjectGroupPython] N_element056  label="N_element : 028"  # scripted group (container) (typed FeaturePython)
  n = 3
  ref = N_element
FEATURE [App::DocumentObjectGroupPython] O_element117  label="O_element : 070"  # scripted group (container) (typed FeaturePython)
  n = 1
  ref = O_element
FEATURE [App::DocumentObjectGroupPython] G4_DNA_CYTOSINE  # scripted group (container) (typed FeaturePython)
  Dunit = g/cm3
  Dvalue = 1
  Group = -> [H_element126,C_element136,N_element056,O_element117]
  conduct = 2
  density = 1
  expand = 3
  formula = G4_DNA_CYTOSINE
  name = G4_DNA_CYTOSINE
  specific = 4
FEATURE [App::DocumentObjectGroupPython] H_element127  label="H_element : 074"  # scripted group (container) (typed FeaturePython)
  n = 5
  ref = H_element
FEATURE [App::DocumentObjectGroupPython] C_element137  label="C_element : 082"  # scripted group (container) (typed FeaturePython)
  n = 5
  ref = C_element
FEATURE [App::DocumentObjectGroupPython] N_element057  label="N_element : 029"  # scripted group (container) (typed FeaturePython)
  n = 2
  ref = N_element
FEATURE [App::DocumentObjectGroupPython] O_element118  label="O_element : 071"  # scripted group (container) (typed FeaturePython)
  n = 2
  ref = O_element
FEATURE [App::DocumentObjectGroupPython] G4_DNA_THYMINE  # scripted group (container) (typed FeaturePython)
  Dunit = g/cm3
  Dvalue = 1
  Group = -> [H_element127,C_element137,N_element057,O_element118]
  conduct = 2
  density = 1
  expand = 3
  formula = G4_DNA_THYMINE
  name = G4_DNA_THYMINE
  specific = 4
FEATURE [App::DocumentObjectGroupPython] H_element128  label="H_element : 075"  # scripted group (container) (typed FeaturePython)
  n = 3
  ref = H_element
FEATURE [App::DocumentObjectGroupPython] C_element138  label="C_element : 083"  # scripted group (container) (typed FeaturePython)
  n = 4
  ref = C_element
FEATURE [App::DocumentObjectGroupPython] N_element058  label="N_element : 030"  # scripted group (container) (typed FeaturePython)
  n = 2
  ref = N_element
FEATURE [App::DocumentObjectGroupPython] O_element119  label="O_element : 072"  # scripted group (container) (typed FeaturePython)
  n = 2
  ref = O_element
FEATURE [App::DocumentObjectGroupPython] G4_DNA_URACIL  # scripted group (container) (typed FeaturePython)
  Dunit = g/cm3
  Dvalue = 1
  Group = -> [H_element128,C_element138,N_element058,O_element119]
  conduct = 2
  density = 1
  expand = 3
  formula = G4_DNA_URACIL
  name = G4_DNA_URACIL
  specific = 4
FEATURE [App::DocumentObjectGroupPython] H_element129  label="H_element : 076"  # scripted group (container) (typed FeaturePython)
  n = 10
  ref = H_element
FEATURE [App::DocumentObjectGroupPython] C_element139  label="C_element : 084"  # scripted group (container) (typed FeaturePython)
  n = 10
  ref = C_element
FEATURE [App::DocumentObjectGroupPython] N_element059  label="N_element : 031"  # scripted group (container) (typed FeaturePython)
  n = 5
  ref = N_element
FEATURE [App::DocumentObjectGroupPython] O_element120  label="O_element : 073"  # scripted group (container) (typed FeaturePython)
  n = 4
  ref = O_element
FEATURE [App::DocumentObjectGroupPython] G4_DNA_ADENOSINE  # scripted group (container) (typed FeaturePython)
  Dunit = g/cm3
  Dvalue = 1
  Group = -> [H_element129,C_element139,N_element059,O_element120]
  conduct = 2
  density = 1
  expand = 3
  formula = G4_DNA_ADENOSINE
  name = G4_DNA_ADENOSINE
  specific = 4
FEATURE [App::DocumentObjectGroupPython] H_element130  label="H_element : 077"  # scripted group (container) (typed FeaturePython)
  n = 10
  ref = H_element
FEATURE [App::DocumentObjectGroupPython] C_element140  label="C_element : 085"  # scripted group (container) (typed FeaturePython)
  n = 10
  ref = C_element
FEATURE [App::DocumentObjectGroupPython] N_element060  label="N_element : 032"  # scripted group (container) (typed FeaturePython)
  n = 5
  ref = N_element
FEATURE [App::DocumentObjectGroupPython] O_element121  label="O_element : 074"  # scripted group (container) (typed FeaturePython)
  n = 5
  ref = O_element
FEATURE [App::DocumentObjectGroupPython] G4_DNA_GUANOSINE  # scripted group (container) (typed FeaturePython)
  Dunit = g/cm3
  Dvalue = 1
  Group = -> [H_element130,C_element140,N_element060,O_element121]
  conduct = 2
  density = 1
  expand = 3
  formula = G4_DNA_GUANOSINE
  name = G4_DNA_GUANOSINE
  specific = 4
FEATURE [App::DocumentObjectGroupPython] H_element131  label="H_element : 078"  # scripted group (container) (typed FeaturePython)
  n = 10
  ref = H_element
FEATURE [App::DocumentObjectGroupPython] C_element141  label="C_element : 086"  # scripted group (container) (typed FeaturePython)
  n = 9
  ref = C_element
FEATURE [App::DocumentObjectGroupPython] N_element061  label="N_element : 033"  # scripted group (container) (typed FeaturePython)
  n = 3
  ref = N_element
FEATURE [App::DocumentObjectGroupPython] O_element122  label="O_element : 075"  # scripted group (container) (typed FeaturePython)
  n = 5
  ref = O_element
FEATURE [App::DocumentObjectGroupPython] G4_DNA_CYTIDINE  # scripted group (container) (typed FeaturePython)
  Dunit = g/cm3
  Dvalue = 1
  Group = -> [H_element131,C_element141,N_element061,O_element122]
  conduct = 2
  density = 1
  expand = 3
  formula = G4_DNA_CYTIDINE
  name = G4_DNA_CYTIDINE
  specific = 4
FEATURE [App::DocumentObjectGroupPython] H_element132  label="H_element : 079"  # scripted group (container) (typed FeaturePython)
  n = 9
  ref = H_element
FEATURE [App::DocumentObjectGroupPython] C_element142  label="C_element : 087"  # scripted group (container) (typed FeaturePython)
  n = 9
  ref = C_element
FEATURE [App::DocumentObjectGroupPython] N_element062  label="N_element : 034"  # scripted group (container) (typed FeaturePython)
  n = 2
  ref = N_element
FEATURE [App::DocumentObjectGroupPython] O_element123  label="O_element : 076"  # scripted group (container) (typed FeaturePython)
  n = 6
  ref = O_element
FEATURE [App::DocumentObjectGroupPython] G4_DNA_URIDINE  # scripted group (container) (typed FeaturePython)
  Dunit = g/cm3
  Dvalue = 1
  Group = -> [H_element132,C_element142,N_element062,O_element123]
  conduct = 2
  density = 1
  expand = 3
  formula = G4_DNA_URIDINE
  name = G4_DNA_URIDINE
  specific = 4
FEATURE [App::DocumentObjectGroupPython] H_element133  label="H_element : 080"  # scripted group (container) (typed FeaturePython)
  n = 11
  ref = H_element
FEATURE [App::DocumentObjectGroupPython] C_element143  label="C_element : 088"  # scripted group (container) (typed FeaturePython)
  n = 10
  ref = C_element
FEATURE [App::DocumentObjectGroupPython] N_element063  label="N_element : 035"  # scripted group (container) (typed FeaturePython)
  n = 2
  ref = N_element
FEATURE [App::DocumentObjectGroupPython] O_element124  label="O_element : 077"  # scripted group (container) (typed FeaturePython)
  n = 6
  ref = O_element
FEATURE [App::DocumentObjectGroupPython] G4_DNA_METHYLURIDINE  # scripted group (container) (typed FeaturePython)
  Dunit = g/cm3
  Dvalue = 1
  Group = -> [H_element133,C_element143,N_element063,O_element124]
  conduct = 2
  density = 1
  expand = 3
  formula = G4_DNA_METHYLURIDINE
  name = G4_DNA_METHYLURIDINE
  specific = 4
FEATURE [App::DocumentObjectGroupPython] P_element014  label="P_element : 003"  # scripted group (container) (typed FeaturePython)
  n = 1
  ref = P_element
FEATURE [App::DocumentObjectGroupPython] O_element125  label="O_element : 078"  # scripted group (container) (typed FeaturePython)
  n = 3
  ref = O_element
FEATURE [App::DocumentObjectGroupPython] G4_DNA_MONOPHOSPHATE  # scripted group (container) (typed FeaturePython)
  Dunit = g/cm3
  Dvalue = 1
  Group = -> [P_element014,O_element125]
  conduct = 2
  density = 1
  expand = 3
  formula = G4_DNA_MONOPHOSPHATE
  name = G4_DNA_MONOPHOSPHATE
  specific = 4
FEATURE [App::DocumentObjectGroupPython] H_element134  label="H_element : 081"  # scripted group (container) (typed FeaturePython)
  n = 10
  ref = H_element
FEATURE [App::DocumentObjectGroupPython] C_element144  label="C_element : 089"  # scripted group (container) (typed FeaturePython)
  n = 10
  ref = C_element
FEATURE [App::DocumentObjectGroupPython] N_element064  label="N_element : 036"  # scripted group (container) (typed FeaturePython)
  n = 5
  ref = N_element
FEATURE [App::DocumentObjectGroupPython] O_element126  label="O_element : 079"  # scripted group (container) (typed FeaturePython)
  n = 7
  ref = O_element
FEATURE [App::DocumentObjectGroupPython] P_element015  label="P_element : 004"  # scripted group (container) (typed FeaturePython)
  n = 1
  ref = P_element
FEATURE [App::DocumentObjectGroupPython] G4_DNA_A  # scripted group (container) (typed FeaturePython)
  Dunit = g/cm3
  Dvalue = 1
  Group = -> [H_element134,C_element144,N_element064,O_element126,P_element015]
  conduct = 2
  density = 1
  expand = 3
  formula = G4_DNA_A
  name = G4_DNA_A
  specific = 4
FEATURE [App::DocumentObjectGroupPython] H_element135  label="H_element : 082"  # scripted group (container) (typed FeaturePython)
  n = 10
  ref = H_element
FEATURE [App::DocumentObjectGroupPython] C_element145  label="C_element : 090"  # scripted group (container) (typed FeaturePython)
  n = 10
  ref = C_element
FEATURE [App::DocumentObjectGroupPython] N_element065  label="N_element : 037"  # scripted group (container) (typed FeaturePython)
  n = 5
  ref = N_element
FEATURE [App::DocumentObjectGroupPython] O_element127  label="O_element : 8"  # scripted group (container) (typed FeaturePython)
  n = 8
  ref = O_element
FEATURE [App::DocumentObjectGroupPython] P_element016  label="P_element : 005"  # scripted group (container) (typed FeaturePython)
  n = 1
  ref = P_element
FEATURE [App::DocumentObjectGroupPython] G4_DNA_G  # scripted group (container) (typed FeaturePython)
  Dunit = g/cm3
  Dvalue = 1
  Group = -> [H_element135,C_element145,N_element065,O_element127,P_element016]
  conduct = 2
  density = 1
  expand = 3
  formula = G4_DNA_G
  name = G4_DNA_G
  specific = 4
FEATURE [App::DocumentObjectGroupPython] H_element136  label="H_element : 083"  # scripted group (container) (typed FeaturePython)
  n = 10
  ref = H_element
FEATURE [App::DocumentObjectGroupPython] C_element146  label="C_element : 091"  # scripted group (container) (typed FeaturePython)
  n = 9
  ref = C_element
FEATURE [App::DocumentObjectGroupPython] N_element066  label="N_element : 038"  # scripted group (container) (typed FeaturePython)
  n = 3
  ref = N_element
FEATURE [App::DocumentObjectGroupPython] O_element128  label="O_element : 080"  # scripted group (container) (typed FeaturePython)
  n = 8
  ref = O_element
FEATURE [App::DocumentObjectGroupPython] P_element017  label="P_element : 006"  # scripted group (container) (typed FeaturePython)
  n = 1
  ref = P_element
FEATURE [App::DocumentObjectGroupPython] G4_DNA_C  # scripted group (container) (typed FeaturePython)
  Dunit = g/cm3
  Dvalue = 1
  Group = -> [H_element136,C_element146,N_element066,O_element128,P_element017]
  conduct = 2
  density = 1
  expand = 3
  formula = G4_DNA_C
  name = G4_DNA_C
  specific = 4
FEATURE [App::DocumentObjectGroupPython] H_element137  label="H_element : 084"  # scripted group (container) (typed FeaturePython)
  n = 9
  ref = H_element
FEATURE [App::DocumentObjectGroupPython] C_element147  label="C_element : 092"  # scripted group (container) (typed FeaturePython)
  n = 9
  ref = C_element
FEATURE [App::DocumentObjectGroupPython] N_element067  label="N_element : 039"  # scripted group (container) (typed FeaturePython)
  n = 2
  ref = N_element
FEATURE [App::DocumentObjectGroupPython] O_element129  label="O_element : 9"  # scripted group (container) (typed FeaturePython)
  n = 9
  ref = O_element
FEATURE [App::DocumentObjectGroupPython] P_element018  label="P_element : 007"  # scripted group (container) (typed FeaturePython)
  n = 1
  ref = P_element
FEATURE [App::DocumentObjectGroupPython] G4_DNA_U  # scripted group (container) (typed FeaturePython)
  Dunit = g/cm3
  Dvalue = 1
  Group = -> [H_element137,C_element147,N_element067,O_element129,P_element018]
  conduct = 2
  density = 1
  expand = 3
  formula = G4_DNA_U
  name = G4_DNA_U
  specific = 4
FEATURE [App::DocumentObjectGroupPython] H_element138  label="H_element : 085"  # scripted group (container) (typed FeaturePython)
  n = 11
  ref = H_element
FEATURE [App::DocumentObjectGroupPython] C_element148  label="C_element : 093"  # scripted group (container) (typed FeaturePython)
  n = 10
  ref = C_element
FEATURE [App::DocumentObjectGroupPython] N_element068  label="N_element : 040"  # scripted group (container) (typed FeaturePython)
  n = 2
  ref = N_element
FEATURE [App::DocumentObjectGroupPython] O_element130  label="O_element : 081"  # scripted group (container) (typed FeaturePython)
  n = 9
  ref = O_element
FEATURE [App::DocumentObjectGroupPython] P_element019  label="P_element : 008"  # scripted group (container) (typed FeaturePython)
  n = 1
  ref = P_element
FEATURE [App::DocumentObjectGroupPython] G4_DNA_MU  # scripted group (container) (typed FeaturePython)
  Dunit = g/cm3
  Dvalue = 1
  Group = -> [H_element138,C_element148,N_element068,O_element130,P_element019]
  conduct = 2
  density = 1
  expand = 3
  formula = G4_DNA_MU
  name = G4_DNA_MU
  specific = 4
FEATURE [App::DocumentObjectGroupPython] BioChemical  # scripted group (container) (typed FeaturePython)
  Group = -> [G4_CYTOSINE,G4_THYMINE,G4_URACIL,G4_DNA_ADENINE,G4_DNA_GUANINE,G4_DNA_CYTOSINE,G4_DNA_THYMINE,G4_DNA_URACIL,G4_DNA_ADENOSINE,G4_DNA_GUANOSINE,G4_DNA_CYTIDINE,G4_DNA_URIDINE,G4_DNA_METHYLURIDINE,G4_DNA_MONOPHOSPHATE,G4_DNA_A,G4_DNA_G,G4_DNA_C,G4_DNA_U,G4_DNA_MU]
FEATURE [App::DocumentObjectGroupPython] G4Materials  # scripted group (container) (typed FeaturePython)
  Group = -> [NIST,Element,HEP,Space,BioChemical]
  version = 1
FEATURE [App::DocumentObjectGroupPython] Geant4  # scripted group (container) (typed FeaturePython)
  Group = -> [G4Isotopes,G4Elements,G4Materials]
FEATURE [App::DocumentObjectGroupPython] Materials  # scripted group (container) (typed FeaturePython)
  Group = -> [LYSO,Air,Glass,Geant4]
FEATURE [Part::FeaturePython] GDMLBox_World  # WARN: FeaturePython — macro-defined, semantics opaque (R4)
  lunit = 2
  material = 1
  x = 50
  y = 50
  z = 50
FEATURE [Part::FeaturePython] GDMLBox_Obj001  # WARN: FeaturePython — macro-defined, semantics opaque (R4)
  lunit = 2
  material = 0
  x = 2
  y = 2
  z = 15
FEATURE [Part::FeaturePython] GDMLBox_GlassPlate001  # WARN: FeaturePython — macro-defined, semantics opaque (R4)
  lunit = 2
  material = 2
  x = 2
  y = 2
  z = 2
FEATURE [App::Part] Det001
  Group = -> [GDMLBox_GlassPlate001]
  Origin = -> Origin005
  Placement = pos=(0,0,8.5) rot=(0,0,1;0rad)
FEATURE [App::FeaturePython] ScintWrap001  # WARN: FeaturePython — macro-defined, semantics opaque (R4)
  PV1 = Obj001
  PV2 = Det001
  Surface = ScintWrap
FEATURE [App::Part] Obj001
  Group = -> [GDMLBox_Obj001,Det001,ScintWrap001]
  Origin = -> Origin004
FEATURE [App::Link] GDMLBox_Obj001001
  LinkedObject = -> GDMLBox_Obj001
FEATURE [App::Link] GDMLBox_GlassPlate001001
  LinkedObject = -> GDMLBox_GlassPlate001
FEATURE [App::Part] Det001001
  Group = -> [GDMLBox_GlassPlate001001]
  Origin = -> Origin007
  Placement = pos=(0,0,8.5) rot=(0,0,1;0rad)
FEATURE [App::FeaturePython] ScintWrap002  # WARN: FeaturePython — macro-defined, semantics opaque (R4)
  PV1 = Obj001001
  PV2 = Det001001
  Surface = ScintWrap
FEATURE [App::Part] Obj001001
  CopyNumber = 1
  Group = -> [GDMLBox_Obj001001,Det001001,ScintWrap002]
  Origin = -> Origin006
  Placement = pos=(0,3,0) rot=(0,0,1;0rad)
FEATURE [App::Link] GDMLBox_Obj001002
  LinkedObject = -> GDMLBox_Obj001
FEATURE [App::Link] GDMLBox_GlassPlate001002
  LinkedObject = -> GDMLBox_GlassPlate001
FEATURE [App::Part] Det001002
  Group = -> [GDMLBox_GlassPlate001002]
  Origin = -> Origin009
  Placement = pos=(0,0,8.5) rot=(0,0,1;0rad)
FEATURE [App::FeaturePython] ScintWrap003  # WARN: FeaturePython — macro-defined, semantics opaque (R4)
  PV1 = Obj001002
  PV2 = Det001002
  Surface = ScintWrap
FEATURE [App::Part] Obj001002
  CopyNumber = 2
  Group = -> [GDMLBox_Obj001002,Det001002,ScintWrap003]
  Origin = -> Origin008
  Placement = pos=(3,0,0) rot=(0,0,1;0rad)
FEATURE [App::Link] GDMLBox_Obj001003
  LinkedObject = -> GDMLBox_Obj001
FEATURE [App::Link] GDMLBox_GlassPlate001003
  LinkedObject = -> GDMLBox_GlassPlate001
FEATURE [App::Part] Det001003
  Group = -> [GDMLBox_GlassPlate001003]
  Origin = -> Origin011
  Placement = pos=(0,0,8.5) rot=(0,0,1;0rad)
FEATURE [App::FeaturePython] ScintWrap004  # WARN: FeaturePython — macro-defined, semantics opaque (R4)
  PV1 = Obj001003
  PV2 = Det001003
  Surface = ScintWrap
FEATURE [App::Part] Obj001003
  CopyNumber = 3
  Group = -> [GDMLBox_Obj001003,Det001003,ScintWrap004]
  Origin = -> Origin010
  Placement = pos=(3,3,0) rot=(0,0,1;0rad)
FEATURE [App::Part] Array001
  Group = -> [Obj001,Obj001001,Obj001002,Obj001003]
  Origin = -> Origin003
FEATURE [App::Part] World
  Group = -> [GDMLBox_World,Array001]
  Origin = -> Origin
